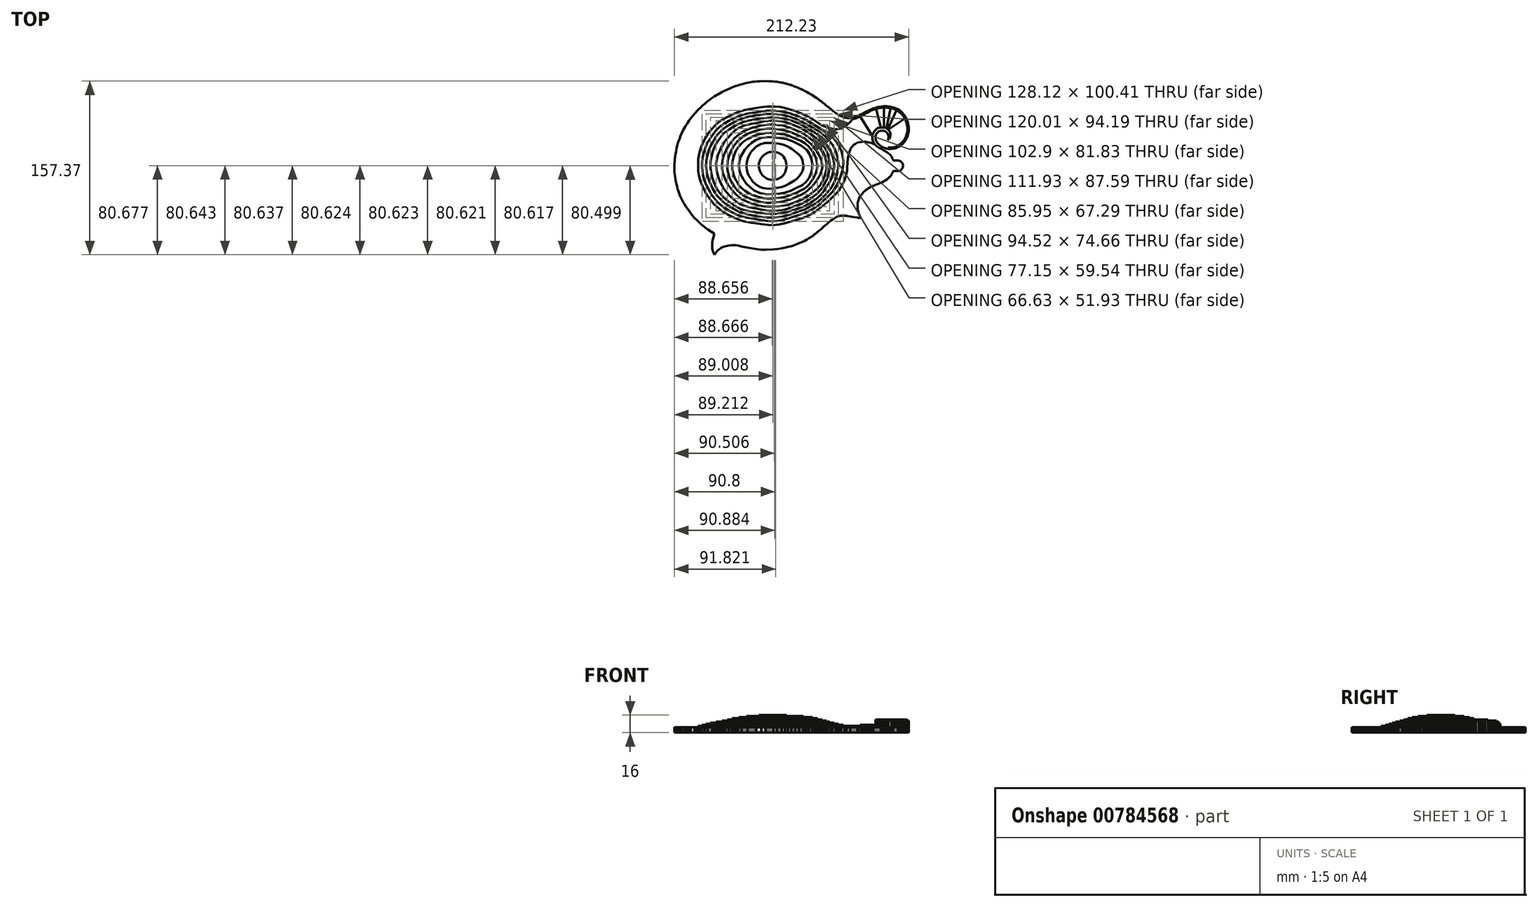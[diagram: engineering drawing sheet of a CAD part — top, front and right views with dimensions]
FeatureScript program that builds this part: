
annotation { "Feature Type Name" : "Feature", "Feature Type Description" : "" }
export const myFeature = defineFeature(function(context is Context, id is Id, definition is map)
    precondition{}
    {
        {
            var Q0;
            Q0=qCreatedBy(makeId("Top.planeOp"),FACE);
            var sketch = newSketch(context, id + "F0", { "sketchPlane" : qUnion([Q0])});
            skLineSegment(sketch, "E0", {"start": v(-90.73, -17.49) * mm, "end": v(-90.49, -12.16) * mm});
            skLineSegment(sketch, "E1", {"start": v(-90.49, -12.16) * mm, "end": v(-89.94, -7.25) * mm});
            skLineSegment(sketch, "E2", {"start": v(-89.94, -7.25) * mm, "end": v(-89.42, -4.36) * mm});
            skLineSegment(sketch, "E3", {"start": v(-89.42, -4.36) * mm, "end": v(-88.87, -1.75) * mm});
            skLineSegment(sketch, "E4", {"start": v(-88.87, -1.75) * mm, "end": v(-88.18, 1.03) * mm});
            skLineSegment(sketch, "E5", {"start": v(-88.18, 1.03) * mm, "end": v(-87.3, 4.01) * mm});
            skLineSegment(sketch, "E6", {"start": v(-87.3, 4.01) * mm, "end": v(-86.2, 7.14) * mm});
            skLineSegment(sketch, "E7", {"start": v(-86.2, 7.14) * mm, "end": v(-85.47, 9.1) * mm});
            skLineSegment(sketch, "E8", {"start": v(-85.47, 9.1) * mm, "end": v(-84.14, 12.2) * mm});
            skLineSegment(sketch, "E9", {"start": v(-84.14, 12.2) * mm, "end": v(-82.84, 14.94) * mm});
            skLineSegment(sketch, "E10", {"start": v(-82.84, 14.94) * mm, "end": v(-81, 18.16) * mm});
            skLineSegment(sketch, "E11", {"start": v(-81, 18.16) * mm, "end": v(-79.18, 21.04) * mm});
            skLineSegment(sketch, "E12", {"start": v(-79.18, 21.04) * mm, "end": v(-77.53, 23.47) * mm});
            skLineSegment(sketch, "E13", {"start": v(-77.53, 23.47) * mm, "end": v(-75.8, 25.8) * mm});
            skLineSegment(sketch, "E14", {"start": v(-75.8, 25.8) * mm, "end": v(-73.69, 28.43) * mm});
            skLineSegment(sketch, "E15", {"start": v(-73.69, 28.43) * mm, "end": v(-71.8, 30.51) * mm});
            skLineSegment(sketch, "E16", {"start": v(-71.8, 30.51) * mm, "end": v(-69.81, 32.66) * mm});
            skLineSegment(sketch, "E17", {"start": v(-69.81, 32.66) * mm, "end": v(-68.56, 33.97) * mm});
            skLineSegment(sketch, "E18", {"start": v(-68.56, 33.97) * mm, "end": v(-67.12, 35.38) * mm});
            skLineSegment(sketch, "E19", {"start": v(-67.12, 35.38) * mm, "end": v(-65.66, 36.77) * mm});
            skLineSegment(sketch, "E20", {"start": v(-65.66, 36.77) * mm, "end": v(-64.6, 37.7) * mm});
            skLineSegment(sketch, "E21", {"start": v(-64.6, 37.7) * mm, "end": v(-63.32, 38.85) * mm});
            skLineSegment(sketch, "E22", {"start": v(-63.32, 38.85) * mm, "end": v(-62.02, 39.95) * mm});
            skLineSegment(sketch, "E23", {"start": v(-62.02, 39.95) * mm, "end": v(-60.78, 40.93) * mm});
            skLineSegment(sketch, "E24", {"start": v(-60.78, 40.93) * mm, "end": v(-59.39, 42.03) * mm});
            skLineSegment(sketch, "E25", {"start": v(-59.39, 42.03) * mm, "end": v(-57.92, 43.11) * mm});
            skLineSegment(sketch, "E26", {"start": v(-57.92, 43.11) * mm, "end": v(-56.5, 44.12) * mm});
            skLineSegment(sketch, "E27", {"start": v(-56.5, 44.12) * mm, "end": v(-54.67, 45.42) * mm});
            skLineSegment(sketch, "E28", {"start": v(-54.67, 45.42) * mm, "end": v(-53.1, 46.38) * mm});
            skLineSegment(sketch, "E29", {"start": v(-53.1, 46.38) * mm, "end": v(-51.26, 47.42) * mm});
            skLineSegment(sketch, "E30", {"start": v(-51.26, 47.42) * mm, "end": v(-49.56, 48.36) * mm});
            skLineSegment(sketch, "E31", {"start": v(-49.56, 48.36) * mm, "end": v(-48.14, 49.14) * mm});
            skLineSegment(sketch, "E32", {"start": v(-48.14, 49.14) * mm, "end": v(-46.76, 49.84) * mm});
            skLineSegment(sketch, "E33", {"start": v(-46.76, 49.84) * mm, "end": v(-44.75, 50.78) * mm});
            skLineSegment(sketch, "E34", {"start": v(-44.75, 50.78) * mm, "end": v(-43.21, 51.49) * mm});
            skLineSegment(sketch, "E35", {"start": v(-43.21, 51.49) * mm, "end": v(-41.06, 52.46) * mm});
            skLineSegment(sketch, "E36", {"start": v(-41.06, 52.46) * mm, "end": v(-38.4, 53.58) * mm});
            skLineSegment(sketch, "E37", {"start": v(-38.4, 53.58) * mm, "end": v(-35.78, 54.58) * mm});
            skLineSegment(sketch, "E38", {"start": v(-35.78, 54.58) * mm, "end": v(-32.7, 55.68) * mm});
            skLineSegment(sketch, "E39", {"start": v(-32.7, 55.68) * mm, "end": v(-30.45, 56.33) * mm});
            skLineSegment(sketch, "E40", {"start": v(-30.45, 56.33) * mm, "end": v(-28.26, 56.95) * mm});
            skLineSegment(sketch, "E41", {"start": v(-28.26, 56.95) * mm, "end": v(-26.02, 57.5) * mm});
            skLineSegment(sketch, "E42", {"start": v(-26.02, 57.5) * mm, "end": v(-24.36, 57.85) * mm});
            skLineSegment(sketch, "E43", {"start": v(-24.36, 57.85) * mm, "end": v(-22.48, 58.22) * mm});
            skLineSegment(sketch, "E44", {"start": v(-22.48, 58.22) * mm, "end": v(-19.89, 58.62) * mm});
            skLineSegment(sketch, "E45", {"start": v(-19.89, 58.62) * mm, "end": v(-18.13, 58.79) * mm});
            skLineSegment(sketch, "E46", {"start": v(-18.13, 58.79) * mm, "end": v(-16.04, 58.97) * mm});
            skLineSegment(sketch, "E47", {"start": v(-16.04, 58.97) * mm, "end": v(-12.98, 59.17) * mm});
            skLineSegment(sketch, "E48", {"start": v(-12.98, 59.17) * mm, "end": v(-8.75, 59.27) * mm});
            skLineSegment(sketch, "E49", {"start": v(-8.75, 59.27) * mm, "end": v(-4.84, 59.18) * mm});
            skLineSegment(sketch, "E50", {"start": v(-4.84, 59.18) * mm, "end": v(-1.74, 58.96) * mm});
            skLineSegment(sketch, "E51", {"start": v(-1.74, 58.96) * mm, "end": v(0.31, 58.77) * mm});
            skLineSegment(sketch, "E52", {"start": v(0.31, 58.77) * mm, "end": v(1.94, 58.6) * mm});
            skLineSegment(sketch, "E53", {"start": v(1.94, 58.6) * mm, "end": v(3.32, 58.44) * mm});
            skLineSegment(sketch, "E54", {"start": v(3.32, 58.44) * mm, "end": v(4.55, 58.23) * mm});
            skLineSegment(sketch, "E55", {"start": v(4.55, 58.23) * mm, "end": v(5.65, 58.04) * mm});
            skLineSegment(sketch, "E56", {"start": v(5.65, 58.04) * mm, "end": v(6.75, 57.86) * mm});
            skLineSegment(sketch, "E57", {"start": v(6.75, 57.86) * mm, "end": v(7.65, 57.69) * mm});
            skLineSegment(sketch, "E58", {"start": v(7.65, 57.69) * mm, "end": v(8.56, 57.48) * mm});
            skLineSegment(sketch, "E59", {"start": v(8.56, 57.48) * mm, "end": v(9.35, 57.3) * mm});
            skLineSegment(sketch, "E60", {"start": v(9.35, 57.3) * mm, "end": v(10.09, 57.12) * mm});
            skLineSegment(sketch, "E61", {"start": v(10.09, 57.12) * mm, "end": v(10.82, 56.94) * mm});
            skLineSegment(sketch, "E62", {"start": v(10.82, 56.94) * mm, "end": v(11.57, 56.75) * mm});
            skLineSegment(sketch, "E63", {"start": v(11.57, 56.75) * mm, "end": v(12.15, 56.58) * mm});
            skLineSegment(sketch, "E64", {"start": v(12.15, 56.58) * mm, "end": v(12.86, 56.36) * mm});
            skLineSegment(sketch, "E65", {"start": v(12.86, 56.36) * mm, "end": v(13.4, 56.2) * mm});
            skLineSegment(sketch, "E66", {"start": v(13.4, 56.2) * mm, "end": v(13.97, 56.03) * mm});
            skLineSegment(sketch, "E67", {"start": v(13.97, 56.03) * mm, "end": v(14.53, 55.82) * mm});
            skLineSegment(sketch, "E68", {"start": v(14.53, 55.82) * mm, "end": v(15.06, 55.62) * mm});
            skLineSegment(sketch, "E69", {"start": v(15.06, 55.62) * mm, "end": v(15.62, 55.43) * mm});
            skLineSegment(sketch, "E70", {"start": v(15.62, 55.43) * mm, "end": v(16.05, 55.25) * mm});
            skLineSegment(sketch, "E71", {"start": v(16.05, 55.25) * mm, "end": v(16.59, 55.06) * mm});
            skLineSegment(sketch, "E72", {"start": v(16.59, 55.06) * mm, "end": v(17.1, 54.87) * mm});
            skLineSegment(sketch, "E73", {"start": v(17.1, 54.87) * mm, "end": v(17.51, 54.71) * mm});
            skLineSegment(sketch, "E74", {"start": v(17.51, 54.71) * mm, "end": v(18.44, 54.34) * mm});
            skLineSegment(sketch, "E75", {"start": v(18.44, 54.34) * mm, "end": v(19.47, 53.94) * mm});
            skLineSegment(sketch, "E76", {"start": v(19.47, 53.94) * mm, "end": v(20.27, 53.6) * mm});
            skLineSegment(sketch, "E77", {"start": v(20.27, 53.6) * mm, "end": v(21.17, 53.24) * mm});
            skLineSegment(sketch, "E78", {"start": v(21.17, 53.24) * mm, "end": v(22.1, 52.88) * mm});
            skLineSegment(sketch, "E79", {"start": v(22.1, 52.88) * mm, "end": v(22.85, 52.5) * mm});
            skLineSegment(sketch, "E80", {"start": v(22.85, 52.5) * mm, "end": v(23.77, 52.09) * mm});
            skLineSegment(sketch, "E81", {"start": v(23.77, 52.09) * mm, "end": v(24.55, 51.75) * mm});
            skLineSegment(sketch, "E82", {"start": v(24.55, 51.75) * mm, "end": v(25.29, 51.38) * mm});
            skLineSegment(sketch, "E83", {"start": v(25.29, 51.38) * mm, "end": v(26.02, 51) * mm});
            skLineSegment(sketch, "E84", {"start": v(26.02, 51) * mm, "end": v(26.39, 50.8) * mm});
            skLineSegment(sketch, "E85", {"start": v(26.39, 50.8) * mm, "end": v(26.77, 50.62) * mm});
            skLineSegment(sketch, "E86", {"start": v(26.77, 50.62) * mm, "end": v(27.14, 50.4) * mm});
            skLineSegment(sketch, "E87", {"start": v(27.14, 50.4) * mm, "end": v(27.45, 50.25) * mm});
            skLineSegment(sketch, "E88", {"start": v(27.45, 50.25) * mm, "end": v(29.55, 49.13) * mm});
            skLineSegment(sketch, "E89", {"start": v(29.55, 49.13) * mm, "end": v(31.21, 48.2) * mm});
            skLineSegment(sketch, "E90", {"start": v(31.21, 48.2) * mm, "end": v(32.16, 47.66) * mm});
            skLineSegment(sketch, "E91", {"start": v(32.16, 47.66) * mm, "end": v(33.95, 46.56) * mm});
            skLineSegment(sketch, "E92", {"start": v(33.95, 46.56) * mm, "end": v(35.48, 45.63) * mm});
            skLineSegment(sketch, "E93", {"start": v(35.48, 45.63) * mm, "end": v(36.04, 45.25) * mm});
            skLineSegment(sketch, "E94", {"start": v(36.04, 45.25) * mm, "end": v(37.69, 44.17) * mm});
            skLineSegment(sketch, "E95", {"start": v(37.69, 44.17) * mm, "end": v(38.24, 43.77) * mm});
            skLineSegment(sketch, "E96", {"start": v(38.24, 43.77) * mm, "end": v(38.98, 43.23) * mm});
            skLineSegment(sketch, "E97", {"start": v(38.98, 43.23) * mm, "end": v(39.53, 42.83) * mm});
            skLineSegment(sketch, "E98", {"start": v(39.53, 42.83) * mm, "end": v(40.29, 42.3) * mm});
            skLineSegment(sketch, "E99", {"start": v(40.29, 42.3) * mm, "end": v(41.03, 41.73) * mm});
            skLineSegment(sketch, "E100", {"start": v(41.03, 41.73) * mm, "end": v(41.75, 41.18) * mm});
            skLineSegment(sketch, "E101", {"start": v(41.75, 41.18) * mm, "end": v(42.49, 40.62) * mm});
            skLineSegment(sketch, "E102", {"start": v(42.49, 40.62) * mm, "end": v(43.24, 40.06) * mm});
            skLineSegment(sketch, "E103", {"start": v(43.24, 40.06) * mm, "end": v(43.98, 39.52) * mm});
            skLineSegment(sketch, "E104", {"start": v(43.98, 39.52) * mm, "end": v(44.9, 38.79) * mm});
            skLineSegment(sketch, "E105", {"start": v(44.9, 38.79) * mm, "end": v(45.64, 38.22) * mm});
            skLineSegment(sketch, "E106", {"start": v(45.64, 38.22) * mm, "end": v(46.77, 37.27) * mm});
            skLineSegment(sketch, "E107", {"start": v(46.77, 37.27) * mm, "end": v(47.87, 36.36) * mm});
            skLineSegment(sketch, "E108", {"start": v(47.87, 36.36) * mm, "end": v(48.43, 35.82) * mm});
            skLineSegment(sketch, "E109", {"start": v(48.43, 35.82) * mm, "end": v(49.16, 35.25) * mm});
            skLineSegment(sketch, "E110", {"start": v(49.16, 35.25) * mm, "end": v(50.1, 34.5) * mm});
            skLineSegment(sketch, "E111", {"start": v(50.1, 34.5) * mm, "end": v(51.21, 33.58) * mm});
            skLineSegment(sketch, "E112", {"start": v(51.21, 33.58) * mm, "end": v(52.32, 32.66) * mm});
            skLineSegment(sketch, "E113", {"start": v(52.32, 32.66) * mm, "end": v(53.25, 31.92) * mm});
            skLineSegment(sketch, "E114", {"start": v(53.25, 31.92) * mm, "end": v(54.18, 31.2) * mm});
            skLineSegment(sketch, "E115", {"start": v(54.18, 31.2) * mm, "end": v(55.48, 30.26) * mm});
            skLineSegment(sketch, "E116", {"start": v(55.48, 30.26) * mm, "end": v(56.04, 29.9) * mm});
            skLineSegment(sketch, "E117", {"start": v(56.04, 29.9) * mm, "end": v(57, 29.3) * mm});
            skLineSegment(sketch, "E118", {"start": v(57, 29.3) * mm, "end": v(58.07, 28.6) * mm});
            skLineSegment(sketch, "E119", {"start": v(58.07, 28.6) * mm, "end": v(58.82, 28.22) * mm});
            skLineSegment(sketch, "E120", {"start": v(58.82, 28.22) * mm, "end": v(59.92, 27.67) * mm});
            skLineSegment(sketch, "E121", {"start": v(59.92, 27.67) * mm, "end": v(61.58, 26.92) * mm});
            skLineSegment(sketch, "E122", {"start": v(61.58, 26.92) * mm, "end": v(62.69, 26.55) * mm});
            skLineSegment(sketch, "E123", {"start": v(62.69, 26.55) * mm, "end": v(63.27, 26.37) * mm});
            skLineSegment(sketch, "E124", {"start": v(63.27, 26.37) * mm, "end": v(63.92, 26.2) * mm});
            skLineSegment(sketch, "E125", {"start": v(63.92, 26.2) * mm, "end": v(64.73, 26) * mm});
            skLineSegment(sketch, "E126", {"start": v(64.73, 26) * mm, "end": v(66.12, 25.82) * mm});
            skLineSegment(sketch, "E127", {"start": v(66.12, 25.82) * mm, "end": v(69.04, 25.82) * mm});
            skLineSegment(sketch, "E128", {"start": v(69.04, 25.82) * mm, "end": v(70.29, 26) * mm});
            skLineSegment(sketch, "E129", {"start": v(70.29, 26) * mm, "end": v(71.13, 26.2) * mm});
            skLineSegment(sketch, "E130", {"start": v(71.13, 26.2) * mm, "end": v(71.78, 26.36) * mm});
            skLineSegment(sketch, "E131", {"start": v(71.78, 26.36) * mm, "end": v(72.36, 26.58) * mm});
            skLineSegment(sketch, "E132", {"start": v(72.36, 26.58) * mm, "end": v(72.89, 26.77) * mm});
            skLineSegment(sketch, "E133", {"start": v(72.89, 26.77) * mm, "end": v(73.43, 26.98) * mm});
            skLineSegment(sketch, "E134", {"start": v(73.43, 26.98) * mm, "end": v(74.74, 27.48) * mm});
            skLineSegment(sketch, "E135", {"start": v(74.74, 27.48) * mm, "end": v(76.05, 28.07) * mm});
            skLineSegment(sketch, "E136", {"start": v(76.05, 28.07) * mm, "end": v(77.54, 28.8) * mm});
            skLineSegment(sketch, "E137", {"start": v(77.54, 28.8) * mm, "end": v(78.66, 29.34) * mm});
            skLineSegment(sketch, "E138", {"start": v(78.66, 29.34) * mm, "end": v(79.76, 29.9) * mm});
            skLineSegment(sketch, "E139", {"start": v(79.76, 29.9) * mm, "end": v(80.87, 30.46) * mm});
            skLineSegment(sketch, "E140", {"start": v(80.87, 30.46) * mm, "end": v(81.92, 31.03) * mm});
            skLineSegment(sketch, "E141", {"start": v(81.92, 31.03) * mm, "end": v(82.63, 31.4) * mm});
            skLineSegment(sketch, "E142", {"start": v(82.63, 31.4) * mm, "end": v(83.3, 31.75) * mm});
            skLineSegment(sketch, "E143", {"start": v(83.3, 31.75) * mm, "end": v(84.02, 32.1) * mm});
            skLineSegment(sketch, "E144", {"start": v(84.02, 32.1) * mm, "end": v(84.74, 32.48) * mm});
            skLineSegment(sketch, "E145", {"start": v(84.74, 32.48) * mm, "end": v(85.48, 32.86) * mm});
            skLineSegment(sketch, "E146", {"start": v(85.48, 32.86) * mm, "end": v(86.76, 33.42) * mm});
            skLineSegment(sketch, "E147", {"start": v(86.76, 33.42) * mm, "end": v(87.63, 33.8) * mm});
            skLineSegment(sketch, "E148", {"start": v(87.63, 33.8) * mm, "end": v(88.56, 34.16) * mm});
            skLineSegment(sketch, "E149", {"start": v(88.56, 34.16) * mm, "end": v(89.57, 34.54) * mm});
            skLineSegment(sketch, "E150", {"start": v(89.57, 34.54) * mm, "end": v(91.24, 35.07) * mm});
            skLineSegment(sketch, "E151", {"start": v(91.24, 35.07) * mm, "end": v(91.98, 35.27) * mm});
            skLineSegment(sketch, "E152", {"start": v(91.98, 35.27) * mm, "end": v(92.56, 35.43) * mm});
            skLineSegment(sketch, "E153", {"start": v(92.56, 35.43) * mm, "end": v(93.45, 35.62) * mm});
            skLineSegment(sketch, "E154", {"start": v(93.45, 35.62) * mm, "end": v(94.31, 35.8) * mm});
            skLineSegment(sketch, "E155", {"start": v(94.31, 35.8) * mm, "end": v(95.34, 35.99) * mm});
            skLineSegment(sketch, "E156", {"start": v(95.34, 35.99) * mm, "end": v(96.73, 36.18) * mm});
            skLineSegment(sketch, "E157", {"start": v(96.73, 36.18) * mm, "end": v(98.6, 36.4) * mm});
            skLineSegment(sketch, "E158", {"start": v(98.6, 36.4) * mm, "end": v(99.66, 36.4) * mm});
            skLineSegment(sketch, "E159", {"start": v(99.66, 36.4) * mm, "end": v(101.85, 36.4) * mm});
            skLineSegment(sketch, "E160", {"start": v(101.85, 36.4) * mm, "end": v(103.93, 36.19) * mm});
            skLineSegment(sketch, "E161", {"start": v(103.93, 36.19) * mm, "end": v(105.16, 36) * mm});
            skLineSegment(sketch, "E162", {"start": v(105.16, 36) * mm, "end": v(106.06, 35.78) * mm});
            skLineSegment(sketch, "E163", {"start": v(106.06, 35.78) * mm, "end": v(106.82, 35.6) * mm});
            skLineSegment(sketch, "E164", {"start": v(106.82, 35.6) * mm, "end": v(107.52, 35.43) * mm});
            skLineSegment(sketch, "E165", {"start": v(107.52, 35.43) * mm, "end": v(108.13, 35.28) * mm});
            skLineSegment(sketch, "E166", {"start": v(108.13, 35.28) * mm, "end": v(108.67, 35.07) * mm});
            skLineSegment(sketch, "E167", {"start": v(108.67, 35.07) * mm, "end": v(109.2, 34.9) * mm});
            skLineSegment(sketch, "E168", {"start": v(109.2, 34.9) * mm, "end": v(109.64, 34.71) * mm});
            skLineSegment(sketch, "E169", {"start": v(109.64, 34.71) * mm, "end": v(110.14, 34.52) * mm});
            skLineSegment(sketch, "E170", {"start": v(110.14, 34.52) * mm, "end": v(110.47, 34.3) * mm});
            skLineSegment(sketch, "E171", {"start": v(110.47, 34.3) * mm, "end": v(111.22, 33.97) * mm});
            skLineSegment(sketch, "E172", {"start": v(111.22, 33.97) * mm, "end": v(111.6, 33.79) * mm});
            skLineSegment(sketch, "E173", {"start": v(111.6, 33.79) * mm, "end": v(111.88, 33.6) * mm});
            skLineSegment(sketch, "E174", {"start": v(111.88, 33.6) * mm, "end": v(112.16, 33.42) * mm});
            skLineSegment(sketch, "E175", {"start": v(112.16, 33.42) * mm, "end": v(112.5, 33.2) * mm});
            skLineSegment(sketch, "E176", {"start": v(112.5, 33.2) * mm, "end": v(112.73, 33.05) * mm});
            skLineSegment(sketch, "E177", {"start": v(112.73, 33.05) * mm, "end": v(113.05, 32.84) * mm});
            skLineSegment(sketch, "E178", {"start": v(113.05, 32.84) * mm, "end": v(113.3, 32.67) * mm});
            skLineSegment(sketch, "E179", {"start": v(113.3, 32.67) * mm, "end": v(113.82, 32.29) * mm});
            skLineSegment(sketch, "E180", {"start": v(113.82, 32.29) * mm, "end": v(114.35, 31.85) * mm});
            skLineSegment(sketch, "E181", {"start": v(114.35, 31.85) * mm, "end": v(114.74, 31.53) * mm});
            skLineSegment(sketch, "E182", {"start": v(114.74, 31.53) * mm, "end": v(115.12, 31.17) * mm});
            skLineSegment(sketch, "E183", {"start": v(115.12, 31.17) * mm, "end": v(115.5, 30.8) * mm});
            skLineSegment(sketch, "E184", {"start": v(115.5, 30.8) * mm, "end": v(115.87, 30.44) * mm});
            skLineSegment(sketch, "E185", {"start": v(115.87, 30.44) * mm, "end": v(116.26, 30.04) * mm});
            skLineSegment(sketch, "E186", {"start": v(116.26, 30.04) * mm, "end": v(116.58, 29.7) * mm});
            skLineSegment(sketch, "E187", {"start": v(116.58, 29.7) * mm, "end": v(116.83, 29.32) * mm});
            skLineSegment(sketch, "E188", {"start": v(116.83, 29.32) * mm, "end": v(117.01, 29.1) * mm});
            skLineSegment(sketch, "E189", {"start": v(117.01, 29.1) * mm, "end": v(117.34, 28.67) * mm});
            skLineSegment(sketch, "E190", {"start": v(117.34, 28.67) * mm, "end": v(117.56, 28.34) * mm});
            skLineSegment(sketch, "E191", {"start": v(117.56, 28.34) * mm, "end": v(117.76, 28.03) * mm});
            skLineSegment(sketch, "E192", {"start": v(117.76, 28.03) * mm, "end": v(118.08, 27.6) * mm});
            skLineSegment(sketch, "E193", {"start": v(118.08, 27.6) * mm, "end": v(118.38, 27.15) * mm});
            skLineSegment(sketch, "E194", {"start": v(118.38, 27.15) * mm, "end": v(118.65, 26.63) * mm});
            skLineSegment(sketch, "E195", {"start": v(118.65, 26.63) * mm, "end": v(118.85, 26.23) * mm});
            skLineSegment(sketch, "E196", {"start": v(118.85, 26.23) * mm, "end": v(119.19, 25.6) * mm});
            skLineSegment(sketch, "E197", {"start": v(119.19, 25.6) * mm, "end": v(119.4, 25.26) * mm});
            skLineSegment(sketch, "E198", {"start": v(119.4, 25.26) * mm, "end": v(119.56, 24.85) * mm});
            skLineSegment(sketch, "E199", {"start": v(119.56, 24.85) * mm, "end": v(119.77, 24.3) * mm});
            skLineSegment(sketch, "E200", {"start": v(119.77, 24.3) * mm, "end": v(120.1, 23.42) * mm});
            skLineSegment(sketch, "E201", {"start": v(120.1, 23.42) * mm, "end": v(120.32, 22.86) * mm});
            skLineSegment(sketch, "E202", {"start": v(120.32, 22.86) * mm, "end": v(120.48, 22.29) * mm});
            skLineSegment(sketch, "E203", {"start": v(120.48, 22.29) * mm, "end": v(120.66, 21.55) * mm});
            skLineSegment(sketch, "E204", {"start": v(120.66, 21.55) * mm, "end": v(120.87, 20.8) * mm});
            skLineSegment(sketch, "E205", {"start": v(120.87, 20.8) * mm, "end": v(121.05, 20.04) * mm});
            skLineSegment(sketch, "E206", {"start": v(121.05, 20.04) * mm, "end": v(121.23, 18.95) * mm});
            skLineSegment(sketch, "E207", {"start": v(121.23, 18.95) * mm, "end": v(121.43, 17.25) * mm});
            skLineSegment(sketch, "E208", {"start": v(121.43, 17.25) * mm, "end": v(121.43, 14.3) * mm});
            skLineSegment(sketch, "E209", {"start": v(121.43, 14.3) * mm, "end": v(121.23, 12.65) * mm});
            skLineSegment(sketch, "E210", {"start": v(121.23, 12.65) * mm, "end": v(121.05, 11.66) * mm});
            skLineSegment(sketch, "E211", {"start": v(121.05, 11.66) * mm, "end": v(120.84, 10.8) * mm});
            skLineSegment(sketch, "E212", {"start": v(120.84, 10.8) * mm, "end": v(120.69, 10.2) * mm});
            skLineSegment(sketch, "E213", {"start": v(120.69, 10.2) * mm, "end": v(120.5, 9.59) * mm});
            skLineSegment(sketch, "E214", {"start": v(120.5, 9.59) * mm, "end": v(120.3, 8.99) * mm});
            skLineSegment(sketch, "E215", {"start": v(120.3, 8.99) * mm, "end": v(120.11, 8.56) * mm});
            skLineSegment(sketch, "E216", {"start": v(120.11, 8.56) * mm, "end": v(119.9, 8.04) * mm});
            skLineSegment(sketch, "E217", {"start": v(119.9, 8.04) * mm, "end": v(119.74, 7.67) * mm});
            skLineSegment(sketch, "E218", {"start": v(119.74, 7.67) * mm, "end": v(119.56, 7.26) * mm});
            skLineSegment(sketch, "E219", {"start": v(119.56, 7.26) * mm, "end": v(119.37, 6.88) * mm});
            skLineSegment(sketch, "E220", {"start": v(119.37, 6.88) * mm, "end": v(119.17, 6.57) * mm});
            skLineSegment(sketch, "E221", {"start": v(119.17, 6.57) * mm, "end": v(118.8, 5.82) * mm});
            skLineSegment(sketch, "E222", {"start": v(118.8, 5.82) * mm, "end": v(118.46, 5.3) * mm});
            skLineSegment(sketch, "E223", {"start": v(118.46, 5.3) * mm, "end": v(118.07, 4.7) * mm});
            skLineSegment(sketch, "E224", {"start": v(118.07, 4.7) * mm, "end": v(117.89, 4.51) * mm});
            skLineSegment(sketch, "E225", {"start": v(117.89, 4.51) * mm, "end": v(117.54, 3.98) * mm});
            skLineSegment(sketch, "E226", {"start": v(117.54, 3.98) * mm, "end": v(117.16, 3.57) * mm});
            skLineSegment(sketch, "E227", {"start": v(117.16, 3.57) * mm, "end": v(116.39, 2.73) * mm});
            skLineSegment(sketch, "E228", {"start": v(116.39, 2.73) * mm, "end": v(116, 2.33) * mm});
            skLineSegment(sketch, "E229", {"start": v(116, 2.33) * mm, "end": v(115.12, 1.54) * mm});
            skLineSegment(sketch, "E230", {"start": v(115.12, 1.54) * mm, "end": v(114.2, 0.83) * mm});
            skLineSegment(sketch, "E231", {"start": v(114.2, 0.83) * mm, "end": v(113.63, 0.4) * mm});
            skLineSegment(sketch, "E232", {"start": v(113.63, 0.4) * mm, "end": v(113.07, 0.08) * mm});
            skLineSegment(sketch, "E233", {"start": v(113.07, 0.08) * mm, "end": v(112.35, -0.31) * mm});
            skLineSegment(sketch, "E234", {"start": v(112.35, -0.31) * mm, "end": v(111.6, -0.67) * mm});
            skLineSegment(sketch, "E235", {"start": v(111.6, -0.67) * mm, "end": v(110.85, -1.04) * mm});
            skLineSegment(sketch, "E236", {"start": v(110.85, -1.04) * mm, "end": v(110.32, -1.24) * mm});
            skLineSegment(sketch, "E237", {"start": v(110.32, -1.24) * mm, "end": v(109.74, -1.44) * mm});
            skLineSegment(sketch, "E238", {"start": v(109.74, -1.44) * mm, "end": v(109.2, -1.59) * mm});
            skLineSegment(sketch, "E239", {"start": v(109.2, -1.59) * mm, "end": v(108.46, -1.78) * mm});
            skLineSegment(sketch, "E240", {"start": v(108.46, -1.78) * mm, "end": v(107.52, -1.94) * mm});
            skLineSegment(sketch, "E241", {"start": v(107.52, -1.94) * mm, "end": v(106.03, -2.15) * mm});
            skLineSegment(sketch, "E242", {"start": v(106.03, -2.15) * mm, "end": v(102.9, -2.15) * mm});
            skLineSegment(sketch, "E243", {"start": v(102.9, -2.15) * mm, "end": v(101.96, -1.98) * mm});
            skLineSegment(sketch, "E244", {"start": v(101.96, -1.98) * mm, "end": v(101.06, -1.8) * mm});
            skLineSegment(sketch, "E245", {"start": v(101.06, -1.8) * mm, "end": v(100.3, -1.61) * mm});
            skLineSegment(sketch, "E246", {"start": v(100.3, -1.61) * mm, "end": v(99.71, -1.42) * mm});
            skLineSegment(sketch, "E247", {"start": v(99.71, -1.42) * mm, "end": v(99.18, -1.2) * mm});
            skLineSegment(sketch, "E248", {"start": v(99.18, -1.2) * mm, "end": v(98.81, -1.04) * mm});
            skLineSegment(sketch, "E249", {"start": v(98.81, -1.04) * mm, "end": v(97.53, -0.47) * mm});
            skLineSegment(sketch, "E250", {"start": v(97.53, -0.47) * mm, "end": v(96.93, -0.07) * mm});
            skLineSegment(sketch, "E251", {"start": v(96.93, -0.07) * mm, "end": v(96.32, 0.33) * mm});
            skLineSegment(sketch, "E252", {"start": v(96.32, 0.33) * mm, "end": v(95.57, 0.88) * mm});
            skLineSegment(sketch, "E253", {"start": v(95.57, 0.88) * mm, "end": v(94.7, 1.6) * mm});
            skLineSegment(sketch, "E254", {"start": v(94.7, 1.6) * mm, "end": v(94.13, 2.2) * mm});
            skLineSegment(sketch, "E255", {"start": v(94.13, 2.2) * mm, "end": v(93.29, 3.02) * mm});
            skLineSegment(sketch, "E256", {"start": v(93.29, 3.02) * mm, "end": v(92.71, 3.8) * mm});
            skLineSegment(sketch, "E257", {"start": v(92.71, 3.8) * mm, "end": v(92.15, 4.84) * mm});
            skLineSegment(sketch, "E258", {"start": v(92.15, 4.84) * mm, "end": v(91.8, 5.77) * mm});
            skLineSegment(sketch, "E259", {"start": v(91.8, 5.77) * mm, "end": v(91.58, 6.37) * mm});
            skLineSegment(sketch, "E260", {"start": v(91.58, 6.37) * mm, "end": v(91.4, 7.13) * mm});
            skLineSegment(sketch, "E261", {"start": v(91.4, 7.13) * mm, "end": v(91.4, 9.3) * mm});
            skLineSegment(sketch, "E262", {"start": v(91.4, 9.3) * mm, "end": v(91.6, 10.27) * mm});
            skLineSegment(sketch, "E263", {"start": v(91.6, 10.27) * mm, "end": v(91.77, 10.77) * mm});
            skLineSegment(sketch, "E264", {"start": v(91.77, 10.77) * mm, "end": v(92.15, 11.53) * mm});
            skLineSegment(sketch, "E265", {"start": v(92.15, 11.53) * mm, "end": v(92.52, 12.1) * mm});
            skLineSegment(sketch, "E266", {"start": v(92.52, 12.1) * mm, "end": v(93.26, 12.85) * mm});
            skLineSegment(sketch, "E267", {"start": v(93.26, 12.85) * mm, "end": v(93.66, 13.23) * mm});
            skLineSegment(sketch, "E268", {"start": v(93.66, 13.23) * mm, "end": v(94.2, 13.6) * mm});
            skLineSegment(sketch, "E269", {"start": v(94.2, 13.6) * mm, "end": v(94.93, 13.94) * mm});
            skLineSegment(sketch, "E270", {"start": v(94.93, 13.94) * mm, "end": v(95.33, 14.13) * mm});
            skLineSegment(sketch, "E271", {"start": v(95.33, 14.13) * mm, "end": v(96.21, 14.33) * mm});
            skLineSegment(sketch, "E272", {"start": v(96.21, 14.33) * mm, "end": v(98.26, 14.33) * mm});
            skLineSegment(sketch, "E273", {"start": v(98.26, 14.33) * mm, "end": v(99.19, 14.14) * mm});
            skLineSegment(sketch, "E274", {"start": v(99.19, 14.14) * mm, "end": v(99.75, 13.95) * mm});
            skLineSegment(sketch, "E275", {"start": v(99.75, 13.95) * mm, "end": v(100.13, 13.78) * mm});
            skLineSegment(sketch, "E276", {"start": v(100.13, 13.78) * mm, "end": v(100.69, 13.41) * mm});
            skLineSegment(sketch, "E277", {"start": v(100.69, 13.41) * mm, "end": v(101.57, 12.61) * mm});
            skLineSegment(sketch, "E278", {"start": v(101.57, 12.61) * mm, "end": v(102.15, 11.9) * mm});
            skLineSegment(sketch, "E279", {"start": v(102.15, 11.9) * mm, "end": v(102.51, 11.34) * mm});
            skLineSegment(sketch, "E280", {"start": v(102.51, 11.34) * mm, "end": v(102.9, 10.4) * mm});
            skLineSegment(sketch, "E281", {"start": v(102.9, 10.4) * mm, "end": v(103.1, 9.63) * mm});
            skLineSegment(sketch, "E282", {"start": v(103.1, 9.63) * mm, "end": v(103.27, 8.4) * mm});
            skLineSegment(sketch, "E283", {"start": v(103.27, 8.4) * mm, "end": v(103.08, 7.1) * mm});
            skLineSegment(sketch, "E284", {"start": v(103.08, 7.1) * mm, "end": v(102.9, 6.57) * mm});
            skLineSegment(sketch, "E285", {"start": v(102.9, 6.57) * mm, "end": v(102.54, 5.8) * mm});
            skLineSegment(sketch, "E286", {"start": v(102.54, 5.8) * mm, "end": v(103.1, 6.22) * mm});
            skLineSegment(sketch, "E287", {"start": v(103.1, 6.22) * mm, "end": v(103.45, 6.55) * mm});
            skLineSegment(sketch, "E288", {"start": v(103.45, 6.55) * mm, "end": v(103.67, 6.8) * mm});
            skLineSegment(sketch, "E289", {"start": v(103.67, 6.8) * mm, "end": v(104, 7.31) * mm});
            skLineSegment(sketch, "E290", {"start": v(104, 7.31) * mm, "end": v(104.5, 8.3) * mm});
            skLineSegment(sketch, "E291", {"start": v(104.5, 8.3) * mm, "end": v(104.78, 9.18) * mm});
            skLineSegment(sketch, "E292", {"start": v(104.78, 9.18) * mm, "end": v(104.91, 10.66) * mm});
            skLineSegment(sketch, "E293", {"start": v(104.91, 10.66) * mm, "end": v(104.59, 12.3) * mm});
            skLineSegment(sketch, "E294", {"start": v(104.59, 12.3) * mm, "end": v(104.08, 13.62) * mm});
            skLineSegment(sketch, "E295", {"start": v(104.08, 13.62) * mm, "end": v(103.48, 14.54) * mm});
            skLineSegment(sketch, "E296", {"start": v(103.48, 14.54) * mm, "end": v(102.84, 15.36) * mm});
            skLineSegment(sketch, "E297", {"start": v(102.84, 15.36) * mm, "end": v(102.18, 15.93) * mm});
            skLineSegment(sketch, "E298", {"start": v(102.18, 15.93) * mm, "end": v(101.57, 16.33) * mm});
            skLineSegment(sketch, "E299", {"start": v(101.57, 16.33) * mm, "end": v(100.85, 16.71) * mm});
            skLineSegment(sketch, "E300", {"start": v(100.85, 16.71) * mm, "end": v(99.75, 17.12) * mm});
            skLineSegment(sketch, "E301", {"start": v(99.75, 17.12) * mm, "end": v(99.01, 17.3) * mm});
            skLineSegment(sketch, "E302", {"start": v(99.01, 17.3) * mm, "end": v(95.88, 17.27) * mm});
            skLineSegment(sketch, "E303", {"start": v(95.88, 17.27) * mm, "end": v(94.92, 17.08) * mm});
            skLineSegment(sketch, "E304", {"start": v(94.92, 17.08) * mm, "end": v(94.36, 16.88) * mm});
            skLineSegment(sketch, "E305", {"start": v(94.36, 16.88) * mm, "end": v(93.79, 16.72) * mm});
            skLineSegment(sketch, "E306", {"start": v(93.79, 16.72) * mm, "end": v(93.06, 16.37) * mm});
            skLineSegment(sketch, "E307", {"start": v(93.06, 16.37) * mm, "end": v(92.56, 16) * mm});
            skLineSegment(sketch, "E308", {"start": v(92.56, 16) * mm, "end": v(92.03, 15.61) * mm});
            skLineSegment(sketch, "E309", {"start": v(92.03, 15.61) * mm, "end": v(91.62, 15.23) * mm});
            skLineSegment(sketch, "E310", {"start": v(91.62, 15.23) * mm, "end": v(90.67, 14.34) * mm});
            skLineSegment(sketch, "E311", {"start": v(90.67, 14.34) * mm, "end": v(90.24, 13.75) * mm});
            skLineSegment(sketch, "E312", {"start": v(90.24, 13.75) * mm, "end": v(89.65, 12.85) * mm});
            skLineSegment(sketch, "E313", {"start": v(89.65, 12.85) * mm, "end": v(89.2, 11.99) * mm});
            skLineSegment(sketch, "E314", {"start": v(89.2, 11.99) * mm, "end": v(89.02, 11.53) * mm});
            skLineSegment(sketch, "E315", {"start": v(89.02, 11.53) * mm, "end": v(88.8, 10.8) * mm});
            skLineSegment(sketch, "E316", {"start": v(88.8, 10.8) * mm, "end": v(88.64, 10.07) * mm});
            skLineSegment(sketch, "E317", {"start": v(88.64, 10.07) * mm, "end": v(88.64, 9.4) * mm});
            skLineSegment(sketch, "E318", {"start": v(88.64, 9.4) * mm, "end": v(88.64, 6.74) * mm});
            skLineSegment(sketch, "E319", {"start": v(88.64, 6.74) * mm, "end": v(88.82, 5.64) * mm});
            skLineSegment(sketch, "E320", {"start": v(88.82, 5.64) * mm, "end": v(89, 4.97) * mm});
            skLineSegment(sketch, "E321", {"start": v(89, 4.97) * mm, "end": v(89.19, 4.47) * mm});
            skLineSegment(sketch, "E322", {"start": v(89.19, 4.47) * mm, "end": v(89.4, 3.95) * mm});
            skLineSegment(sketch, "E323", {"start": v(89.4, 3.95) * mm, "end": v(89.56, 3.56) * mm});
            skLineSegment(sketch, "E324", {"start": v(89.56, 3.56) * mm, "end": v(89.78, 3.17) * mm});
            skLineSegment(sketch, "E325", {"start": v(89.78, 3.17) * mm, "end": v(90.66, 1.92) * mm});
            skLineSegment(sketch, "E326", {"start": v(90.66, 1.92) * mm, "end": v(91.6, 0.97) * mm});
            skLineSegment(sketch, "E327", {"start": v(91.6, 0.97) * mm, "end": v(92.34, 0.28) * mm});
            skLineSegment(sketch, "E328", {"start": v(92.34, 0.28) * mm, "end": v(94.2, -1.04) * mm});
            skLineSegment(sketch, "E329", {"start": v(94.2, -1.04) * mm, "end": v(95.31, -1.6) * mm});
            skLineSegment(sketch, "E330", {"start": v(95.31, -1.6) * mm, "end": v(96.8, -2.35) * mm});
            skLineSegment(sketch, "E331", {"start": v(96.8, -2.35) * mm, "end": v(98.82, -3.45) * mm});
            skLineSegment(sketch, "E332", {"start": v(98.82, -3.45) * mm, "end": v(101.4, -4.92) * mm});
            skLineSegment(sketch, "E333", {"start": v(101.4, -4.92) * mm, "end": v(102.52, -5.68) * mm});
            skLineSegment(sketch, "E334", {"start": v(102.52, -5.68) * mm, "end": v(103.26, -6.23) * mm});
            skLineSegment(sketch, "E335", {"start": v(103.26, -6.23) * mm, "end": v(104.05, -6.92) * mm});
            skLineSegment(sketch, "E336", {"start": v(104.05, -6.92) * mm, "end": v(104.93, -7.9) * mm});
            skLineSegment(sketch, "E337", {"start": v(104.93, -7.9) * mm, "end": v(105.5, -8.68) * mm});
            skLineSegment(sketch, "E338", {"start": v(105.5, -8.68) * mm, "end": v(105.88, -9.2) * mm});
            skLineSegment(sketch, "E339", {"start": v(105.88, -9.2) * mm, "end": v(106.24, -9.95) * mm});
            skLineSegment(sketch, "E340", {"start": v(106.24, -9.95) * mm, "end": v(106.79, -11.05) * mm});
            skLineSegment(sketch, "E341", {"start": v(106.79, -11.05) * mm, "end": v(107.14, -11.98) * mm});
            skLineSegment(sketch, "E342", {"start": v(107.14, -11.98) * mm, "end": v(107.52, -13.12) * mm});
            skLineSegment(sketch, "E343", {"start": v(107.52, -13.12) * mm, "end": v(107.93, -14.6) * mm});
            skLineSegment(sketch, "E344", {"start": v(107.93, -14.6) * mm, "end": v(108.1, -15.7) * mm});
            skLineSegment(sketch, "E345", {"start": v(108.1, -15.7) * mm, "end": v(108.27, -17.34) * mm});
            skLineSegment(sketch, "E346", {"start": v(108.27, -17.34) * mm, "end": v(108.08, -19.14) * mm});
            skLineSegment(sketch, "E347", {"start": v(108.08, -19.14) * mm, "end": v(107.74, -21.08) * mm});
            skLineSegment(sketch, "E348", {"start": v(107.74, -21.08) * mm, "end": v(107.18, -22.98) * mm});
            skLineSegment(sketch, "E349", {"start": v(107.18, -22.98) * mm, "end": v(106.4, -24.69) * mm});
            skLineSegment(sketch, "E350", {"start": v(106.4, -24.69) * mm, "end": v(105.77, -25.8) * mm});
            skLineSegment(sketch, "E351", {"start": v(105.77, -25.8) * mm, "end": v(105.2, -26.55) * mm});
            skLineSegment(sketch, "E352", {"start": v(105.2, -26.55) * mm, "end": v(104.35, -27.6) * mm});
            skLineSegment(sketch, "E353", {"start": v(104.35, -27.6) * mm, "end": v(103.92, -28) * mm});
            skLineSegment(sketch, "E354", {"start": v(103.92, -28) * mm, "end": v(103.27, -28.66) * mm});
            skLineSegment(sketch, "E355", {"start": v(103.27, -28.66) * mm, "end": v(102.52, -29.27) * mm});
            skLineSegment(sketch, "E356", {"start": v(102.52, -29.27) * mm, "end": v(101.73, -29.84) * mm});
            skLineSegment(sketch, "E357", {"start": v(101.73, -29.84) * mm, "end": v(100.4, -30.72) * mm});
            skLineSegment(sketch, "E358", {"start": v(100.4, -30.72) * mm, "end": v(99.6, -31.14) * mm});
            skLineSegment(sketch, "E359", {"start": v(99.6, -31.14) * mm, "end": v(98.66, -31.68) * mm});
            skLineSegment(sketch, "E360", {"start": v(98.66, -31.68) * mm, "end": v(96.98, -32.54) * mm});
            skLineSegment(sketch, "E361", {"start": v(96.98, -32.54) * mm, "end": v(96.18, -32.92) * mm});
            skLineSegment(sketch, "E362", {"start": v(96.18, -32.92) * mm, "end": v(94.88, -33.46) * mm});
            skLineSegment(sketch, "E363", {"start": v(94.88, -33.46) * mm, "end": v(93.07, -34.2) * mm});
            skLineSegment(sketch, "E364", {"start": v(93.07, -34.2) * mm, "end": v(91.77, -34.75) * mm});
            skLineSegment(sketch, "E365", {"start": v(91.77, -34.75) * mm, "end": v(89.56, -35.67) * mm});
            skLineSegment(sketch, "E366", {"start": v(89.56, -35.67) * mm, "end": v(88.26, -36.25) * mm});
            skLineSegment(sketch, "E367", {"start": v(88.26, -36.25) * mm, "end": v(87.5, -36.6) * mm});
            skLineSegment(sketch, "E368", {"start": v(87.5, -36.6) * mm, "end": v(86.76, -36.96) * mm});
            skLineSegment(sketch, "E369", {"start": v(86.76, -36.96) * mm, "end": v(86.02, -37.36) * mm});
            skLineSegment(sketch, "E370", {"start": v(86.02, -37.36) * mm, "end": v(85.1, -37.9) * mm});
            skLineSegment(sketch, "E371", {"start": v(85.1, -37.9) * mm, "end": v(84.52, -38.27) * mm});
            skLineSegment(sketch, "E372", {"start": v(84.52, -38.27) * mm, "end": v(83.96, -38.64) * mm});
            skLineSegment(sketch, "E373", {"start": v(83.96, -38.64) * mm, "end": v(83.26, -39.15) * mm});
            skLineSegment(sketch, "E374", {"start": v(83.26, -39.15) * mm, "end": v(82.5, -39.8) * mm});
            skLineSegment(sketch, "E375", {"start": v(82.5, -39.8) * mm, "end": v(81.78, -40.32) * mm});
            skLineSegment(sketch, "E376", {"start": v(81.78, -40.32) * mm, "end": v(81.37, -40.7) * mm});
            skLineSegment(sketch, "E377", {"start": v(81.37, -40.7) * mm, "end": v(80.63, -41.4) * mm});
            skLineSegment(sketch, "E378", {"start": v(80.63, -41.4) * mm, "end": v(79.54, -42.5) * mm});
            skLineSegment(sketch, "E379", {"start": v(79.54, -42.5) * mm, "end": v(78.26, -44.01) * mm});
            skLineSegment(sketch, "E380", {"start": v(78.26, -44.01) * mm, "end": v(77.32, -45.53) * mm});
            skLineSegment(sketch, "E381", {"start": v(77.32, -45.53) * mm, "end": v(76.6, -47.05) * mm});
            skLineSegment(sketch, "E382", {"start": v(76.6, -47.05) * mm, "end": v(76.04, -48.48) * mm});
            skLineSegment(sketch, "E383", {"start": v(76.04, -48.48) * mm, "end": v(75.63, -49.78) * mm});
            skLineSegment(sketch, "E384", {"start": v(75.63, -49.78) * mm, "end": v(75.3, -51.1) * mm});
            skLineSegment(sketch, "E385", {"start": v(75.3, -51.1) * mm, "end": v(75.13, -52.29) * mm});
            skLineSegment(sketch, "E386", {"start": v(75.13, -52.29) * mm, "end": v(75.13, -56.04) * mm});
            skLineSegment(sketch, "E387", {"start": v(75.13, -56.04) * mm, "end": v(75.31, -57.34) * mm});
            skLineSegment(sketch, "E388", {"start": v(75.31, -57.34) * mm, "end": v(75.5, -58.25) * mm});
            skLineSegment(sketch, "E389", {"start": v(75.5, -58.25) * mm, "end": v(75.68, -59.2) * mm});
            skLineSegment(sketch, "E390", {"start": v(75.68, -59.2) * mm, "end": v(76.03, -60.54) * mm});
            skLineSegment(sketch, "E391", {"start": v(76.03, -60.54) * mm, "end": v(76.41, -61.62) * mm});
            skLineSegment(sketch, "E392", {"start": v(76.41, -61.62) * mm, "end": v(76.82, -62.46) * mm});
            skLineSegment(sketch, "E393", {"start": v(76.82, -62.46) * mm, "end": v(77.31, -63.5) * mm});
            skLineSegment(sketch, "E394", {"start": v(77.31, -63.5) * mm, "end": v(77.72, -64.24) * mm});
            skLineSegment(sketch, "E395", {"start": v(77.72, -64.24) * mm, "end": v(78.4, -65.16) * mm});
            skLineSegment(sketch, "E396", {"start": v(78.4, -65.16) * mm, "end": v(75.91, -64.77) * mm});
            skLineSegment(sketch, "E397", {"start": v(75.91, -64.77) * mm, "end": v(74.93, -64.58) * mm});
            skLineSegment(sketch, "E398", {"start": v(74.93, -64.58) * mm, "end": v(73.84, -64.38) * mm});
            skLineSegment(sketch, "E399", {"start": v(73.84, -64.38) * mm, "end": v(71.8, -64.02) * mm});
            skLineSegment(sketch, "E400", {"start": v(71.8, -64.02) * mm, "end": v(69.76, -63.66) * mm});
            skLineSegment(sketch, "E401", {"start": v(69.76, -63.66) * mm, "end": v(68.65, -63.46) * mm});
            skLineSegment(sketch, "E402", {"start": v(68.65, -63.46) * mm, "end": v(66.46, -63.13) * mm});
            skLineSegment(sketch, "E403", {"start": v(66.46, -63.13) * mm, "end": v(65.09, -62.93) * mm});
            skLineSegment(sketch, "E404", {"start": v(65.09, -62.93) * mm, "end": v(63.48, -62.76) * mm});
            skLineSegment(sketch, "E405", {"start": v(63.48, -62.76) * mm, "end": v(60.3, -62.76) * mm});
            skLineSegment(sketch, "E406", {"start": v(60.3, -62.76) * mm, "end": v(59.18, -62.88) * mm});
            skLineSegment(sketch, "E407", {"start": v(59.18, -62.88) * mm, "end": v(58.23, -63.12) * mm});
            skLineSegment(sketch, "E408", {"start": v(58.23, -63.12) * mm, "end": v(57.12, -63.46) * mm});
            skLineSegment(sketch, "E409", {"start": v(57.12, -63.46) * mm, "end": v(56.12, -63.88) * mm});
            skLineSegment(sketch, "E410", {"start": v(56.12, -63.88) * mm, "end": v(55.05, -64.4) * mm});
            skLineSegment(sketch, "E411", {"start": v(55.05, -64.4) * mm, "end": v(54.23, -64.93) * mm});
            skLineSegment(sketch, "E412", {"start": v(54.23, -64.93) * mm, "end": v(52.2, -66.25) * mm});
            skLineSegment(sketch, "E413", {"start": v(52.2, -66.25) * mm, "end": v(51.48, -66.78) * mm});
            skLineSegment(sketch, "E414", {"start": v(51.48, -66.78) * mm, "end": v(50.65, -67.4) * mm});
            skLineSegment(sketch, "E415", {"start": v(50.65, -67.4) * mm, "end": v(49.1, -68.69) * mm});
            skLineSegment(sketch, "E416", {"start": v(49.1, -68.69) * mm, "end": v(48.23, -69.41) * mm});
            skLineSegment(sketch, "E417", {"start": v(48.23, -69.41) * mm, "end": v(47.46, -70.14) * mm});
            skLineSegment(sketch, "E418", {"start": v(47.46, -70.14) * mm, "end": v(46.14, -71.31) * mm});
            skLineSegment(sketch, "E419", {"start": v(46.14, -71.31) * mm, "end": v(45.11, -72.15) * mm});
            skLineSegment(sketch, "E420", {"start": v(45.11, -72.15) * mm, "end": v(44.23, -72.99) * mm});
            skLineSegment(sketch, "E421", {"start": v(44.23, -72.99) * mm, "end": v(43.04, -74.1) * mm});
            skLineSegment(sketch, "E422", {"start": v(43.04, -74.1) * mm, "end": v(41.73, -75.19) * mm});
            skLineSegment(sketch, "E423", {"start": v(41.73, -75.19) * mm, "end": v(40.9, -75.8) * mm});
            skLineSegment(sketch, "E424", {"start": v(40.9, -75.8) * mm, "end": v(39.78, -76.86) * mm});
            skLineSegment(sketch, "E425", {"start": v(39.78, -76.86) * mm, "end": v(38.73, -77.7) * mm});
            skLineSegment(sketch, "E426", {"start": v(38.73, -77.7) * mm, "end": v(38.06, -78.2) * mm});
            skLineSegment(sketch, "E427", {"start": v(38.06, -78.2) * mm, "end": v(36.72, -79.25) * mm});
            skLineSegment(sketch, "E428", {"start": v(36.72, -79.25) * mm, "end": v(35.96, -79.8) * mm});
            skLineSegment(sketch, "E429", {"start": v(35.96, -79.8) * mm, "end": v(35.06, -80.53) * mm});
            skLineSegment(sketch, "E430", {"start": v(35.06, -80.53) * mm, "end": v(33.79, -81.46) * mm});
            skLineSegment(sketch, "E431", {"start": v(33.79, -81.46) * mm, "end": v(32.7, -82.18) * mm});
            skLineSegment(sketch, "E432", {"start": v(32.7, -82.18) * mm, "end": v(30.99, -83.3) * mm});
            skLineSegment(sketch, "E433", {"start": v(30.99, -83.3) * mm, "end": v(29.19, -84.4) * mm});
            skLineSegment(sketch, "E434", {"start": v(29.19, -84.4) * mm, "end": v(27.46, -85.34) * mm});
            skLineSegment(sketch, "E435", {"start": v(27.46, -85.34) * mm, "end": v(25.65, -86.26) * mm});
            skLineSegment(sketch, "E436", {"start": v(25.65, -86.26) * mm, "end": v(22.31, -87.77) * mm});
            skLineSegment(sketch, "E437", {"start": v(22.31, -87.77) * mm, "end": v(18.6, -89.24) * mm});
            skLineSegment(sketch, "E438", {"start": v(18.6, -89.24) * mm, "end": v(15.16, -90.39) * mm});
            skLineSegment(sketch, "E439", {"start": v(15.16, -90.39) * mm, "end": v(11.89, -91.25) * mm});
            skLineSegment(sketch, "E440", {"start": v(11.89, -91.25) * mm, "end": v(9.39, -91.83) * mm});
            skLineSegment(sketch, "E441", {"start": v(9.39, -91.83) * mm, "end": v(6.4, -92.38) * mm});
            skLineSegment(sketch, "E442", {"start": v(6.4, -92.38) * mm, "end": v(2.3, -92.95) * mm});
            skLineSegment(sketch, "E443", {"start": v(2.3, -92.95) * mm, "end": v(-1.27, -93.3) * mm});
            skLineSegment(sketch, "E444", {"start": v(-1.27, -93.3) * mm, "end": v(-8.12, -93.64) * mm});
            skLineSegment(sketch, "E445", {"start": v(-8.12, -93.64) * mm, "end": v(-12.1, -93.64) * mm});
            skLineSegment(sketch, "E446", {"start": v(-12.1, -93.64) * mm, "end": v(-13.46, -93.5) * mm});
            skLineSegment(sketch, "E447", {"start": v(-13.46, -93.5) * mm, "end": v(-16.98, -93.14) * mm});
            skLineSegment(sketch, "E448", {"start": v(-16.98, -93.14) * mm, "end": v(-19.54, -92.68) * mm});
            skLineSegment(sketch, "E449", {"start": v(-19.54, -92.68) * mm, "end": v(-24.57, -91.8) * mm});
            skLineSegment(sketch, "E450", {"start": v(-24.57, -91.8) * mm, "end": v(-29.92, -90.72) * mm});
            skLineSegment(sketch, "E451", {"start": v(-29.92, -90.72) * mm, "end": v(-33.17, -89.92) * mm});
            skLineSegment(sketch, "E452", {"start": v(-33.17, -89.92) * mm, "end": v(-35.1, -89.58) * mm});
            skLineSegment(sketch, "E453", {"start": v(-35.1, -89.58) * mm, "end": v(-36.84, -89.4) * mm});
            skLineSegment(sketch, "E454", {"start": v(-36.84, -89.4) * mm, "end": v(-38.95, -89.4) * mm});
            skLineSegment(sketch, "E455", {"start": v(-38.95, -89.4) * mm, "end": v(-41.72, -89.79) * mm});
            skLineSegment(sketch, "E456", {"start": v(-41.72, -89.79) * mm, "end": v(-44.52, -90.34) * mm});
            skLineSegment(sketch, "E457", {"start": v(-44.52, -90.34) * mm, "end": v(-45.7, -90.66) * mm});
            skLineSegment(sketch, "E458", {"start": v(-45.7, -90.66) * mm, "end": v(-46.7, -91.08) * mm});
            skLineSegment(sketch, "E459", {"start": v(-46.7, -91.08) * mm, "end": v(-47.5, -91.46) * mm});
            skLineSegment(sketch, "E460", {"start": v(-47.5, -91.46) * mm, "end": v(-48.25, -91.87) * mm});
            skLineSegment(sketch, "E461", {"start": v(-48.25, -91.87) * mm, "end": v(-48.84, -92.3) * mm});
            skLineSegment(sketch, "E462", {"start": v(-48.84, -92.3) * mm, "end": v(-49.92, -93) * mm});
            skLineSegment(sketch, "E463", {"start": v(-49.92, -93) * mm, "end": v(-50.76, -93.7) * mm});
            skLineSegment(sketch, "E464", {"start": v(-50.76, -93.7) * mm, "end": v(-51.74, -94.56) * mm});
            skLineSegment(sketch, "E465", {"start": v(-51.74, -94.56) * mm, "end": v(-52.49, -95.39) * mm});
            skLineSegment(sketch, "E466", {"start": v(-52.49, -95.39) * mm, "end": v(-53.3, -96.38) * mm});
            skLineSegment(sketch, "E467", {"start": v(-53.3, -96.38) * mm, "end": v(-53.8, -97.15) * mm});
            skLineSegment(sketch, "E468", {"start": v(-53.8, -97.15) * mm, "end": v(-54.16, -97.77) * mm});
            skLineSegment(sketch, "E469", {"start": v(-54.16, -97.77) * mm, "end": v(-54.34, -98.1) * mm});
            skLineSegment(sketch, "E470", {"start": v(-54.34, -98.1) * mm, "end": v(-54.86, -97.32) * mm});
            skLineSegment(sketch, "E471", {"start": v(-54.86, -97.32) * mm, "end": v(-55.36, -96.54) * mm});
            skLineSegment(sketch, "E472", {"start": v(-55.36, -96.54) * mm, "end": v(-55.86, -95.34) * mm});
            skLineSegment(sketch, "E473", {"start": v(-55.86, -95.34) * mm, "end": v(-56.26, -93.96) * mm});
            skLineSegment(sketch, "E474", {"start": v(-56.26, -93.96) * mm, "end": v(-56.45, -92.97) * mm});
            skLineSegment(sketch, "E475", {"start": v(-56.45, -92.97) * mm, "end": v(-56.56, -92.28) * mm});
            skLineSegment(sketch, "E476", {"start": v(-56.56, -92.28) * mm, "end": v(-56.63, -90.89) * mm});
            skLineSegment(sketch, "E477", {"start": v(-56.63, -90.89) * mm, "end": v(-56.56, -88.65) * mm});
            skLineSegment(sketch, "E478", {"start": v(-56.56, -88.65) * mm, "end": v(-56.43, -87.14) * mm});
            skLineSegment(sketch, "E479", {"start": v(-56.43, -87.14) * mm, "end": v(-56.02, -84.8) * mm});
            skLineSegment(sketch, "E480", {"start": v(-56.02, -84.8) * mm, "end": v(-55.85, -83.85) * mm});
            skLineSegment(sketch, "E481", {"start": v(-55.85, -83.85) * mm, "end": v(-55.43, -81.89) * mm});
            skLineSegment(sketch, "E482", {"start": v(-55.43, -81.89) * mm, "end": v(-55.11, -80.6) * mm});
            skLineSegment(sketch, "E483", {"start": v(-55.11, -80.6) * mm, "end": v(-54.77, -79.18) * mm});
            skLineSegment(sketch, "E484", {"start": v(-54.77, -79.18) * mm, "end": v(-55.79, -78.5) * mm});
            skLineSegment(sketch, "E485", {"start": v(-55.79, -78.5) * mm, "end": v(-56.68, -77.93) * mm});
            skLineSegment(sketch, "E486", {"start": v(-56.68, -77.93) * mm, "end": v(-58.97, -76.42) * mm});
            skLineSegment(sketch, "E487", {"start": v(-58.97, -76.42) * mm, "end": v(-60.79, -75.22) * mm});
            skLineSegment(sketch, "E488", {"start": v(-60.79, -75.22) * mm, "end": v(-63.09, -73.49) * mm});
            skLineSegment(sketch, "E489", {"start": v(-63.09, -73.49) * mm, "end": v(-64.02, -72.71) * mm});
            skLineSegment(sketch, "E490", {"start": v(-64.02, -72.71) * mm, "end": v(-66.28, -70.8) * mm});
            skLineSegment(sketch, "E491", {"start": v(-66.28, -70.8) * mm, "end": v(-67.08, -70.08) * mm});
            skLineSegment(sketch, "E492", {"start": v(-67.08, -70.08) * mm, "end": v(-69.36, -67.93) * mm});
            skLineSegment(sketch, "E493", {"start": v(-69.36, -67.93) * mm, "end": v(-70.65, -66.66) * mm});
            skLineSegment(sketch, "E494", {"start": v(-70.65, -66.66) * mm, "end": v(-72.34, -64.96) * mm});
            skLineSegment(sketch, "E495", {"start": v(-72.34, -64.96) * mm, "end": v(-74.2, -62.74) * mm});
            skLineSegment(sketch, "E496", {"start": v(-74.2, -62.74) * mm, "end": v(-76.06, -60.49) * mm});
            skLineSegment(sketch, "E497", {"start": v(-76.06, -60.49) * mm, "end": v(-76.8, -59.48) * mm});
            skLineSegment(sketch, "E498", {"start": v(-76.8, -59.48) * mm, "end": v(-78.3, -57.53) * mm});
            skLineSegment(sketch, "E499", {"start": v(-78.3, -57.53) * mm, "end": v(-80.34, -54.5) * mm});
            skLineSegment(sketch, "E500", {"start": v(-80.34, -54.5) * mm, "end": v(-81.62, -52.53) * mm});
            skLineSegment(sketch, "E501", {"start": v(-81.62, -52.53) * mm, "end": v(-82.85, -50.32) * mm});
            skLineSegment(sketch, "E502", {"start": v(-82.85, -50.32) * mm, "end": v(-84.19, -47.87) * mm});
            skLineSegment(sketch, "E503", {"start": v(-84.19, -47.87) * mm, "end": v(-85.66, -44.8) * mm});
            skLineSegment(sketch, "E504", {"start": v(-85.66, -44.8) * mm, "end": v(-86.44, -42.93) * mm});
            skLineSegment(sketch, "E505", {"start": v(-86.44, -42.93) * mm, "end": v(-87.15, -40.92) * mm});
            skLineSegment(sketch, "E506", {"start": v(-87.15, -40.92) * mm, "end": v(-87.92, -38.53) * mm});
            skLineSegment(sketch, "E507", {"start": v(-87.92, -38.53) * mm, "end": v(-88.46, -36.55) * mm});
            skLineSegment(sketch, "E508", {"start": v(-88.46, -36.55) * mm, "end": v(-89.03, -34.25) * mm});
            skLineSegment(sketch, "E509", {"start": v(-89.03, -34.25) * mm, "end": v(-89.6, -31.6) * mm});
            skLineSegment(sketch, "E510", {"start": v(-89.6, -31.6) * mm, "end": v(-89.93, -29.62) * mm});
            skLineSegment(sketch, "E511", {"start": v(-89.93, -29.62) * mm, "end": v(-90.31, -27.06) * mm});
            skLineSegment(sketch, "E512", {"start": v(-90.31, -27.06) * mm, "end": v(-90.71, -23.04) * mm});
            skLineSegment(sketch, "E513", {"start": v(-90.71, -23.04) * mm, "end": v(-90.8, -19.14) * mm});
            skLineSegment(sketch, "E514", {"start": v(-90.8, -19.14) * mm, "end": v(-90.73, -17.49) * mm});
            skLineSegment(sketch, "E515", {"start": v(102.84, 15.36) * mm, "end": v(118.98, 25.98) * mm});
            skLineSegment(sketch, "E516", {"start": v(102.6, 15.56) * mm, "end": v(110.47, 33.05) * mm});
            skPoint(sketch, "E517.endSnap0", {"position": v(110.85, 34.13) * mm});
            skLineSegment(sketch, "E518", {"start": v(110.47, 33.05) * mm, "end": v(110.85, 34.13) * mm});
            skLineSegment(sketch, "E519", {"start": v(101.21, 16.52) * mm, "end": v(105.43, 35.94) * mm});
            skLineSegment(sketch, "E520", {"start": v(99.13, 36.4) * mm, "end": v(99.01, 17.3) * mm});
            skLineSegment(sketch, "E521", {"start": v(96.14, 17.27) * mm, "end": v(92.09, 34.1) * mm});
            skLineSegment(sketch, "E522", {"start": v(92.09, 34.1) * mm, "end": v(89.5, 33.27) * mm});
            skLineSegment(sketch, "E523", {"start": v(89.5, 33.27) * mm, "end": v(87.74, 32.56) * mm});
            skLineSegment(sketch, "E524", {"start": v(87.74, 32.56) * mm, "end": v(85.7, 31.61) * mm});
            skLineSegment(sketch, "E525", {"start": v(85.7, 31.61) * mm, "end": v(84.09, 30.78) * mm});
            skLineSegment(sketch, "E526", {"start": v(84.09, 30.78) * mm, "end": v(81.55, 29.45) * mm});
            skLineSegment(sketch, "E527", {"start": v(81.55, 29.45) * mm, "end": v(79.97, 28.64) * mm});
            skLineSegment(sketch, "E528", {"start": v(79.97, 28.64) * mm, "end": v(78.04, 27.65) * mm});
            skLineSegment(sketch, "E529", {"start": v(78.04, 27.65) * mm, "end": v(77.47, 27.37) * mm});
            skLineSegment(sketch, "E530", {"start": v(77.47, 27.37) * mm, "end": v(76.8, 28.43) * mm});
            skLineSegment(sketch, "E531", {"start": v(76.8, 28.43) * mm, "end": v(77.47, 27.37) * mm});
            skLineSegment(sketch, "E532", {"start": v(77.47, 27.37) * mm, "end": v(88.64, 9.4) * mm});
            skLineSegment(sketch, "E533", {"start": v(92.09, 34.1) * mm, "end": v(94.04, 34.57) * mm});
            skLineSegment(sketch, "E534", {"start": v(94.04, 34.57) * mm, "end": v(96.16, 34.89) * mm});
            skLineSegment(sketch, "E535", {"start": v(96.16, 34.89) * mm, "end": v(97.8, 35.1) * mm});
            skLineSegment(sketch, "E536", {"start": v(97.8, 35.1) * mm, "end": v(99.12, 35.17) * mm});
            skLineSegment(sketch, "E537", {"start": v(99.12, 35.17) * mm, "end": v(101.33, 35.16) * mm});
            skLineSegment(sketch, "E538", {"start": v(101.33, 35.16) * mm, "end": v(103.08, 35.08) * mm});
            skLineSegment(sketch, "E539", {"start": v(103.08, 35.08) * mm, "end": v(104.42, 34.92) * mm});
            skLineSegment(sketch, "E540", {"start": v(104.42, 34.92) * mm, "end": v(105.17, 34.75) * mm});
            skLineSegment(sketch, "E541", {"start": v(105.17, 34.75) * mm, "end": v(106.44, 34.48) * mm});
            skLineSegment(sketch, "E542", {"start": v(106.44, 34.48) * mm, "end": v(108.02, 34.04) * mm});
            skLineSegment(sketch, "E543", {"start": v(108.02, 34.04) * mm, "end": v(109.67, 33.36) * mm});
            skLineSegment(sketch, "E544", {"start": v(109.67, 33.36) * mm, "end": v(110.47, 33.05) * mm});
            skLineSegment(sketch, "E545", {"start": v(110.47, 33.05) * mm, "end": v(111.97, 32.15) * mm});
            skLineSegment(sketch, "E546", {"start": v(111.97, 32.15) * mm, "end": v(112.76, 31.6) * mm});
            skLineSegment(sketch, "E547", {"start": v(112.76, 31.6) * mm, "end": v(114.15, 30.5) * mm});
            skLineSegment(sketch, "E548", {"start": v(114.15, 30.5) * mm, "end": v(114.91, 29.7) * mm});
            skLineSegment(sketch, "E549", {"start": v(114.91, 29.7) * mm, "end": v(115.88, 28.6) * mm});
            skLineSegment(sketch, "E550", {"start": v(115.88, 28.6) * mm, "end": v(116.69, 27.56) * mm});
            skLineSegment(sketch, "E551", {"start": v(116.69, 27.56) * mm, "end": v(117.67, 25.92) * mm});
            skLineSegment(sketch, "E552", {"start": v(117.67, 25.92) * mm, "end": v(118.04, 25.35) * mm});
            skLineSegment(sketch, "E553", {"start": v(118.04, 25.35) * mm, "end": v(118.7, 23.75) * mm});
            skLineSegment(sketch, "E554", {"start": v(118.7, 23.75) * mm, "end": v(119.4, 21.7) * mm});
            skLineSegment(sketch, "E555", {"start": v(119.4, 21.7) * mm, "end": v(119.94, 19.27) * mm});
            skLineSegment(sketch, "E556", {"start": v(119.94, 19.27) * mm, "end": v(120.32, 16.55) * mm});
            skLineSegment(sketch, "E557", {"start": v(120.32, 16.55) * mm, "end": v(120.13, 13.48) * mm});
            skLineSegment(sketch, "E558", {"start": v(120.13, 13.48) * mm, "end": v(119.74, 11.42) * mm});
            skLineSegment(sketch, "E559", {"start": v(119.74, 11.42) * mm, "end": v(119.35, 10.02) * mm});
            skLineSegment(sketch, "E560", {"start": v(119.35, 10.02) * mm, "end": v(118.68, 8.06) * mm});
            skLineSegment(sketch, "E561", {"start": v(118.68, 8.06) * mm, "end": v(117.8, 6.5) * mm});
            skLineSegment(sketch, "E562", {"start": v(117.8, 6.5) * mm, "end": v(116.5, 4.65) * mm});
            skLineSegment(sketch, "E563", {"start": v(116.5, 4.65) * mm, "end": v(115.34, 3.37) * mm});
            skLineSegment(sketch, "E564", {"start": v(115.34, 3.37) * mm, "end": v(113.7, 1.9) * mm});
            skLineSegment(sketch, "E565", {"start": v(113.7, 1.9) * mm, "end": v(112.06, 0.92) * mm});
            skLineSegment(sketch, "E566", {"start": v(112.06, 0.92) * mm, "end": v(110.34, 0) * mm});
            skLineSegment(sketch, "E567", {"start": v(110.34, 0) * mm, "end": v(108.45, -0.55) * mm});
            skLineSegment(sketch, "E568", {"start": v(108.45, -0.55) * mm, "end": v(106.77, -0.87) * mm});
            skLineSegment(sketch, "E569", {"start": v(106.77, -0.87) * mm, "end": v(105.87, -0.97) * mm});
            skLineSegment(sketch, "E570", {"start": v(105.87, -0.97) * mm, "end": v(104.24, -1.03) * mm});
            skLineSegment(sketch, "E571", {"start": v(104.24, -1.03) * mm, "end": v(102.9, -0.95) * mm});
            skLineSegment(sketch, "E572", {"start": v(102.9, -0.95) * mm, "end": v(102.9, -2.15) * mm});
            skLineSegment(sketch, "E573", {"start": v(94.2, -1.04) * mm, "end": v(93.59, -2.04) * mm});
            skPoint(sketch, "E573.endSnap0", {"position": v(106.78, -2.04) * mm});
            skLineSegment(sketch, "E574", {"start": v(93.59, -2.04) * mm, "end": v(94.57, -2.55) * mm});
            skLineSegment(sketch, "E575", {"start": v(94.57, -2.55) * mm, "end": v(96.93, -3.77) * mm});
            skLineSegment(sketch, "E576", {"start": v(96.93, -3.77) * mm, "end": v(99.69, -5.2) * mm});
            skLineSegment(sketch, "E577", {"start": v(99.69, -5.2) * mm, "end": v(102.2, -6.95) * mm});
            skLineSegment(sketch, "E578", {"start": v(102.2, -6.95) * mm, "end": v(103.75, -8.32) * mm});
            skLineSegment(sketch, "E579", {"start": v(103.75, -8.32) * mm, "end": v(105.05, -10.3) * mm});
            skLineSegment(sketch, "E580", {"start": v(105.05, -10.3) * mm, "end": v(106.1, -12.36) * mm});
            skLineSegment(sketch, "E581", {"start": v(106.1, -12.36) * mm, "end": v(106.68, -14.63) * mm});
            skLineSegment(sketch, "E582", {"start": v(106.68, -14.63) * mm, "end": v(107, -16.09) * mm});
            skLineSegment(sketch, "E583", {"start": v(107, -16.09) * mm, "end": v(107.08, -18.4) * mm});
            skLineSegment(sketch, "E584", {"start": v(107.08, -18.4) * mm, "end": v(106.6, -20.4) * mm});
            skLineSegment(sketch, "E585", {"start": v(106.6, -20.4) * mm, "end": v(106.1, -22.2) * mm});
            skLineSegment(sketch, "E586", {"start": v(106.1, -22.2) * mm, "end": v(105.26, -24.27) * mm});
            skLineSegment(sketch, "E587", {"start": v(105.26, -24.27) * mm, "end": v(104.15, -26) * mm});
            skLineSegment(sketch, "E588", {"start": v(104.15, -26) * mm, "end": v(102.28, -27.95) * mm});
            skLineSegment(sketch, "E589", {"start": v(102.28, -27.95) * mm, "end": v(100.21, -29.48) * mm});
            skLineSegment(sketch, "E590", {"start": v(100.21, -29.48) * mm, "end": v(96.06, -31.63) * mm});
            skLineSegment(sketch, "E591", {"start": v(96.06, -31.63) * mm, "end": v(88.18, -34.96) * mm});
            skLineSegment(sketch, "E592", {"start": v(88.18, -34.96) * mm, "end": v(85.96, -35.98) * mm});
            skLineSegment(sketch, "E593", {"start": v(85.96, -35.98) * mm, "end": v(83.64, -37.27) * mm});
            skLineSegment(sketch, "E594", {"start": v(83.64, -37.27) * mm, "end": v(81, -39.4) * mm});
            skLineSegment(sketch, "E595", {"start": v(81, -39.4) * mm, "end": v(79.38, -40.85) * mm});
            skLineSegment(sketch, "E596", {"start": v(79.38, -40.85) * mm, "end": v(78.48, -41.81) * mm});
            skLineSegment(sketch, "E597", {"start": v(78.48, -41.81) * mm, "end": v(77.4, -43.17) * mm});
            skLineSegment(sketch, "E598", {"start": v(77.4, -43.17) * mm, "end": v(76.28, -45) * mm});
            skLineSegment(sketch, "E599", {"start": v(76.28, -45) * mm, "end": v(75.64, -46.24) * mm});
            skLineSegment(sketch, "E600", {"start": v(75.64, -46.24) * mm, "end": v(75.11, -47.77) * mm});
            skLineSegment(sketch, "E601", {"start": v(75.11, -47.77) * mm, "end": v(74.33, -50.04) * mm});
            skLineSegment(sketch, "E602", {"start": v(74.33, -50.04) * mm, "end": v(73.94, -52.04) * mm});
            skLineSegment(sketch, "E603", {"start": v(73.94, -52.04) * mm, "end": v(73.83, -53.68) * mm});
            skLineSegment(sketch, "E604", {"start": v(73.83, -53.68) * mm, "end": v(73.91, -55.83) * mm});
            skLineSegment(sketch, "E605", {"start": v(73.91, -55.83) * mm, "end": v(74.16, -58.41) * mm});
            skLineSegment(sketch, "E606", {"start": v(74.16, -58.41) * mm, "end": v(74.58, -60.18) * mm});
            skLineSegment(sketch, "E607", {"start": v(74.58, -60.18) * mm, "end": v(75.14, -61.63) * mm});
            skLineSegment(sketch, "E608", {"start": v(75.14, -61.63) * mm, "end": v(76, -63.5) * mm});
            skLineSegment(sketch, "E609", {"start": v(76, -63.5) * mm, "end": v(73.91, -63.2) * mm});
            skLineSegment(sketch, "E610", {"start": v(73.91, -63.2) * mm, "end": v(71.03, -62.68) * mm});
            skLineSegment(sketch, "E611", {"start": v(71.03, -62.68) * mm, "end": v(68.73, -62.27) * mm});
            skLineSegment(sketch, "E612", {"start": v(68.73, -62.27) * mm, "end": v(65.93, -61.8) * mm});
            skLineSegment(sketch, "E613", {"start": v(65.93, -61.8) * mm, "end": v(64.4, -61.58) * mm});
            skLineSegment(sketch, "E614", {"start": v(64.4, -61.58) * mm, "end": v(63.03, -61.43) * mm});
            skLineSegment(sketch, "E615", {"start": v(63.03, -61.43) * mm, "end": v(60.42, -61.53) * mm});
            skLineSegment(sketch, "E616", {"start": v(60.42, -61.53) * mm, "end": v(57.47, -62.06) * mm});
            skLineSegment(sketch, "E617", {"start": v(57.47, -62.06) * mm, "end": v(55.25, -62.9) * mm});
            skLineSegment(sketch, "E618", {"start": v(55.25, -62.9) * mm, "end": v(53.19, -64.1) * mm});
            skLineSegment(sketch, "E619", {"start": v(53.19, -64.1) * mm, "end": v(51.17, -65.42) * mm});
            skLineSegment(sketch, "E620", {"start": v(51.17, -65.42) * mm, "end": v(48.51, -67.54) * mm});
            skLineSegment(sketch, "E621", {"start": v(48.51, -67.54) * mm, "end": v(41.83, -73.52) * mm});
            skLineSegment(sketch, "E622", {"start": v(41.83, -73.52) * mm, "end": v(39.43, -75.67) * mm});
            skLineSegment(sketch, "E623", {"start": v(39.43, -75.67) * mm, "end": v(35.87, -78.43) * mm});
            skLineSegment(sketch, "E624", {"start": v(35.87, -78.43) * mm, "end": v(32.77, -80.6) * mm});
            skLineSegment(sketch, "E625", {"start": v(32.77, -80.6) * mm, "end": v(29.69, -82.62) * mm});
            skLineSegment(sketch, "E626", {"start": v(29.69, -82.62) * mm, "end": v(26.05, -84.64) * mm});
            skLineSegment(sketch, "E627", {"start": v(26.05, -84.64) * mm, "end": v(20.93, -86.96) * mm});
            skLineSegment(sketch, "E628", {"start": v(20.93, -86.96) * mm, "end": v(14.73, -89.18) * mm});
            skLineSegment(sketch, "E629", {"start": v(14.73, -89.18) * mm, "end": v(11.96, -89.99) * mm});
            skLineSegment(sketch, "E630", {"start": v(11.96, -89.99) * mm, "end": v(8.81, -90.67) * mm});
            skLineSegment(sketch, "E631", {"start": v(8.81, -90.67) * mm, "end": v(5.18, -91.34) * mm});
            skLineSegment(sketch, "E632", {"start": v(5.18, -91.34) * mm, "end": v(0.46, -92.01) * mm});
            skLineSegment(sketch, "E633", {"start": v(0.46, -92.01) * mm, "end": v(-3.08, -92.14) * mm});
            skLineSegment(sketch, "E634", {"start": v(-3.08, -92.14) * mm, "end": v(-6.33, -92.4) * mm});
            skLineSegment(sketch, "E635", {"start": v(-6.33, -92.4) * mm, "end": v(-12.18, -92.4) * mm});
            skLineSegment(sketch, "E636", {"start": v(-12.18, -92.4) * mm, "end": v(-15.54, -92.13) * mm});
            skLineSegment(sketch, "E637", {"start": v(-15.54, -92.13) * mm, "end": v(-19.15, -91.56) * mm});
            skLineSegment(sketch, "E638", {"start": v(-19.15, -91.56) * mm, "end": v(-24.55, -90.6) * mm});
            skLineSegment(sketch, "E639", {"start": v(-24.55, -90.6) * mm, "end": v(-32.08, -87.98) * mm});
            skLineSegment(sketch, "E640", {"start": v(-32.08, -87.98) * mm, "end": v(-36.83, -86.21) * mm});
            skLineSegment(sketch, "E641", {"start": v(-36.83, -86.21) * mm, "end": v(-40.07, -84.9) * mm});
            skLineSegment(sketch, "E642", {"start": v(-40.07, -84.9) * mm, "end": v(-50.92, -79.88) * mm});
            skLineSegment(sketch, "E643", {"start": v(-50.92, -79.88) * mm, "end": v(-56.52, -76.38) * mm});
            skLineSegment(sketch, "E644", {"start": v(-56.52, -76.38) * mm, "end": v(-62.15, -72.72) * mm});
            skLineSegment(sketch, "E645", {"start": v(-62.15, -72.72) * mm, "end": v(-67.41, -67.93) * mm});
            skLineSegment(sketch, "E646", {"start": v(-67.41, -67.93) * mm, "end": v(-68.95, -66.72) * mm});
            skLineSegment(sketch, "E647", {"start": v(-68.95, -66.72) * mm, "end": v(-71.92, -63.59) * mm});
            skLineSegment(sketch, "E648", {"start": v(-71.92, -63.59) * mm, "end": v(-74.92, -60) * mm});
            skLineSegment(sketch, "E649", {"start": v(-74.92, -60) * mm, "end": v(-77.59, -56.08) * mm});
            skLineSegment(sketch, "E650", {"start": v(-77.59, -56.08) * mm, "end": v(-80.76, -51.44) * mm});
            skLineSegment(sketch, "E651", {"start": v(-80.76, -51.44) * mm, "end": v(-82.41, -48.41) * mm});
            skLineSegment(sketch, "E652", {"start": v(-82.41, -48.41) * mm, "end": v(-84.23, -44.92) * mm});
            skLineSegment(sketch, "E653", {"start": v(-84.23, -44.92) * mm, "end": v(-85.52, -41.88) * mm});
            skLineSegment(sketch, "E654", {"start": v(-85.52, -41.88) * mm, "end": v(-86.53, -38.99) * mm});
            skLineSegment(sketch, "E655", {"start": v(-86.53, -38.99) * mm, "end": v(-87.32, -35.83) * mm});
            skLineSegment(sketch, "E656", {"start": v(-87.32, -35.83) * mm, "end": v(-88.27, -31.9) * mm});
            skLineSegment(sketch, "E657", {"start": v(-88.27, -31.9) * mm, "end": v(-88.92, -28.22) * mm});
            skLineSegment(sketch, "E658", {"start": v(-88.92, -28.22) * mm, "end": v(-89.39, -24.2) * mm});
            skLineSegment(sketch, "E659", {"start": v(-89.39, -24.2) * mm, "end": v(-89.57, -21.38) * mm});
            skLineSegment(sketch, "E660", {"start": v(-89.57, -21.38) * mm, "end": v(-89.57, -16.04) * mm});
            skLineSegment(sketch, "E661", {"start": v(-89.57, -16.04) * mm, "end": v(-89.21, -11.66) * mm});
            skLineSegment(sketch, "E662", {"start": v(-89.21, -11.66) * mm, "end": v(-88.64, -6.68) * mm});
            skLineSegment(sketch, "E663", {"start": v(-88.64, -6.68) * mm, "end": v(-87.84, -2.68) * mm});
            skLineSegment(sketch, "E664", {"start": v(-87.84, -2.68) * mm, "end": v(-86.86, 1.26) * mm});
            skLineSegment(sketch, "E665", {"start": v(-86.86, 1.26) * mm, "end": v(-85.72, 4.9) * mm});
            skLineSegment(sketch, "E666", {"start": v(-85.72, 4.9) * mm, "end": v(-84.55, 8.05) * mm});
            skLineSegment(sketch, "E667", {"start": v(-84.55, 8.05) * mm, "end": v(-83, 11.74) * mm});
            skLineSegment(sketch, "E668", {"start": v(-83, 11.74) * mm, "end": v(-81.4, 15.06) * mm});
            skLineSegment(sketch, "E669", {"start": v(-81.4, 15.06) * mm, "end": v(-79.51, 18.33) * mm});
            skLineSegment(sketch, "E670", {"start": v(-79.51, 18.33) * mm, "end": v(-77.36, 21.6) * mm});
            skLineSegment(sketch, "E671", {"start": v(-77.36, 21.6) * mm, "end": v(-75.1, 24.7) * mm});
            skLineSegment(sketch, "E672", {"start": v(-75.1, 24.7) * mm, "end": v(-72.9, 27.5) * mm});
            skLineSegment(sketch, "E673", {"start": v(-72.9, 27.5) * mm, "end": v(-70.33, 30.35) * mm});
            skLineSegment(sketch, "E674", {"start": v(-70.33, 30.35) * mm, "end": v(-67.26, 33.56) * mm});
            skLineSegment(sketch, "E675", {"start": v(-67.26, 33.56) * mm, "end": v(-64.8, 35.96) * mm});
            skLineSegment(sketch, "E676", {"start": v(-64.8, 35.96) * mm, "end": v(-62.72, 37.88) * mm});
            skLineSegment(sketch, "E677", {"start": v(-62.72, 37.88) * mm, "end": v(-59.55, 40.43) * mm});
            skLineSegment(sketch, "E678", {"start": v(-59.55, 40.43) * mm, "end": v(-55, 43.72) * mm});
            skLineSegment(sketch, "E679", {"start": v(-55, 43.72) * mm, "end": v(-51.63, 45.88) * mm});
            skLineSegment(sketch, "E680", {"start": v(-51.63, 45.88) * mm, "end": v(-48.03, 47.83) * mm});
            skLineSegment(sketch, "E681", {"start": v(-48.03, 47.83) * mm, "end": v(-44.72, 49.48) * mm});
            skLineSegment(sketch, "E682", {"start": v(-44.72, 49.48) * mm, "end": v(-38.56, 52.26) * mm});
            skLineSegment(sketch, "E683", {"start": v(-38.56, 52.26) * mm, "end": v(-34.29, 53.82) * mm});
            skLineSegment(sketch, "E684", {"start": v(-34.29, 53.82) * mm, "end": v(-30.24, 55.19) * mm});
            skLineSegment(sketch, "E685", {"start": v(-30.24, 55.19) * mm, "end": v(-26.3, 56.3) * mm});
            skLineSegment(sketch, "E686", {"start": v(-26.3, 56.3) * mm, "end": v(-21.53, 57.2) * mm});
            skLineSegment(sketch, "E687", {"start": v(-21.53, 57.2) * mm, "end": v(-17.22, 57.7) * mm});
            skLineSegment(sketch, "E688", {"start": v(-17.22, 57.7) * mm, "end": v(-12.73, 58) * mm});
            skLineSegment(sketch, "E689", {"start": v(-12.73, 58) * mm, "end": v(-9.04, 58.1) * mm});
            skLineSegment(sketch, "E690", {"start": v(-9.04, 58.1) * mm, "end": v(-4.9, 57.94) * mm});
            skLineSegment(sketch, "E691", {"start": v(-4.9, 57.94) * mm, "end": v(-0.67, 57.69) * mm});
            skLineSegment(sketch, "E692", {"start": v(-0.67, 57.69) * mm, "end": v(4.03, 57.13) * mm});
            skLineSegment(sketch, "E693", {"start": v(4.03, 57.13) * mm, "end": v(9.44, 56.04) * mm});
            skLineSegment(sketch, "E694", {"start": v(9.44, 56.04) * mm, "end": v(14.54, 54.54) * mm});
            skLineSegment(sketch, "E695", {"start": v(14.54, 54.54) * mm, "end": v(19.58, 52.66) * mm});
            skLineSegment(sketch, "E696", {"start": v(19.58, 52.66) * mm, "end": v(23.68, 50.8) * mm});
            skLineSegment(sketch, "E697", {"start": v(23.68, 50.8) * mm, "end": v(27.9, 48.7) * mm});
            skLineSegment(sketch, "E698", {"start": v(27.9, 48.7) * mm, "end": v(32.25, 46.15) * mm});
            skLineSegment(sketch, "E699", {"start": v(32.25, 46.15) * mm, "end": v(36.81, 43.25) * mm});
            skLineSegment(sketch, "E700", {"start": v(36.81, 43.25) * mm, "end": v(43.46, 38.5) * mm});
            skLineSegment(sketch, "E701", {"start": v(43.46, 38.5) * mm, "end": v(48.03, 34.72) * mm});
            skLineSegment(sketch, "E702", {"start": v(48.03, 34.72) * mm, "end": v(51.6, 31.67) * mm});
            skLineSegment(sketch, "E703", {"start": v(51.6, 31.67) * mm, "end": v(55.8, 28.52) * mm});
            skLineSegment(sketch, "E704", {"start": v(55.8, 28.52) * mm, "end": v(58.5, 27.05) * mm});
            skLineSegment(sketch, "E705", {"start": v(58.5, 27.05) * mm, "end": v(59.71, 26.43) * mm});
            skLineSegment(sketch, "E706", {"start": v(59.71, 26.43) * mm, "end": v(61.34, 25.82) * mm});
            skLineSegment(sketch, "E707", {"start": v(61.34, 25.82) * mm, "end": v(63.28, 25.1) * mm});
            skLineSegment(sketch, "E708", {"start": v(63.28, 25.1) * mm, "end": v(65.16, 24.72) * mm});
            skLineSegment(sketch, "E709", {"start": v(65.16, 24.72) * mm, "end": v(67.64, 24.5) * mm});
            skLineSegment(sketch, "E710", {"start": v(67.64, 24.5) * mm, "end": v(70.8, 24.86) * mm});
            skLineSegment(sketch, "E711", {"start": v(70.8, 24.86) * mm, "end": v(73.65, 25.55) * mm});
            skLineSegment(sketch, "E712", {"start": v(73.65, 25.55) * mm, "end": v(76, 26.7) * mm});
            skLineSegment(sketch, "E713", {"start": v(76, 26.7) * mm, "end": v(77.47, 27.37) * mm});
            skLineSegment(sketch, "E714", {"start": v(91.6, 0.97) * mm, "end": v(89.8, 2.17) * mm});
            skLineSegment(sketch, "E715", {"start": v(89.8, 2.17) * mm, "end": v(88.04, 3.06) * mm});
            skLineSegment(sketch, "E716", {"start": v(88.04, 3.06) * mm, "end": v(85.97, 3.64) * mm});
            skLineSegment(sketch, "E717", {"start": v(85.97, 3.64) * mm, "end": v(81.59, 4.35) * mm});
            skLineSegment(sketch, "E718", {"start": v(81.59, 4.35) * mm, "end": v(78.96, 4.15) * mm});
            skLineSegment(sketch, "E719", {"start": v(78.96, 4.15) * mm, "end": v(76.64, 3.8) * mm});
            skLineSegment(sketch, "E720", {"start": v(76.64, 3.8) * mm, "end": v(74.74, 3.35) * mm});
            skLineSegment(sketch, "E721", {"start": v(74.74, 3.35) * mm, "end": v(72.86, 2.34) * mm});
            skLineSegment(sketch, "E722", {"start": v(72.86, 2.34) * mm, "end": v(71.78, 1.5) * mm});
            skLineSegment(sketch, "E723", {"start": v(71.78, 1.5) * mm, "end": v(70.65, 0.4) * mm});
            skLineSegment(sketch, "E724", {"start": v(70.65, 0.4) * mm, "end": v(69.84, -0.5) * mm});
            skLineSegment(sketch, "E725", {"start": v(69.84, -0.5) * mm, "end": v(68.88, -1.92) * mm});
            skLineSegment(sketch, "E726", {"start": v(68.88, -1.92) * mm, "end": v(68.09, -4.05) * mm});
            skLineSegment(sketch, "E727", {"start": v(68.09, -4.05) * mm, "end": v(67.2, -6.4) * mm});
            skLineSegment(sketch, "E728", {"start": v(67.2, -6.4) * mm, "end": v(66.35, -10.69) * mm});
            skLineSegment(sketch, "E729", {"start": v(66.35, -10.69) * mm, "end": v(65.98, -14.8) * mm});
            skLineSegment(sketch, "E730", {"start": v(65.98, -14.8) * mm, "end": v(65.82, -19.13) * mm});
            skLineSegment(sketch, "E731", {"start": v(65.82, -19.13) * mm, "end": v(65.54, -22.14) * mm});
            skLineSegment(sketch, "E732", {"start": v(65.54, -22.14) * mm, "end": v(64.36, -27.1) * mm});
            skLineSegment(sketch, "E733", {"start": v(64.36, -27.1) * mm, "end": v(63.13, -30.97) * mm});
            skLineSegment(sketch, "E734", {"start": v(63.13, -30.97) * mm, "end": v(61.58, -34.15) * mm});
            skLineSegment(sketch, "E735", {"start": v(61.58, -34.15) * mm, "end": v(60.38, -36.4) * mm});
            skLineSegment(sketch, "E736", {"start": v(60.38, -36.4) * mm, "end": v(59.02, -38.46) * mm});
            skLineSegment(sketch, "E737", {"start": v(59.02, -38.46) * mm, "end": v(58.02, -39.9) * mm});
            skLineSegment(sketch, "E738", {"start": v(58.02, -39.9) * mm, "end": v(56.57, -41.74) * mm});
            skLineSegment(sketch, "E739", {"start": v(56.57, -41.74) * mm, "end": v(48.73, -49.36) * mm});
            skLineSegment(sketch, "E740", {"start": v(48.73, -49.36) * mm, "end": v(41.83, -55.16) * mm});
            skLineSegment(sketch, "E741", {"start": v(41.83, -55.16) * mm, "end": v(35.56, -60.1) * mm});
            skLineSegment(sketch, "E742", {"start": v(35.56, -60.1) * mm, "end": v(29.09, -63.63) * mm});
            skLineSegment(sketch, "E743", {"start": v(29.09, -63.63) * mm, "end": v(22.93, -65.86) * mm});
            skLineSegment(sketch, "E744", {"start": v(22.93, -65.86) * mm, "end": v(8.6, -69.97) * mm});
            skLineSegment(sketch, "E745", {"start": v(8.6, -69.97) * mm, "end": v(3.8, -70.83) * mm});
            skLineSegment(sketch, "E746", {"start": v(3.8, -70.83) * mm, "end": v(-1.55, -71.34) * mm});
            skLineSegment(sketch, "E747", {"start": v(-1.55, -71.34) * mm, "end": v(-6.18, -71.14) * mm});
            skLineSegment(sketch, "E748", {"start": v(-6.18, -71.14) * mm, "end": v(-11.35, -70.56) * mm});
            skLineSegment(sketch, "E749", {"start": v(-11.35, -70.56) * mm, "end": v(-20.86, -69.22) * mm});
            skLineSegment(sketch, "E750", {"start": v(-20.86, -69.22) * mm, "end": v(-27.8, -67.83) * mm});
            skLineSegment(sketch, "E751", {"start": v(-27.8, -67.83) * mm, "end": v(-30.73, -66.92) * mm});
            skLineSegment(sketch, "E752", {"start": v(-30.73, -66.92) * mm, "end": v(-35.71, -65.06) * mm});
            skLineSegment(sketch, "E753", {"start": v(-35.71, -65.06) * mm, "end": v(-39.87, -63.1) * mm});
            skLineSegment(sketch, "E754", {"start": v(-39.87, -63.1) * mm, "end": v(-46.33, -59.67) * mm});
            skLineSegment(sketch, "E755", {"start": v(-46.33, -59.67) * mm, "end": v(-50.37, -56.6) * mm});
            skLineSegment(sketch, "E756", {"start": v(-50.37, -56.6) * mm, "end": v(-54.95, -52.43) * mm});
            skLineSegment(sketch, "E757", {"start": v(-54.95, -52.43) * mm, "end": v(-57.27, -49.5) * mm});
            skLineSegment(sketch, "E758", {"start": v(-57.27, -49.5) * mm, "end": v(-61.18, -44.22) * mm});
            skLineSegment(sketch, "E759", {"start": v(-61.18, -44.22) * mm, "end": v(-64.28, -38.87) * mm});
            skLineSegment(sketch, "E760", {"start": v(-64.28, -38.87) * mm, "end": v(-67.37, -31.1) * mm});
            skLineSegment(sketch, "E761", {"start": v(-67.37, -31.1) * mm, "end": v(-68.5, -26.46) * mm});
            skLineSegment(sketch, "E762", {"start": v(-68.5, -26.46) * mm, "end": v(-69.21, -22.44) * mm});
            skLineSegment(sketch, "E763", {"start": v(-69.21, -22.44) * mm, "end": v(-69.38, -19.3) * mm});
            skLineSegment(sketch, "E764", {"start": v(-69.38, -19.3) * mm, "end": v(-69.38, -15.38) * mm});
            skLineSegment(sketch, "E765", {"start": v(-69.38, -15.38) * mm, "end": v(-69.2, -11.4) * mm});
            skLineSegment(sketch, "E766", {"start": v(-69.2, -11.4) * mm, "end": v(-69.06, -9.84) * mm});
            skLineSegment(sketch, "E767", {"start": v(-69.06, -9.84) * mm, "end": v(-68.34, -6.27) * mm});
            skLineSegment(sketch, "E768", {"start": v(-68.34, -6.27) * mm, "end": v(-67.32, -2.56) * mm});
            skLineSegment(sketch, "E769", {"start": v(-67.32, -2.56) * mm, "end": v(-65.48, 2.32) * mm});
            skLineSegment(sketch, "E770", {"start": v(-65.48, 2.32) * mm, "end": v(-62.97, 7.5) * mm});
            skLineSegment(sketch, "E771", {"start": v(-62.97, 7.5) * mm, "end": v(-60.23, 11.73) * mm});
            skLineSegment(sketch, "E772", {"start": v(-60.23, 11.73) * mm, "end": v(-56.96, 15.87) * mm});
            skLineSegment(sketch, "E773", {"start": v(-56.96, 15.87) * mm, "end": v(-53.42, 19.57) * mm});
            skLineSegment(sketch, "E774", {"start": v(-53.42, 19.57) * mm, "end": v(-49.16, 23.13) * mm});
            skLineSegment(sketch, "E775", {"start": v(-49.16, 23.13) * mm, "end": v(-44.82, 25.8) * mm});
            skLineSegment(sketch, "E776", {"start": v(-44.82, 25.8) * mm, "end": v(-39.67, 28.41) * mm});
            skLineSegment(sketch, "E777", {"start": v(-39.67, 28.41) * mm, "end": v(-34.2, 30.76) * mm});
            skLineSegment(sketch, "E778", {"start": v(-34.2, 30.76) * mm, "end": v(-27.36, 33.02) * mm});
            skLineSegment(sketch, "E779", {"start": v(-27.36, 33.02) * mm, "end": v(-20.5, 34.39) * mm});
            skLineSegment(sketch, "E780", {"start": v(-20.5, 34.39) * mm, "end": v(-12.77, 35.48) * mm});
            skLineSegment(sketch, "E781", {"start": v(-12.77, 35.48) * mm, "end": v(-6.95, 36.21) * mm});
            skLineSegment(sketch, "E782", {"start": v(-6.95, 36.21) * mm, "end": v(-3.73, 36.27) * mm});
            skLineSegment(sketch, "E783", {"start": v(-3.73, 36.27) * mm, "end": v(0.6, 36.18) * mm});
            skLineSegment(sketch, "E784", {"start": v(0.6, 36.18) * mm, "end": v(5.13, 35.83) * mm});
            skLineSegment(sketch, "E785", {"start": v(5.13, 35.83) * mm, "end": v(9.29, 34.9) * mm});
            skLineSegment(sketch, "E786", {"start": v(9.29, 34.9) * mm, "end": v(13.44, 33.78) * mm});
            skLineSegment(sketch, "E787", {"start": v(13.44, 33.78) * mm, "end": v(18.99, 32) * mm});
            skLineSegment(sketch, "E788", {"start": v(18.99, 32) * mm, "end": v(24.93, 29.63) * mm});
            skLineSegment(sketch, "E789", {"start": v(24.93, 29.63) * mm, "end": v(30.3, 26.94) * mm});
            skLineSegment(sketch, "E790", {"start": v(30.3, 26.94) * mm, "end": v(33.96, 25.06) * mm});
            skLineSegment(sketch, "E791", {"start": v(33.96, 25.06) * mm, "end": v(37.76, 22.41) * mm});
            skLineSegment(sketch, "E792", {"start": v(37.76, 22.41) * mm, "end": v(40.93, 20.22) * mm});
            skLineSegment(sketch, "E793", {"start": v(40.93, 20.22) * mm, "end": v(42.99, 19.1) * mm});
            skLineSegment(sketch, "E794", {"start": v(42.99, 19.1) * mm, "end": v(44.87, 18.38) * mm});
            skLineSegment(sketch, "E795", {"start": v(44.87, 18.38) * mm, "end": v(47.2, 17.49) * mm});
            skLineSegment(sketch, "E796", {"start": v(47.2, 17.49) * mm, "end": v(50.41, 16.37) * mm});
            skLineSegment(sketch, "E797", {"start": v(50.41, 16.37) * mm, "end": v(52.83, 15.83) * mm});
            skLineSegment(sketch, "E798", {"start": v(52.83, 15.83) * mm, "end": v(54.52, 15.69) * mm});
            skLineSegment(sketch, "E799", {"start": v(54.52, 15.69) * mm, "end": v(56.38, 15.73) * mm});
            skLineSegment(sketch, "E800", {"start": v(56.38, 15.73) * mm, "end": v(59.33, 16.23) * mm});
            skLineSegment(sketch, "E801", {"start": v(59.33, 16.23) * mm, "end": v(61.4, 16.97) * mm});
            skLineSegment(sketch, "E802", {"start": v(61.4, 16.97) * mm, "end": v(63.34, 18.03) * mm});
            skLineSegment(sketch, "E803", {"start": v(63.34, 18.03) * mm, "end": v(64.85, 19.1) * mm});
            skLineSegment(sketch, "E804", {"start": v(64.85, 19.1) * mm, "end": v(66.77, 20.7) * mm});
            skLineSegment(sketch, "E805", {"start": v(66.77, 20.7) * mm, "end": v(68.4, 22.39) * mm});
            skLineSegment(sketch, "E806", {"start": v(68.4, 22.39) * mm, "end": v(70.32, 24.8) * mm});
            skLineSegment(sketch, "E807", {"start": v(62.01, -10.5) * mm, "end": v(62.27, -12.92) * mm});
            skLineSegment(sketch, "E808", {"start": v(62.27, -12.92) * mm, "end": v(62.26, -15.84) * mm});
            skLineSegment(sketch, "E809", {"start": v(62.26, -15.84) * mm, "end": v(62, -18.39) * mm});
            skLineSegment(sketch, "E810", {"start": v(62, -18.39) * mm, "end": v(61.52, -21.19) * mm});
            skLineSegment(sketch, "E811", {"start": v(61.52, -21.19) * mm, "end": v(60.38, -25.45) * mm});
            skLineSegment(sketch, "E812", {"start": v(60.38, -25.45) * mm, "end": v(58.79, -30.06) * mm});
            skLineSegment(sketch, "E813", {"start": v(58.79, -30.06) * mm, "end": v(56.5, -34.84) * mm});
            skLineSegment(sketch, "E814", {"start": v(56.5, -34.84) * mm, "end": v(52.95, -40.54) * mm});
            skLineSegment(sketch, "E815", {"start": v(52.95, -40.54) * mm, "end": v(49.34, -44.58) * mm});
            skLineSegment(sketch, "E816", {"start": v(49.34, -44.58) * mm, "end": v(43.57, -49.97) * mm});
            skLineSegment(sketch, "E817", {"start": v(43.57, -49.97) * mm, "end": v(40.9, -52.26) * mm});
            skLineSegment(sketch, "E818", {"start": v(40.9, -52.26) * mm, "end": v(36.95, -55.2) * mm});
            skLineSegment(sketch, "E819", {"start": v(36.95, -55.2) * mm, "end": v(32.96, -57.6) * mm});
            skLineSegment(sketch, "E820", {"start": v(32.96, -57.6) * mm, "end": v(27.2, -60.43) * mm});
            skLineSegment(sketch, "E821", {"start": v(27.2, -60.43) * mm, "end": v(15.8, -64.2) * mm});
            skLineSegment(sketch, "E822", {"start": v(15.8, -64.2) * mm, "end": v(8.49, -66.42) * mm});
            skLineSegment(sketch, "E823", {"start": v(8.49, -66.42) * mm, "end": v(6.24, -66.96) * mm});
            skLineSegment(sketch, "E824", {"start": v(6.24, -66.96) * mm, "end": v(2.16, -67.51) * mm});
            skLineSegment(sketch, "E825", {"start": v(2.16, -67.51) * mm, "end": v(-1.92, -67.8) * mm});
            skLineSegment(sketch, "E826", {"start": v(-1.92, -67.8) * mm, "end": v(-6.47, -67.72) * mm});
            skLineSegment(sketch, "E827", {"start": v(-6.47, -67.72) * mm, "end": v(-12.33, -66.78) * mm});
            skLineSegment(sketch, "E828", {"start": v(-12.33, -66.78) * mm, "end": v(-25.9, -64.58) * mm});
            skLineSegment(sketch, "E829", {"start": v(-25.9, -64.58) * mm, "end": v(-28.61, -63.8) * mm});
            skLineSegment(sketch, "E830", {"start": v(-28.61, -63.8) * mm, "end": v(-31.84, -62.75) * mm});
            skLineSegment(sketch, "E831", {"start": v(-31.84, -62.75) * mm, "end": v(-36.32, -60.82) * mm});
            skLineSegment(sketch, "E832", {"start": v(-36.32, -60.82) * mm, "end": v(-41.13, -58.29) * mm});
            skLineSegment(sketch, "E833", {"start": v(-41.13, -58.29) * mm, "end": v(-45.71, -55.62) * mm});
            skLineSegment(sketch, "E834", {"start": v(-45.71, -55.62) * mm, "end": v(-51.33, -50.92) * mm});
            skLineSegment(sketch, "E835", {"start": v(-51.33, -50.92) * mm, "end": v(-54.57, -47.07) * mm});
            skLineSegment(sketch, "E836", {"start": v(-54.57, -47.07) * mm, "end": v(-57.09, -43.76) * mm});
            skLineSegment(sketch, "E837", {"start": v(-57.09, -43.76) * mm, "end": v(-59.87, -39.2) * mm});
            skLineSegment(sketch, "E838", {"start": v(-59.87, -39.2) * mm, "end": v(-62.26, -34.23) * mm});
            skLineSegment(sketch, "E839", {"start": v(-62.26, -34.23) * mm, "end": v(-64.06, -29.29) * mm});
            skLineSegment(sketch, "E840", {"start": v(-64.06, -29.29) * mm, "end": v(-65.12, -24.98) * mm});
            skLineSegment(sketch, "E841", {"start": v(-65.12, -24.98) * mm, "end": v(-65.59, -21.86) * mm});
            skLineSegment(sketch, "E842", {"start": v(-65.59, -21.86) * mm, "end": v(-65.85, -18.94) * mm});
            skLineSegment(sketch, "E843", {"start": v(-65.85, -18.94) * mm, "end": v(-65.85, -14.45) * mm});
            skLineSegment(sketch, "E844", {"start": v(-65.85, -14.45) * mm, "end": v(-65.41, -10.84) * mm});
            skLineSegment(sketch, "E845", {"start": v(-65.41, -10.84) * mm, "end": v(-64.66, -6.64) * mm});
            skLineSegment(sketch, "E846", {"start": v(-64.66, -6.64) * mm, "end": v(-63.38, -2.69) * mm});
            skLineSegment(sketch, "E847", {"start": v(-63.38, -2.69) * mm, "end": v(-61.18, 2.8) * mm});
            skLineSegment(sketch, "E848", {"start": v(-61.18, 2.8) * mm, "end": v(-58.94, 6.6) * mm});
            skLineSegment(sketch, "E849", {"start": v(-58.94, 6.6) * mm, "end": v(-55.4, 11.85) * mm});
            skLineSegment(sketch, "E850", {"start": v(-55.4, 11.85) * mm, "end": v(-53.08, 14.61) * mm});
            skLineSegment(sketch, "E851", {"start": v(-53.08, 14.61) * mm, "end": v(-50.01, 17.72) * mm});
            skLineSegment(sketch, "E852", {"start": v(-50.01, 17.72) * mm, "end": v(-46.47, 20.27) * mm});
            skLineSegment(sketch, "E853", {"start": v(-46.47, 20.27) * mm, "end": v(-41.49, 23.3) * mm});
            skLineSegment(sketch, "E854", {"start": v(-41.49, 23.3) * mm, "end": v(-37.92, 25.2) * mm});
            skLineSegment(sketch, "E855", {"start": v(-37.92, 25.2) * mm, "end": v(-33.16, 27.33) * mm});
            skLineSegment(sketch, "E856", {"start": v(-33.16, 27.33) * mm, "end": v(-28.37, 29) * mm});
            skLineSegment(sketch, "E857", {"start": v(-28.37, 29) * mm, "end": v(-24.4, 29.97) * mm});
            skLineSegment(sketch, "E858", {"start": v(-24.4, 29.97) * mm, "end": v(-18.52, 30.91) * mm});
            skLineSegment(sketch, "E859", {"start": v(-18.52, 30.91) * mm, "end": v(-7.56, 32.4) * mm});
            skLineSegment(sketch, "E860", {"start": v(-7.56, 32.4) * mm, "end": v(-4.4, 32.6) * mm});
            skLineSegment(sketch, "E861", {"start": v(-4.4, 32.6) * mm, "end": v(1.3, 32.4) * mm});
            skLineSegment(sketch, "E862", {"start": v(1.3, 32.4) * mm, "end": v(3.95, 32.13) * mm});
            skLineSegment(sketch, "E863", {"start": v(3.95, 32.13) * mm, "end": v(7.73, 31.58) * mm});
            skLineSegment(sketch, "E864", {"start": v(7.73, 31.58) * mm, "end": v(10.7, 30.86) * mm});
            skLineSegment(sketch, "E865", {"start": v(10.7, 30.86) * mm, "end": v(14.6, 29.7) * mm});
            skLineSegment(sketch, "E866", {"start": v(14.6, 29.7) * mm, "end": v(16.76, 29) * mm});
            skLineSegment(sketch, "E867", {"start": v(16.76, 29) * mm, "end": v(20.52, 27.6) * mm});
            skLineSegment(sketch, "E868", {"start": v(20.52, 27.6) * mm, "end": v(25.7, 25.28) * mm});
            skLineSegment(sketch, "E869", {"start": v(25.7, 25.28) * mm, "end": v(28.72, 23.69) * mm});
            skLineSegment(sketch, "E870", {"start": v(28.72, 23.69) * mm, "end": v(33.12, 21.3) * mm});
            skLineSegment(sketch, "E871", {"start": v(33.12, 21.3) * mm, "end": v(37.78, 18.47) * mm});
            skLineSegment(sketch, "E872", {"start": v(37.78, 18.47) * mm, "end": v(42.79, 15.24) * mm});
            skLineSegment(sketch, "E873", {"start": v(42.79, 15.24) * mm, "end": v(47.29, 12.23) * mm});
            skLineSegment(sketch, "E874", {"start": v(47.29, 12.23) * mm, "end": v(50.12, 10.15) * mm});
            skLineSegment(sketch, "E875", {"start": v(50.12, 10.15) * mm, "end": v(51.52, 9.01) * mm});
            skLineSegment(sketch, "E876", {"start": v(51.52, 9.01) * mm, "end": v(53.04, 7.55) * mm});
            skLineSegment(sketch, "E877", {"start": v(53.04, 7.55) * mm, "end": v(55.12, 5.23) * mm});
            skLineSegment(sketch, "E878", {"start": v(55.12, 5.23) * mm, "end": v(56.7, 3.03) * mm});
            skLineSegment(sketch, "E879", {"start": v(56.7, 3.03) * mm, "end": v(58.8, -0.5) * mm});
            skLineSegment(sketch, "E880", {"start": v(58.8, -0.5) * mm, "end": v(60.44, -4.2) * mm});
            skLineSegment(sketch, "E881", {"start": v(60.44, -4.2) * mm, "end": v(61.38, -7.36) * mm});
            skLineSegment(sketch, "E882", {"start": v(61.38, -7.36) * mm, "end": v(62.01, -10.5) * mm});
            skLineSegment(sketch, "E883", {"start": v(57.26, -11.1) * mm, "end": v(57.7, -14.9) * mm});
            skLineSegment(sketch, "E884", {"start": v(57.7, -14.9) * mm, "end": v(57.87, -17.57) * mm});
            skLineSegment(sketch, "E885", {"start": v(57.87, -17.57) * mm, "end": v(57.24, -21.8) * mm});
            skLineSegment(sketch, "E886", {"start": v(57.24, -21.8) * mm, "end": v(56.49, -24.83) * mm});
            skLineSegment(sketch, "E887", {"start": v(56.49, -24.83) * mm, "end": v(55.47, -28.78) * mm});
            skLineSegment(sketch, "E888", {"start": v(55.47, -28.78) * mm, "end": v(54.05, -32.48) * mm});
            skLineSegment(sketch, "E889", {"start": v(54.05, -32.48) * mm, "end": v(52.34, -35.72) * mm});
            skLineSegment(sketch, "E890", {"start": v(52.34, -35.72) * mm, "end": v(50.13, -38.9) * mm});
            skLineSegment(sketch, "E891", {"start": v(50.13, -38.9) * mm, "end": v(45.87, -43.91) * mm});
            skLineSegment(sketch, "E892", {"start": v(45.87, -43.91) * mm, "end": v(42.78, -47) * mm});
            skLineSegment(sketch, "E893", {"start": v(42.78, -47) * mm, "end": v(39.52, -49.75) * mm});
            skLineSegment(sketch, "E894", {"start": v(39.52, -49.75) * mm, "end": v(36.52, -51.9) * mm});
            skLineSegment(sketch, "E895", {"start": v(36.52, -51.9) * mm, "end": v(33.24, -53.78) * mm});
            skLineSegment(sketch, "E896", {"start": v(33.24, -53.78) * mm, "end": v(29.46, -55.76) * mm});
            skLineSegment(sketch, "E897", {"start": v(29.46, -55.76) * mm, "end": v(27.12, -57.03) * mm});
            skLineSegment(sketch, "E898", {"start": v(27.12, -57.03) * mm, "end": v(23.26, -58.53) * mm});
            skLineSegment(sketch, "E899", {"start": v(23.26, -58.53) * mm, "end": v(18.1, -60.23) * mm});
            skLineSegment(sketch, "E900", {"start": v(18.1, -60.23) * mm, "end": v(14.63, -61.49) * mm});
            skLineSegment(sketch, "E901", {"start": v(14.63, -61.49) * mm, "end": v(9.9, -62.94) * mm});
            skLineSegment(sketch, "E902", {"start": v(9.9, -62.94) * mm, "end": v(5.85, -63.75) * mm});
            skLineSegment(sketch, "E903", {"start": v(5.85, -63.75) * mm, "end": v(0.69, -64.43) * mm});
            skLineSegment(sketch, "E904", {"start": v(0.69, -64.43) * mm, "end": v(-1.63, -64.58) * mm});
            skLineSegment(sketch, "E905", {"start": v(-1.63, -64.58) * mm, "end": v(-5.35, -64.55) * mm});
            skLineSegment(sketch, "E906", {"start": v(-5.35, -64.55) * mm, "end": v(-7.37, -64.48) * mm});
            skLineSegment(sketch, "E907", {"start": v(-7.37, -64.48) * mm, "end": v(-10.84, -63.98) * mm});
            skLineSegment(sketch, "E908", {"start": v(-10.84, -63.98) * mm, "end": v(-16.56, -63.17) * mm});
            skLineSegment(sketch, "E909", {"start": v(-16.56, -63.17) * mm, "end": v(-21.5, -62.29) * mm});
            skLineSegment(sketch, "E910", {"start": v(-21.5, -62.29) * mm, "end": v(-25.7, -61.39) * mm});
            skLineSegment(sketch, "E911", {"start": v(-25.7, -61.39) * mm, "end": v(-29.04, -60.4) * mm});
            skLineSegment(sketch, "E912", {"start": v(-29.04, -60.4) * mm, "end": v(-31.69, -59.33) * mm});
            skLineSegment(sketch, "E913", {"start": v(-31.69, -59.33) * mm, "end": v(-35.05, -57.8) * mm});
            skLineSegment(sketch, "E914", {"start": v(-35.05, -57.8) * mm, "end": v(-37.9, -56.16) * mm});
            skLineSegment(sketch, "E915", {"start": v(-37.9, -56.16) * mm, "end": v(-40.12, -54.9) * mm});
            skLineSegment(sketch, "E916", {"start": v(-40.12, -54.9) * mm, "end": v(-42.6, -53.3) * mm});
            skLineSegment(sketch, "E917", {"start": v(-42.6, -53.3) * mm, "end": v(-46.33, -50.59) * mm});
            skLineSegment(sketch, "E918", {"start": v(-46.33, -50.59) * mm, "end": v(-49.71, -47.45) * mm});
            skLineSegment(sketch, "E919", {"start": v(-49.71, -47.45) * mm, "end": v(-52.04, -44.62) * mm});
            skLineSegment(sketch, "E920", {"start": v(-52.04, -44.62) * mm, "end": v(-54, -41.94) * mm});
            skLineSegment(sketch, "E921", {"start": v(-54, -41.94) * mm, "end": v(-56.21, -38.2) * mm});
            skLineSegment(sketch, "E922", {"start": v(-56.21, -38.2) * mm, "end": v(-57.88, -34.73) * mm});
            skLineSegment(sketch, "E923", {"start": v(-57.88, -34.73) * mm, "end": v(-59.15, -31.71) * mm});
            skLineSegment(sketch, "E924", {"start": v(-59.15, -31.71) * mm, "end": v(-60.66, -27.28) * mm});
            skLineSegment(sketch, "E925", {"start": v(-60.66, -27.28) * mm, "end": v(-61.65, -23.07) * mm});
            skLineSegment(sketch, "E926", {"start": v(-61.65, -23.07) * mm, "end": v(-61.97, -20.16) * mm});
            skLineSegment(sketch, "E927", {"start": v(-61.97, -20.16) * mm, "end": v(-62.14, -17.56) * mm});
            skLineSegment(sketch, "E928", {"start": v(-62.14, -17.56) * mm, "end": v(-61.96, -13.92) * mm});
            skLineSegment(sketch, "E929", {"start": v(-61.96, -13.92) * mm, "end": v(-61.64, -10.82) * mm});
            skLineSegment(sketch, "E930", {"start": v(-61.64, -10.82) * mm, "end": v(-60.5, -6.06) * mm});
            skLineSegment(sketch, "E931", {"start": v(-60.5, -6.06) * mm, "end": v(-59.69, -3.57) * mm});
            skLineSegment(sketch, "E932", {"start": v(-59.69, -3.57) * mm, "end": v(-57.76, 0.96) * mm});
            skLineSegment(sketch, "E933", {"start": v(-57.76, 0.96) * mm, "end": v(-56.35, 3.62) * mm});
            skLineSegment(sketch, "E934", {"start": v(-56.35, 3.62) * mm, "end": v(-54.4, 7.04) * mm});
            skLineSegment(sketch, "E935", {"start": v(-54.4, 7.04) * mm, "end": v(-52.94, 9.14) * mm});
            skLineSegment(sketch, "E936", {"start": v(-52.94, 9.14) * mm, "end": v(-50.97, 11.6) * mm});
            skLineSegment(sketch, "E937", {"start": v(-50.97, 11.6) * mm, "end": v(-49.04, 13.61) * mm});
            skLineSegment(sketch, "E938", {"start": v(-49.04, 13.61) * mm, "end": v(-47.96, 14.62) * mm});
            skLineSegment(sketch, "E939", {"start": v(-47.96, 14.62) * mm, "end": v(-45.71, 16.45) * mm});
            skLineSegment(sketch, "E940", {"start": v(-45.71, 16.45) * mm, "end": v(-43.41, 18.1) * mm});
            skLineSegment(sketch, "E941", {"start": v(-43.41, 18.1) * mm, "end": v(-41.32, 19.45) * mm});
            skLineSegment(sketch, "E942", {"start": v(-41.32, 19.45) * mm, "end": v(-37.4, 21.73) * mm});
            skLineSegment(sketch, "E943", {"start": v(-37.4, 21.73) * mm, "end": v(-34.09, 23.47) * mm});
            skLineSegment(sketch, "E944", {"start": v(-34.09, 23.47) * mm, "end": v(-30.96, 24.83) * mm});
            skLineSegment(sketch, "E945", {"start": v(-30.96, 24.83) * mm, "end": v(-28.25, 25.76) * mm});
            skLineSegment(sketch, "E946", {"start": v(-28.25, 25.76) * mm, "end": v(-25.18, 26.62) * mm});
            skLineSegment(sketch, "E947", {"start": v(-25.18, 26.62) * mm, "end": v(-22.45, 27.17) * mm});
            skLineSegment(sketch, "E948", {"start": v(-22.45, 27.17) * mm, "end": v(-19.67, 27.7) * mm});
            skLineSegment(sketch, "E949", {"start": v(-19.67, 27.7) * mm, "end": v(-17.28, 28.18) * mm});
            skLineSegment(sketch, "E950", {"start": v(-17.28, 28.18) * mm, "end": v(-13.65, 28.7) * mm});
            skLineSegment(sketch, "E951", {"start": v(-13.65, 28.7) * mm, "end": v(-8.65, 29.4) * mm});
            skLineSegment(sketch, "E952", {"start": v(-8.65, 29.4) * mm, "end": v(-5.37, 29.61) * mm});
            skLineSegment(sketch, "E953", {"start": v(-5.37, 29.61) * mm, "end": v(-0.94, 29.61) * mm});
            skLineSegment(sketch, "E954", {"start": v(-0.94, 29.61) * mm, "end": v(2.46, 29.37) * mm});
            skLineSegment(sketch, "E955", {"start": v(2.46, 29.37) * mm, "end": v(6.33, 28.82) * mm});
            skLineSegment(sketch, "E956", {"start": v(6.33, 28.82) * mm, "end": v(9.94, 27.98) * mm});
            skLineSegment(sketch, "E957", {"start": v(9.94, 27.98) * mm, "end": v(13.6, 26.96) * mm});
            skLineSegment(sketch, "E958", {"start": v(13.6, 26.96) * mm, "end": v(16.94, 25.76) * mm});
            skLineSegment(sketch, "E959", {"start": v(16.94, 25.76) * mm, "end": v(20.27, 24.43) * mm});
            skLineSegment(sketch, "E960", {"start": v(20.27, 24.43) * mm, "end": v(22.91, 23.27) * mm});
            skLineSegment(sketch, "E961", {"start": v(22.91, 23.27) * mm, "end": v(26.53, 21.4) * mm});
            skLineSegment(sketch, "E962", {"start": v(26.53, 21.4) * mm, "end": v(30.32, 19.27) * mm});
            skLineSegment(sketch, "E963", {"start": v(30.32, 19.27) * mm, "end": v(35.8, 16.26) * mm});
            skLineSegment(sketch, "E964", {"start": v(35.8, 16.26) * mm, "end": v(39.46, 14.2) * mm});
            skLineSegment(sketch, "E965", {"start": v(39.46, 14.2) * mm, "end": v(41.27, 12.94) * mm});
            skLineSegment(sketch, "E966", {"start": v(41.27, 12.94) * mm, "end": v(43.45, 11.28) * mm});
            skLineSegment(sketch, "E967", {"start": v(43.45, 11.28) * mm, "end": v(45.85, 9.03) * mm});
            skLineSegment(sketch, "E968", {"start": v(45.85, 9.03) * mm, "end": v(48.82, 6.04) * mm});
            skLineSegment(sketch, "E969", {"start": v(48.82, 6.04) * mm, "end": v(50.57, 4.08) * mm});
            skLineSegment(sketch, "E970", {"start": v(50.57, 4.08) * mm, "end": v(51.46, 2.92) * mm});
            skLineSegment(sketch, "E971", {"start": v(51.46, 2.92) * mm, "end": v(53.02, 0.55) * mm});
            skLineSegment(sketch, "E972", {"start": v(53.02, 0.55) * mm, "end": v(53.86, -1.11) * mm});
            skLineSegment(sketch, "E973", {"start": v(53.86, -1.11) * mm, "end": v(55.21, -4.12) * mm});
            skLineSegment(sketch, "E974", {"start": v(55.21, -4.12) * mm, "end": v(56.1, -6.75) * mm});
            skLineSegment(sketch, "E975", {"start": v(56.1, -6.75) * mm, "end": v(56.78, -9.14) * mm});
            skLineSegment(sketch, "E976", {"start": v(56.78, -9.14) * mm, "end": v(57.26, -11.1) * mm});
            skLineSegment(sketch, "E977", {"start": v(53.82, -17.48) * mm, "end": v(53.5, -20.82) * mm});
            skLineSegment(sketch, "E978", {"start": v(53.5, -20.82) * mm, "end": v(52.72, -24.22) * mm});
            skLineSegment(sketch, "E979", {"start": v(52.72, -24.22) * mm, "end": v(51.6, -28.57) * mm});
            skLineSegment(sketch, "E980", {"start": v(51.6, -28.57) * mm, "end": v(49.2, -33.19) * mm});
            skLineSegment(sketch, "E981", {"start": v(49.2, -33.19) * mm, "end": v(46.93, -36.64) * mm});
            skLineSegment(sketch, "E982", {"start": v(46.93, -36.64) * mm, "end": v(44.66, -40.36) * mm});
            skLineSegment(sketch, "E983", {"start": v(44.66, -40.36) * mm, "end": v(41.46, -44.06) * mm});
            skLineSegment(sketch, "E984", {"start": v(41.46, -44.06) * mm, "end": v(38, -47.27) * mm});
            skLineSegment(sketch, "E985", {"start": v(38, -47.27) * mm, "end": v(34.85, -49.47) * mm});
            skLineSegment(sketch, "E986", {"start": v(34.85, -49.47) * mm, "end": v(31.42, -51.7) * mm});
            skLineSegment(sketch, "E987", {"start": v(31.42, -51.7) * mm, "end": v(25.9, -54.5) * mm});
            skLineSegment(sketch, "E988", {"start": v(25.9, -54.5) * mm, "end": v(18.77, -57.07) * mm});
            skLineSegment(sketch, "E989", {"start": v(18.77, -57.07) * mm, "end": v(11.48, -59.36) * mm});
            skLineSegment(sketch, "E990", {"start": v(11.48, -59.36) * mm, "end": v(6.23, -60.42) * mm});
            skLineSegment(sketch, "E991", {"start": v(6.23, -60.42) * mm, "end": v(0.6, -61.25) * mm});
            skLineSegment(sketch, "E992", {"start": v(0.6, -61.25) * mm, "end": v(-4.4, -61.25) * mm});
            skLineSegment(sketch, "E993", {"start": v(-4.4, -61.25) * mm, "end": v(-8.84, -61.09) * mm});
            skLineSegment(sketch, "E994", {"start": v(-8.84, -61.09) * mm, "end": v(-14.38, -60.1) * mm});
            skLineSegment(sketch, "E995", {"start": v(-14.38, -60.1) * mm, "end": v(-20.73, -58.97) * mm});
            skLineSegment(sketch, "E996", {"start": v(-20.73, -58.97) * mm, "end": v(-25.65, -58) * mm});
            skLineSegment(sketch, "E997", {"start": v(-25.65, -58) * mm, "end": v(-30.46, -56.76) * mm});
            skLineSegment(sketch, "E998", {"start": v(-30.46, -56.76) * mm, "end": v(-36.02, -53.82) * mm});
            skLineSegment(sketch, "E999", {"start": v(-36.02, -53.82) * mm, "end": v(-39.45, -51.58) * mm});
            skLineSegment(sketch, "E1000", {"start": v(-39.45, -51.58) * mm, "end": v(-42.31, -49.58) * mm});
            skLineSegment(sketch, "E1001", {"start": v(-42.31, -49.58) * mm, "end": v(-46.27, -46.17) * mm});
            skLineSegment(sketch, "E1002", {"start": v(-46.27, -46.17) * mm, "end": v(-50.23, -41.52) * mm});
            skLineSegment(sketch, "E1003", {"start": v(-50.23, -41.52) * mm, "end": v(-52.88, -37.7) * mm});
            skLineSegment(sketch, "E1004", {"start": v(-52.88, -37.7) * mm, "end": v(-55, -32.66) * mm});
            skLineSegment(sketch, "E1005", {"start": v(-55, -32.66) * mm, "end": v(-56.48, -28.33) * mm});
            skLineSegment(sketch, "E1006", {"start": v(-56.48, -28.33) * mm, "end": v(-57.45, -23.53) * mm});
            skLineSegment(sketch, "E1007", {"start": v(-57.45, -23.53) * mm, "end": v(-58.04, -19.5) * mm});
            skLineSegment(sketch, "E1008", {"start": v(-58.04, -19.5) * mm, "end": v(-58.11, -16.73) * mm});
            skLineSegment(sketch, "E1009", {"start": v(-58.11, -16.73) * mm, "end": v(-58.11, -14.05) * mm});
            skLineSegment(sketch, "E1010", {"start": v(-58.11, -14.05) * mm, "end": v(-57.57, -10.87) * mm});
            skLineSegment(sketch, "E1011", {"start": v(-57.57, -10.87) * mm, "end": v(-55.87, -4.25) * mm});
            skLineSegment(sketch, "E1012", {"start": v(-55.87, -4.25) * mm, "end": v(-54.5, 0) * mm});
            skLineSegment(sketch, "E1013", {"start": v(-54.5, 0) * mm, "end": v(-52.57, 3.4) * mm});
            skLineSegment(sketch, "E1014", {"start": v(-52.57, 3.4) * mm, "end": v(-49.96, 7.15) * mm});
            skLineSegment(sketch, "E1015", {"start": v(-49.96, 7.15) * mm, "end": v(-46.27, 11.7) * mm});
            skLineSegment(sketch, "E1016", {"start": v(-46.27, 11.7) * mm, "end": v(-41.16, 15.57) * mm});
            skLineSegment(sketch, "E1017", {"start": v(-41.16, 15.57) * mm, "end": v(-35.07, 19.41) * mm});
            skLineSegment(sketch, "E1018", {"start": v(-35.07, 19.41) * mm, "end": v(-29.12, 22.08) * mm});
            skLineSegment(sketch, "E1019", {"start": v(-29.12, 22.08) * mm, "end": v(-25.22, 23.08) * mm});
            skLineSegment(sketch, "E1020", {"start": v(-25.22, 23.08) * mm, "end": v(-19.21, 24.3) * mm});
            skLineSegment(sketch, "E1021", {"start": v(-19.21, 24.3) * mm, "end": v(-13.16, 25.52) * mm});
            skLineSegment(sketch, "E1022", {"start": v(-13.16, 25.52) * mm, "end": v(-7.17, 26.13) * mm});
            skLineSegment(sketch, "E1023", {"start": v(-7.17, 26.13) * mm, "end": v(-3.78, 26.34) * mm});
            skLineSegment(sketch, "E1024", {"start": v(-3.78, 26.34) * mm, "end": v(-0.52, 26.33) * mm});
            skLineSegment(sketch, "E1025", {"start": v(-0.52, 26.33) * mm, "end": v(4.2, 25.92) * mm});
            skLineSegment(sketch, "E1026", {"start": v(4.2, 25.92) * mm, "end": v(7.86, 25.42) * mm});
            skLineSegment(sketch, "E1027", {"start": v(7.86, 25.42) * mm, "end": v(11.17, 24.57) * mm});
            skLineSegment(sketch, "E1028", {"start": v(11.17, 24.57) * mm, "end": v(15.13, 23.55) * mm});
            skLineSegment(sketch, "E1029", {"start": v(15.13, 23.55) * mm, "end": v(19.2, 21.85) * mm});
            skLineSegment(sketch, "E1030", {"start": v(19.2, 21.85) * mm, "end": v(22.78, 20.37) * mm});
            skLineSegment(sketch, "E1031", {"start": v(22.78, 20.37) * mm, "end": v(26.35, 18.53) * mm});
            skLineSegment(sketch, "E1032", {"start": v(26.35, 18.53) * mm, "end": v(30.59, 15.96) * mm});
            skLineSegment(sketch, "E1033", {"start": v(30.59, 15.96) * mm, "end": v(36.56, 12.25) * mm});
            skLineSegment(sketch, "E1034", {"start": v(36.56, 12.25) * mm, "end": v(38.42, 10.99) * mm});
            skLineSegment(sketch, "E1035", {"start": v(38.42, 10.99) * mm, "end": v(40.32, 9.66) * mm});
            skLineSegment(sketch, "E1036", {"start": v(40.32, 9.66) * mm, "end": v(42.4, 7.78) * mm});
            skLineSegment(sketch, "E1037", {"start": v(42.4, 7.78) * mm, "end": v(44.64, 5.3) * mm});
            skLineSegment(sketch, "E1038", {"start": v(44.64, 5.3) * mm, "end": v(46.35, 3.02) * mm});
            skLineSegment(sketch, "E1039", {"start": v(46.35, 3.02) * mm, "end": v(48.97, -0.91) * mm});
            skLineSegment(sketch, "E1040", {"start": v(48.97, -0.91) * mm, "end": v(50.67, -4.06) * mm});
            skLineSegment(sketch, "E1041", {"start": v(50.67, -4.06) * mm, "end": v(52.06, -7.49) * mm});
            skLineSegment(sketch, "E1042", {"start": v(52.06, -7.49) * mm, "end": v(52.97, -10.5) * mm});
            skLineSegment(sketch, "E1043", {"start": v(52.97, -10.5) * mm, "end": v(53.6, -13.37) * mm});
            skLineSegment(sketch, "E1044", {"start": v(53.6, -13.37) * mm, "end": v(53.77, -16.1) * mm});
            skLineSegment(sketch, "E1045", {"start": v(53.77, -16.1) * mm, "end": v(53.82, -17.48) * mm});
            skLineSegment(sketch, "E1046", {"start": v(45.7, -32.68) * mm, "end": v(44.59, -34.91) * mm});
            skLineSegment(sketch, "E1047", {"start": v(44.59, -34.91) * mm, "end": v(42.05, -38.83) * mm});
            skLineSegment(sketch, "E1048", {"start": v(42.05, -38.83) * mm, "end": v(38.44, -42.93) * mm});
            skLineSegment(sketch, "E1049", {"start": v(38.44, -42.93) * mm, "end": v(33.43, -46.67) * mm});
            skLineSegment(sketch, "E1050", {"start": v(33.43, -46.67) * mm, "end": v(27.92, -50.24) * mm});
            skLineSegment(sketch, "E1051", {"start": v(27.92, -50.24) * mm, "end": v(23.5, -52.25) * mm});
            skLineSegment(sketch, "E1052", {"start": v(23.5, -52.25) * mm, "end": v(18.23, -54.06) * mm});
            skLineSegment(sketch, "E1053", {"start": v(18.23, -54.06) * mm, "end": v(11.76, -56.36) * mm});
            skLineSegment(sketch, "E1054", {"start": v(11.76, -56.36) * mm, "end": v(6.86, -57.63) * mm});
            skLineSegment(sketch, "E1055", {"start": v(6.86, -57.63) * mm, "end": v(3.34, -57.95) * mm});
            skLineSegment(sketch, "E1056", {"start": v(3.34, -57.95) * mm, "end": v(-0.82, -58.4) * mm});
            skLineSegment(sketch, "E1057", {"start": v(-0.82, -58.4) * mm, "end": v(-5.11, -58.4) * mm});
            skLineSegment(sketch, "E1058", {"start": v(-5.11, -58.4) * mm, "end": v(-8.8, -57.82) * mm});
            skLineSegment(sketch, "E1059", {"start": v(-8.8, -57.82) * mm, "end": v(-12.4, -57.2) * mm});
            skLineSegment(sketch, "E1060", {"start": v(-12.4, -57.2) * mm, "end": v(-23.8, -54.86) * mm});
            skLineSegment(sketch, "E1061", {"start": v(-23.8, -54.86) * mm, "end": v(-26.8, -54.06) * mm});
            skLineSegment(sketch, "E1062", {"start": v(-26.8, -54.06) * mm, "end": v(-29.66, -53.1) * mm});
            skLineSegment(sketch, "E1063", {"start": v(-29.66, -53.1) * mm, "end": v(-31.8, -52.03) * mm});
            skLineSegment(sketch, "E1064", {"start": v(-31.8, -52.03) * mm, "end": v(-34.8, -50.19) * mm});
            skLineSegment(sketch, "E1065", {"start": v(-34.8, -50.19) * mm, "end": v(-40.16, -45.43) * mm});
            skLineSegment(sketch, "E1066", {"start": v(-40.16, -45.43) * mm, "end": v(-43.91, -41.15) * mm});
            skLineSegment(sketch, "E1067", {"start": v(-43.91, -41.15) * mm, "end": v(-46.26, -37.82) * mm});
            skLineSegment(sketch, "E1068", {"start": v(-46.26, -37.82) * mm, "end": v(-48.9, -32.95) * mm});
            skLineSegment(sketch, "E1069", {"start": v(-48.9, -32.95) * mm, "end": v(-50.78, -28.7) * mm});
            skLineSegment(sketch, "E1070", {"start": v(-50.78, -28.7) * mm, "end": v(-52.76, -21.45) * mm});
            skLineSegment(sketch, "E1071", {"start": v(-52.76, -21.45) * mm, "end": v(-53.04, -16) * mm});
            skLineSegment(sketch, "E1072", {"start": v(-53.04, -16) * mm, "end": v(-52.7, -12.86) * mm});
            skLineSegment(sketch, "E1073", {"start": v(-52.7, -12.86) * mm, "end": v(-51.22, -7.11) * mm});
            skLineSegment(sketch, "E1074", {"start": v(-51.22, -7.11) * mm, "end": v(-50.33, -4.98) * mm});
            skLineSegment(sketch, "E1075", {"start": v(-50.33, -4.98) * mm, "end": v(-48.75, -1.25) * mm});
            skLineSegment(sketch, "E1076", {"start": v(-48.75, -1.25) * mm, "end": v(-47.1, 1.38) * mm});
            skLineSegment(sketch, "E1077", {"start": v(-47.1, 1.38) * mm, "end": v(-45.07, 4.8) * mm});
            skLineSegment(sketch, "E1078", {"start": v(-45.07, 4.8) * mm, "end": v(-43.31, 7.08) * mm});
            skLineSegment(sketch, "E1079", {"start": v(-43.31, 7.08) * mm, "end": v(-39.5, 11.28) * mm});
            skLineSegment(sketch, "E1080", {"start": v(-39.5, 11.28) * mm, "end": v(-36.17, 14.22) * mm});
            skLineSegment(sketch, "E1081", {"start": v(-36.17, 14.22) * mm, "end": v(-33.1, 16.5) * mm});
            skLineSegment(sketch, "E1082", {"start": v(-33.1, 16.5) * mm, "end": v(-30.96, 17.63) * mm});
            skLineSegment(sketch, "E1083", {"start": v(-30.96, 17.63) * mm, "end": v(-28.32, 18.64) * mm});
            skLineSegment(sketch, "E1084", {"start": v(-28.32, 18.64) * mm, "end": v(-26.33, 19.27) * mm});
            skLineSegment(sketch, "E1085", {"start": v(-26.33, 19.27) * mm, "end": v(-23.32, 20) * mm});
            skLineSegment(sketch, "E1086", {"start": v(-23.32, 20) * mm, "end": v(-20.59, 20.57) * mm});
            skLineSegment(sketch, "E1087", {"start": v(-20.59, 20.57) * mm, "end": v(-16.2, 21.37) * mm});
            skLineSegment(sketch, "E1088", {"start": v(-16.2, 21.37) * mm, "end": v(-12.25, 22.17) * mm});
            skLineSegment(sketch, "E1089", {"start": v(-12.25, 22.17) * mm, "end": v(-9.45, 22.73) * mm});
            skLineSegment(sketch, "E1090", {"start": v(-9.45, 22.73) * mm, "end": v(-5.82, 23.24) * mm});
            skLineSegment(sketch, "E1091", {"start": v(-5.82, 23.24) * mm, "end": v(-3.58, 23.44) * mm});
            skLineSegment(sketch, "E1092", {"start": v(-3.58, 23.44) * mm, "end": v(0.05, 23.43) * mm});
            skLineSegment(sketch, "E1093", {"start": v(0.05, 23.43) * mm, "end": v(2.99, 23.19) * mm});
            skLineSegment(sketch, "E1094", {"start": v(2.99, 23.19) * mm, "end": v(5.75, 22.83) * mm});
            skLineSegment(sketch, "E1095", {"start": v(5.75, 22.83) * mm, "end": v(8.04, 22.42) * mm});
            skLineSegment(sketch, "E1096", {"start": v(8.04, 22.42) * mm, "end": v(11.19, 21.61) * mm});
            skLineSegment(sketch, "E1097", {"start": v(11.19, 21.61) * mm, "end": v(14.77, 20.43) * mm});
            skLineSegment(sketch, "E1098", {"start": v(14.77, 20.43) * mm, "end": v(18.95, 18.8) * mm});
            skLineSegment(sketch, "E1099", {"start": v(18.95, 18.8) * mm, "end": v(22.6, 17.25) * mm});
            skLineSegment(sketch, "E1100", {"start": v(22.6, 17.25) * mm, "end": v(25.68, 15.56) * mm});
            skLineSegment(sketch, "E1101", {"start": v(25.68, 15.56) * mm, "end": v(29.68, 13.05) * mm});
            skLineSegment(sketch, "E1102", {"start": v(29.68, 13.05) * mm, "end": v(32.81, 10.85) * mm});
            skLineSegment(sketch, "E1103", {"start": v(32.81, 10.85) * mm, "end": v(35.4, 9.11) * mm});
            skLineSegment(sketch, "E1104", {"start": v(35.4, 9.11) * mm, "end": v(39.05, 6.42) * mm});
            skLineSegment(sketch, "E1105", {"start": v(39.05, 6.42) * mm, "end": v(40.2, 5.42) * mm});
            skLineSegment(sketch, "E1106", {"start": v(40.2, 5.42) * mm, "end": v(41.8, 3.81) * mm});
            skLineSegment(sketch, "E1107", {"start": v(41.8, 3.81) * mm, "end": v(43.26, 1.81) * mm});
            skLineSegment(sketch, "E1108", {"start": v(43.26, 1.81) * mm, "end": v(45.56, -1.57) * mm});
            skLineSegment(sketch, "E1109", {"start": v(45.56, -1.57) * mm, "end": v(47.18, -4.72) * mm});
            skLineSegment(sketch, "E1110", {"start": v(47.18, -4.72) * mm, "end": v(48.32, -7.6) * mm});
            skLineSegment(sketch, "E1111", {"start": v(48.32, -7.6) * mm, "end": v(49.23, -10.88) * mm});
            skLineSegment(sketch, "E1112", {"start": v(49.23, -10.88) * mm, "end": v(49.8, -14.3) * mm});
            skLineSegment(sketch, "E1113", {"start": v(49.8, -14.3) * mm, "end": v(49.86, -16.55) * mm});
            skLineSegment(sketch, "E1114", {"start": v(49.86, -16.55) * mm, "end": v(49.77, -19.2) * mm});
            skLineSegment(sketch, "E1115", {"start": v(49.77, -19.2) * mm, "end": v(49.3, -22.45) * mm});
            skLineSegment(sketch, "E1116", {"start": v(49.3, -22.45) * mm, "end": v(48.57, -25.86) * mm});
            skLineSegment(sketch, "E1117", {"start": v(48.57, -25.86) * mm, "end": v(47.13, -29.87) * mm});
            skLineSegment(sketch, "E1118", {"start": v(47.13, -29.87) * mm, "end": v(45.74, -32.67) * mm});
            skLineSegment(sketch, "E1119", {"start": v(45.74, -32.67) * mm, "end": v(45.7, -32.68) * mm});
            skLineSegment(sketch, "E1120", {"start": v(10.8, -17.45) * mm, "end": v(10.51, -15.06) * mm});
            skLineSegment(sketch, "E1121", {"start": v(10.51, -15.06) * mm, "end": v(10.22, -13.74) * mm});
            skLineSegment(sketch, "E1122", {"start": v(10.22, -13.74) * mm, "end": v(9.77, -12.47) * mm});
            skLineSegment(sketch, "E1123", {"start": v(9.77, -12.47) * mm, "end": v(9.14, -11) * mm});
            skLineSegment(sketch, "E1124", {"start": v(9.14, -11) * mm, "end": v(8.27, -9.58) * mm});
            skLineSegment(sketch, "E1125", {"start": v(8.27, -9.58) * mm, "end": v(7.16, -8.3) * mm});
            skLineSegment(sketch, "E1126", {"start": v(7.16, -8.3) * mm, "end": v(5.63, -6.96) * mm});
            skLineSegment(sketch, "E1127", {"start": v(5.63, -6.96) * mm, "end": v(3.84, -5.96) * mm});
            skLineSegment(sketch, "E1128", {"start": v(3.84, -5.96) * mm, "end": v(2.13, -5.35) * mm});
            skLineSegment(sketch, "E1129", {"start": v(2.13, -5.35) * mm, "end": v(1.02, -5.06) * mm});
            skLineSegment(sketch, "E1130", {"start": v(1.02, -5.06) * mm, "end": v(-0.7, -4.79) * mm});
            skLineSegment(sketch, "E1131", {"start": v(-0.7, -4.79) * mm, "end": v(-2.5, -4.73) * mm});
            skLineSegment(sketch, "E1132", {"start": v(-2.5, -4.73) * mm, "end": v(-3.78, -4.92) * mm});
            skLineSegment(sketch, "E1133", {"start": v(-3.78, -4.92) * mm, "end": v(-4.8, -5.07) * mm});
            skLineSegment(sketch, "E1134", {"start": v(-4.8, -5.07) * mm, "end": v(-6.5, -5.66) * mm});
            skLineSegment(sketch, "E1135", {"start": v(-6.5, -5.66) * mm, "end": v(-7.72, -6.22) * mm});
            skLineSegment(sketch, "E1136", {"start": v(-7.72, -6.22) * mm, "end": v(-8.77, -6.93) * mm});
            skLineSegment(sketch, "E1137", {"start": v(-8.77, -6.93) * mm, "end": v(-9.92, -7.78) * mm});
            skLineSegment(sketch, "E1138", {"start": v(-9.92, -7.78) * mm, "end": v(-10.65, -8.5) * mm});
            skLineSegment(sketch, "E1139", {"start": v(-10.65, -8.5) * mm, "end": v(-11.62, -9.65) * mm});
            skLineSegment(sketch, "E1140", {"start": v(-11.62, -9.65) * mm, "end": v(-12.36, -10.67) * mm});
            skLineSegment(sketch, "E1141", {"start": v(-12.36, -10.67) * mm, "end": v(-13.4, -12.54) * mm});
            skLineSegment(sketch, "E1142", {"start": v(-13.4, -12.54) * mm, "end": v(-13.81, -13.81) * mm});
            skLineSegment(sketch, "E1143", {"start": v(-13.81, -13.81) * mm, "end": v(-14.18, -15.24) * mm});
            skLineSegment(sketch, "E1144", {"start": v(-14.18, -15.24) * mm, "end": v(-14.35, -16.69) * mm});
            skLineSegment(sketch, "E1145", {"start": v(-14.35, -16.69) * mm, "end": v(-14.37, -18.44) * mm});
            skLineSegment(sketch, "E1146", {"start": v(-14.37, -18.44) * mm, "end": v(-14.13, -20.04) * mm});
            skLineSegment(sketch, "E1147", {"start": v(-14.13, -20.04) * mm, "end": v(-13.83, -21.23) * mm});
            skLineSegment(sketch, "E1148", {"start": v(-13.83, -21.23) * mm, "end": v(-13.16, -22.97) * mm});
            skLineSegment(sketch, "E1149", {"start": v(-13.16, -22.97) * mm, "end": v(-12.05, -24.75) * mm});
            skLineSegment(sketch, "E1150", {"start": v(-12.05, -24.75) * mm, "end": v(-11.03, -26.01) * mm});
            skLineSegment(sketch, "E1151", {"start": v(-11.03, -26.01) * mm, "end": v(-10.26, -26.83) * mm});
            skLineSegment(sketch, "E1152", {"start": v(-10.26, -26.83) * mm, "end": v(-9.3, -27.67) * mm});
            skLineSegment(sketch, "E1153", {"start": v(-9.3, -27.67) * mm, "end": v(-8.23, -28.39) * mm});
            skLineSegment(sketch, "E1154", {"start": v(-8.23, -28.39) * mm, "end": v(-6.88, -29.13) * mm});
            skLineSegment(sketch, "E1155", {"start": v(-6.88, -29.13) * mm, "end": v(-5.16, -29.77) * mm});
            skLineSegment(sketch, "E1156", {"start": v(-5.16, -29.77) * mm, "end": v(-3.8, -30.12) * mm});
            skLineSegment(sketch, "E1157", {"start": v(-3.8, -30.12) * mm, "end": v(-2.64, -30.23) * mm});
            skLineSegment(sketch, "E1158", {"start": v(-2.64, -30.23) * mm, "end": v(-0.85, -30.28) * mm});
            skLineSegment(sketch, "E1159", {"start": v(-0.85, -30.28) * mm, "end": v(1.85, -29.84) * mm});
            skLineSegment(sketch, "E1160", {"start": v(1.85, -29.84) * mm, "end": v(4, -28.91) * mm});
            skLineSegment(sketch, "E1161", {"start": v(4, -28.91) * mm, "end": v(5.13, -28.32) * mm});
            skLineSegment(sketch, "E1162", {"start": v(5.13, -28.32) * mm, "end": v(6.15, -27.54) * mm});
            skLineSegment(sketch, "E1163", {"start": v(6.15, -27.54) * mm, "end": v(7.47, -26.24) * mm});
            skLineSegment(sketch, "E1164", {"start": v(7.47, -26.24) * mm, "end": v(8.09, -25.57) * mm});
            skLineSegment(sketch, "E1165", {"start": v(8.09, -25.57) * mm, "end": v(8.74, -24.58) * mm});
            skLineSegment(sketch, "E1166", {"start": v(8.74, -24.58) * mm, "end": v(9.33, -23.6) * mm});
            skLineSegment(sketch, "E1167", {"start": v(9.33, -23.6) * mm, "end": v(10.11, -21.4) * mm});
            skLineSegment(sketch, "E1168", {"start": v(10.11, -21.4) * mm, "end": v(10.54, -20.13) * mm});
            skLineSegment(sketch, "E1169", {"start": v(10.54, -20.13) * mm, "end": v(10.73, -18.86) * mm});
            skLineSegment(sketch, "E1170", {"start": v(10.73, -18.86) * mm, "end": v(10.8, -17.45) * mm});
            skLineSegment(sketch, "E1171", {"start": v(26, -17.45) * mm, "end": v(25.82, -15.1) * mm});
            skLineSegment(sketch, "E1172", {"start": v(25.82, -15.1) * mm, "end": v(25.44, -13.24) * mm});
            skLineSegment(sketch, "E1173", {"start": v(25.44, -13.24) * mm, "end": v(24.91, -11.72) * mm});
            skLineSegment(sketch, "E1174", {"start": v(24.91, -11.72) * mm, "end": v(23.33, -9) * mm});
            skLineSegment(sketch, "E1175", {"start": v(23.33, -9) * mm, "end": v(22.14, -7.62) * mm});
            skLineSegment(sketch, "E1176", {"start": v(22.14, -7.62) * mm, "end": v(19.78, -5.47) * mm});
            skLineSegment(sketch, "E1177", {"start": v(19.78, -5.47) * mm, "end": v(18.35, -4.36) * mm});
            skLineSegment(sketch, "E1178", {"start": v(18.35, -4.36) * mm, "end": v(15.52, -2.33) * mm});
            skLineSegment(sketch, "E1179", {"start": v(15.52, -2.33) * mm, "end": v(13.78, -1.25) * mm});
            skLineSegment(sketch, "E1180", {"start": v(13.78, -1.25) * mm, "end": v(11.58, 0.03) * mm});
            skLineSegment(sketch, "E1181", {"start": v(11.58, 0.03) * mm, "end": v(8.77, 1.14) * mm});
            skLineSegment(sketch, "E1182", {"start": v(8.77, 1.14) * mm, "end": v(6.78, 1.8) * mm});
            skLineSegment(sketch, "E1183", {"start": v(6.78, 1.8) * mm, "end": v(3.65, 2.46) * mm});
            skLineSegment(sketch, "E1184", {"start": v(3.65, 2.46) * mm, "end": v(0.95, 2.88) * mm});
            skLineSegment(sketch, "E1185", {"start": v(0.95, 2.88) * mm, "end": v(-1.19, 3.08) * mm});
            skLineSegment(sketch, "E1186", {"start": v(-1.19, 3.08) * mm, "end": v(-4, 3.3) * mm});
            skLineSegment(sketch, "E1187", {"start": v(-4, 3.3) * mm, "end": v(-6.93, 3.26) * mm});
            skLineSegment(sketch, "E1188", {"start": v(-6.93, 3.26) * mm, "end": v(-9.17, 3.05) * mm});
            skLineSegment(sketch, "E1189", {"start": v(-9.17, 3.05) * mm, "end": v(-10.73, 2.7) * mm});
            skLineSegment(sketch, "E1190", {"start": v(-10.73, 2.7) * mm, "end": v(-12.29, 2.12) * mm});
            skLineSegment(sketch, "E1191", {"start": v(-12.29, 2.12) * mm, "end": v(-14.3, 1.23) * mm});
            skLineSegment(sketch, "E1192", {"start": v(-14.3, 1.23) * mm, "end": v(-16.43, -0.07) * mm});
            skLineSegment(sketch, "E1193", {"start": v(-16.43, -0.07) * mm, "end": v(-18.4, -1.74) * mm});
            skLineSegment(sketch, "E1194", {"start": v(-18.4, -1.74) * mm, "end": v(-19.55, -2.78) * mm});
            skLineSegment(sketch, "E1195", {"start": v(-19.55, -2.78) * mm, "end": v(-20.47, -3.9) * mm});
            skLineSegment(sketch, "E1196", {"start": v(-20.47, -3.9) * mm, "end": v(-21.88, -5.7) * mm});
            skLineSegment(sketch, "E1197", {"start": v(-21.88, -5.7) * mm, "end": v(-23.23, -8.1) * mm});
            skLineSegment(sketch, "E1198", {"start": v(-23.23, -8.1) * mm, "end": v(-24.21, -10.35) * mm});
            skLineSegment(sketch, "E1199", {"start": v(-24.21, -10.35) * mm, "end": v(-25.14, -13.58) * mm});
            skLineSegment(sketch, "E1200", {"start": v(-25.14, -13.58) * mm, "end": v(-25.52, -16.4) * mm});
            skLineSegment(sketch, "E1201", {"start": v(-25.52, -16.4) * mm, "end": v(-25.46, -18.73) * mm});
            skLineSegment(sketch, "E1202", {"start": v(-25.46, -18.73) * mm, "end": v(-25.2, -21.25) * mm});
            skLineSegment(sketch, "E1203", {"start": v(-25.2, -21.25) * mm, "end": v(-24.38, -24.1) * mm});
            skLineSegment(sketch, "E1204", {"start": v(-24.38, -24.1) * mm, "end": v(-23.39, -26.49) * mm});
            skLineSegment(sketch, "E1205", {"start": v(-23.39, -26.49) * mm, "end": v(-21.75, -29.28) * mm});
            skLineSegment(sketch, "E1206", {"start": v(-21.75, -29.28) * mm, "end": v(-19.76, -31.97) * mm});
            skLineSegment(sketch, "E1207", {"start": v(-19.76, -31.97) * mm, "end": v(-17.88, -33.7) * mm});
            skLineSegment(sketch, "E1208", {"start": v(-17.88, -33.7) * mm, "end": v(-15.83, -35.26) * mm});
            skLineSegment(sketch, "E1209", {"start": v(-15.83, -35.26) * mm, "end": v(-13.08, -36.78) * mm});
            skLineSegment(sketch, "E1210", {"start": v(-13.08, -36.78) * mm, "end": v(-10.34, -37.78) * mm});
            skLineSegment(sketch, "E1211", {"start": v(-10.34, -37.78) * mm, "end": v(-7.78, -38.17) * mm});
            skLineSegment(sketch, "E1212", {"start": v(-7.78, -38.17) * mm, "end": v(-4.83, -38.3) * mm});
            skLineSegment(sketch, "E1213", {"start": v(-4.83, -38.3) * mm, "end": v(-0.63, -38.05) * mm});
            skLineSegment(sketch, "E1214", {"start": v(-0.63, -38.05) * mm, "end": v(2.82, -37.51) * mm});
            skLineSegment(sketch, "E1215", {"start": v(2.82, -37.51) * mm, "end": v(6.27, -36.66) * mm});
            skLineSegment(sketch, "E1216", {"start": v(6.27, -36.66) * mm, "end": v(9.65, -35.54) * mm});
            skLineSegment(sketch, "E1217", {"start": v(9.65, -35.54) * mm, "end": v(13.34, -33.76) * mm});
            skLineSegment(sketch, "E1218", {"start": v(13.34, -33.76) * mm, "end": v(17.96, -30.88) * mm});
            skLineSegment(sketch, "E1219", {"start": v(17.96, -30.88) * mm, "end": v(20.23, -29.13) * mm});
            skLineSegment(sketch, "E1220", {"start": v(20.23, -29.13) * mm, "end": v(22.6, -26.7) * mm});
            skLineSegment(sketch, "E1221", {"start": v(22.6, -26.7) * mm, "end": v(24.87, -22.94) * mm});
            skLineSegment(sketch, "E1222", {"start": v(24.87, -22.94) * mm, "end": v(25.92, -19.47) * mm});
            skLineSegment(sketch, "E1223", {"start": v(25.92, -19.47) * mm, "end": v(26, -17.45) * mm});
            skLineSegment(sketch, "E1224", {"start": v(10.8, 6.6) * mm, "end": v(16.16, 4.68) * mm});
            skLineSegment(sketch, "E1225", {"start": v(16.16, 4.68) * mm, "end": v(23.83, 0.95) * mm});
            skLineSegment(sketch, "E1226", {"start": v(23.83, 0.95) * mm, "end": v(29.07, -3.05) * mm});
            skLineSegment(sketch, "E1227", {"start": v(29.07, -3.05) * mm, "end": v(31.42, -6.74) * mm});
            skLineSegment(sketch, "E1228", {"start": v(31.42, -6.74) * mm, "end": v(33.21, -11.43) * mm});
            skLineSegment(sketch, "E1229", {"start": v(33.21, -11.43) * mm, "end": v(34.33, -16.42) * mm});
            skLineSegment(sketch, "E1230", {"start": v(34.33, -16.42) * mm, "end": v(33.72, -22.17) * mm});
            skLineSegment(sketch, "E1231", {"start": v(33.72, -22.17) * mm, "end": v(31.45, -28.37) * mm});
            skLineSegment(sketch, "E1232", {"start": v(31.45, -28.37) * mm, "end": v(28.59, -32) * mm});
            skLineSegment(sketch, "E1233", {"start": v(28.59, -32) * mm, "end": v(25.44, -34.89) * mm});
            skLineSegment(sketch, "E1234", {"start": v(25.44, -34.89) * mm, "end": v(19.43, -37.92) * mm});
            skLineSegment(sketch, "E1235", {"start": v(19.43, -37.92) * mm, "end": v(14.15, -40.34) * mm});
            skLineSegment(sketch, "E1236", {"start": v(14.15, -40.34) * mm, "end": v(9.2, -41.79) * mm});
            skLineSegment(sketch, "E1237", {"start": v(9.2, -41.79) * mm, "end": v(3.64, -42.72) * mm});
            skLineSegment(sketch, "E1238", {"start": v(3.64, -42.72) * mm, "end": v(-2.12, -43.2) * mm});
            skLineSegment(sketch, "E1239", {"start": v(-2.12, -43.2) * mm, "end": v(-6.96, -43.44) * mm});
            skLineSegment(sketch, "E1240", {"start": v(-6.96, -43.44) * mm, "end": v(-10.44, -42.92) * mm});
            skLineSegment(sketch, "E1241", {"start": v(-10.44, -42.92) * mm, "end": v(-13.41, -42.18) * mm});
            skLineSegment(sketch, "E1242", {"start": v(-13.41, -42.18) * mm, "end": v(-18.31, -40.03) * mm});
            skLineSegment(sketch, "E1243", {"start": v(-18.31, -40.03) * mm, "end": v(-22.07, -37.2) * mm});
            skLineSegment(sketch, "E1244", {"start": v(-22.07, -37.2) * mm, "end": v(-25.67, -33.56) * mm});
            skLineSegment(sketch, "E1245", {"start": v(-25.67, -33.56) * mm, "end": v(-28.4, -29.95) * mm});
            skLineSegment(sketch, "E1246", {"start": v(-28.4, -29.95) * mm, "end": v(-31.06, -24.75) * mm});
            skLineSegment(sketch, "E1247", {"start": v(-31.06, -24.75) * mm, "end": v(-32.14, -20.44) * mm});
            skLineSegment(sketch, "E1248", {"start": v(-32.14, -20.44) * mm, "end": v(-32.3, -17) * mm});
            skLineSegment(sketch, "E1249", {"start": v(-32.3, -17) * mm, "end": v(-32.17, -14.4) * mm});
            skLineSegment(sketch, "E1250", {"start": v(-32.17, -14.4) * mm, "end": v(-30.81, -9.12) * mm});
            skLineSegment(sketch, "E1251", {"start": v(-30.81, -9.12) * mm, "end": v(-29.3, -6.59) * mm});
            skLineSegment(sketch, "E1252", {"start": v(-29.3, -6.59) * mm, "end": v(-26.95, -2.84) * mm});
            skLineSegment(sketch, "E1253", {"start": v(-26.95, -2.84) * mm, "end": v(-24.42, 0.16) * mm});
            skLineSegment(sketch, "E1254", {"start": v(-24.42, 0.16) * mm, "end": v(-20.66, 3.4) * mm});
            skLineSegment(sketch, "E1255", {"start": v(-20.66, 3.4) * mm, "end": v(-17.33, 5.63) * mm});
            skLineSegment(sketch, "E1256", {"start": v(-17.33, 5.63) * mm, "end": v(-14.85, 6.81) * mm});
            skLineSegment(sketch, "E1257", {"start": v(-14.85, 6.81) * mm, "end": v(-11.55, 7.97) * mm});
            skLineSegment(sketch, "E1258", {"start": v(-11.55, 7.97) * mm, "end": v(-8.44, 8.35) * mm});
            skLineSegment(sketch, "E1259", {"start": v(-8.44, 8.35) * mm, "end": v(-5.75, 8.49) * mm});
            skLineSegment(sketch, "E1260", {"start": v(-5.75, 8.49) * mm, "end": v(-1.23, 8.2) * mm});
            skLineSegment(sketch, "E1261", {"start": v(-1.23, 8.2) * mm, "end": v(4.51, 7.65) * mm});
            skLineSegment(sketch, "E1262", {"start": v(4.51, 7.65) * mm, "end": v(8.4, 7) * mm});
            skLineSegment(sketch, "E1263", {"start": v(8.4, 7) * mm, "end": v(10.8, 6.6) * mm});
            skLineSegment(sketch, "E1264", {"start": v(38.56, -17.45) * mm, "end": v(38.42, -20.37) * mm});
            skLineSegment(sketch, "E1265", {"start": v(38.42, -20.37) * mm, "end": v(37.72, -22.96) * mm});
            skLineSegment(sketch, "E1266", {"start": v(37.72, -22.96) * mm, "end": v(36.9, -25.26) * mm});
            skLineSegment(sketch, "E1267", {"start": v(36.9, -25.26) * mm, "end": v(35.66, -27.83) * mm});
            skLineSegment(sketch, "E1268", {"start": v(35.66, -27.83) * mm, "end": v(34.67, -29.65) * mm});
            skLineSegment(sketch, "E1269", {"start": v(34.67, -29.65) * mm, "end": v(32.78, -32.3) * mm});
            skLineSegment(sketch, "E1270", {"start": v(32.78, -32.3) * mm, "end": v(31.4, -34.12) * mm});
            skLineSegment(sketch, "E1271", {"start": v(31.4, -34.12) * mm, "end": v(29.34, -36.32) * mm});
            skLineSegment(sketch, "E1272", {"start": v(29.34, -36.32) * mm, "end": v(27.13, -38.06) * mm});
            skLineSegment(sketch, "E1273", {"start": v(27.13, -38.06) * mm, "end": v(24.23, -39.8) * mm});
            skLineSegment(sketch, "E1274", {"start": v(24.23, -39.8) * mm, "end": v(19.17, -42.06) * mm});
            skLineSegment(sketch, "E1275", {"start": v(19.17, -42.06) * mm, "end": v(14.7, -43.94) * mm});
            skLineSegment(sketch, "E1276", {"start": v(14.7, -43.94) * mm, "end": v(10.7, -45.26) * mm});
            skLineSegment(sketch, "E1277", {"start": v(10.7, -45.26) * mm, "end": v(5.84, -46.2) * mm});
            skLineSegment(sketch, "E1278", {"start": v(5.84, -46.2) * mm, "end": v(0.73, -46.86) * mm});
            skLineSegment(sketch, "E1279", {"start": v(0.73, -46.86) * mm, "end": v(-2.73, -47.19) * mm});
            skLineSegment(sketch, "E1280", {"start": v(-2.73, -47.19) * mm, "end": v(-7.07, -47.25) * mm});
            skLineSegment(sketch, "E1281", {"start": v(-7.07, -47.25) * mm, "end": v(-10.2, -46.9) * mm});
            skLineSegment(sketch, "E1282", {"start": v(-10.2, -46.9) * mm, "end": v(-13.5, -46.14) * mm});
            skLineSegment(sketch, "E1283", {"start": v(-13.5, -46.14) * mm, "end": v(-18.1, -44.76) * mm});
            skLineSegment(sketch, "E1284", {"start": v(-18.1, -44.76) * mm, "end": v(-21.24, -43.35) * mm});
            skLineSegment(sketch, "E1285", {"start": v(-21.24, -43.35) * mm, "end": v(-24.3, -41.8) * mm});
            skLineSegment(sketch, "E1286", {"start": v(-24.3, -41.8) * mm, "end": v(-26.85, -40.23) * mm});
            skLineSegment(sketch, "E1287", {"start": v(-26.85, -40.23) * mm, "end": v(-29.57, -38.12) * mm});
            skLineSegment(sketch, "E1288", {"start": v(-29.57, -38.12) * mm, "end": v(-32.3, -35.14) * mm});
            skLineSegment(sketch, "E1289", {"start": v(-32.3, -35.14) * mm, "end": v(-33.86, -32.85) * mm});
            skLineSegment(sketch, "E1290", {"start": v(-33.86, -32.85) * mm, "end": v(-35.53, -29.9) * mm});
            skLineSegment(sketch, "E1291", {"start": v(-35.53, -29.9) * mm, "end": v(-36.82, -26.7) * mm});
            skLineSegment(sketch, "E1292", {"start": v(-36.82, -26.7) * mm, "end": v(-37.58, -24.27) * mm});
            skLineSegment(sketch, "E1293", {"start": v(-37.58, -24.27) * mm, "end": v(-38.31, -21.03) * mm});
            skLineSegment(sketch, "E1294", {"start": v(-38.31, -21.03) * mm, "end": v(-38.58, -17.45) * mm});
            skLineSegment(sketch, "E1295", {"start": v(-38.58, -17.45) * mm, "end": v(-38.43, -14.96) * mm});
            skLineSegment(sketch, "E1296", {"start": v(-38.43, -14.96) * mm, "end": v(-38.23, -13.27) * mm});
            skLineSegment(sketch, "E1297", {"start": v(-38.23, -13.27) * mm, "end": v(-37.3, -9.56) * mm});
            skLineSegment(sketch, "E1298", {"start": v(-37.3, -9.56) * mm, "end": v(-36.18, -6.55) * mm});
            skLineSegment(sketch, "E1299", {"start": v(-36.18, -6.55) * mm, "end": v(-34.88, -3.49) * mm});
            skLineSegment(sketch, "E1300", {"start": v(-34.88, -3.49) * mm, "end": v(-33.44, -1.28) * mm});
            skLineSegment(sketch, "E1301", {"start": v(-33.44, -1.28) * mm, "end": v(-30.6, 2.14) * mm});
            skLineSegment(sketch, "E1302", {"start": v(-30.6, 2.14) * mm, "end": v(-28.58, 4.01) * mm});
            skLineSegment(sketch, "E1303", {"start": v(-28.58, 4.01) * mm, "end": v(-24.75, 6.6) * mm});
            skLineSegment(sketch, "E1304", {"start": v(-24.75, 6.6) * mm, "end": v(-22.06, 8.05) * mm});
            skLineSegment(sketch, "E1305", {"start": v(-22.06, 8.05) * mm, "end": v(-19.6, 9.1) * mm});
            skLineSegment(sketch, "E1306", {"start": v(-19.6, 9.1) * mm, "end": v(-15.28, 10.7) * mm});
            skLineSegment(sketch, "E1307", {"start": v(-15.28, 10.7) * mm, "end": v(-11.95, 11.56) * mm});
            skLineSegment(sketch, "E1308", {"start": v(-11.95, 11.56) * mm, "end": v(-8.57, 12.13) * mm});
            skLineSegment(sketch, "E1309", {"start": v(-8.57, 12.13) * mm, "end": v(-4.79, 12.3) * mm});
            skLineSegment(sketch, "E1310", {"start": v(-4.79, 12.3) * mm, "end": v(-1.43, 12.07) * mm});
            skLineSegment(sketch, "E1311", {"start": v(-1.43, 12.07) * mm, "end": v(1.27, 11.88) * mm});
            skLineSegment(sketch, "E1312", {"start": v(1.27, 11.88) * mm, "end": v(6.06, 11.28) * mm});
            skLineSegment(sketch, "E1313", {"start": v(6.06, 11.28) * mm, "end": v(9.12, 10.68) * mm});
            skLineSegment(sketch, "E1314", {"start": v(9.12, 10.68) * mm, "end": v(12.52, 9.77) * mm});
            skLineSegment(sketch, "E1315", {"start": v(12.52, 9.77) * mm, "end": v(15.3, 8.58) * mm});
            skLineSegment(sketch, "E1316", {"start": v(15.3, 8.58) * mm, "end": v(19.96, 6.68) * mm});
            skLineSegment(sketch, "E1317", {"start": v(19.96, 6.68) * mm, "end": v(23.85, 5.02) * mm});
            skLineSegment(sketch, "E1318", {"start": v(23.85, 5.02) * mm, "end": v(27.47, 2.87) * mm});
            skLineSegment(sketch, "E1319", {"start": v(27.47, 2.87) * mm, "end": v(30.55, 0.2) * mm});
            skLineSegment(sketch, "E1320", {"start": v(30.55, 0.2) * mm, "end": v(32.27, -1.8) * mm});
            skLineSegment(sketch, "E1321", {"start": v(32.27, -1.8) * mm, "end": v(34.21, -4.49) * mm});
            skLineSegment(sketch, "E1322", {"start": v(34.21, -4.49) * mm, "end": v(36.13, -7.68) * mm});
            skLineSegment(sketch, "E1323", {"start": v(36.13, -7.68) * mm, "end": v(37.27, -10.53) * mm});
            skLineSegment(sketch, "E1324", {"start": v(37.27, -10.53) * mm, "end": v(38.09, -13.36) * mm});
            skLineSegment(sketch, "E1325", {"start": v(38.09, -13.36) * mm, "end": v(38.47, -15.72) * mm});
            skLineSegment(sketch, "E1326", {"start": v(38.47, -15.72) * mm, "end": v(38.58, -17.43) * mm});
            skLineSegment(sketch, "E1327", {"start": v(38.58, -17.43) * mm, "end": v(38.56, -17.45) * mm});
            skLineSegment(sketch, "E1328", {"start": v(107.38, -12.7) * mm, "end": v(112, -12.7) * mm});
            skLineSegment(sketch, "E1329", {"start": v(112, -12.7) * mm, "end": v(113.09, -13.01) * mm});
            skLineSegment(sketch, "E1330", {"start": v(113.09, -13.01) * mm, "end": v(113.98, -13.46) * mm});
            skLineSegment(sketch, "E1331", {"start": v(113.98, -13.46) * mm, "end": v(114.6, -13.82) * mm});
            skLineSegment(sketch, "E1332", {"start": v(114.6, -13.82) * mm, "end": v(115.33, -14.53) * mm});
            skLineSegment(sketch, "E1333", {"start": v(115.33, -14.53) * mm, "end": v(116.01, -15.6) * mm});
            skLineSegment(sketch, "E1334", {"start": v(116.01, -15.6) * mm, "end": v(116.26, -16.4) * mm});
            skLineSegment(sketch, "E1335", {"start": v(116.26, -16.4) * mm, "end": v(116.33, -17.47) * mm});
            skLineSegment(sketch, "E1336", {"start": v(116.33, -17.47) * mm, "end": v(116.27, -18.3) * mm});
            skLineSegment(sketch, "E1337", {"start": v(116.27, -18.3) * mm, "end": v(115.92, -19.52) * mm});
            skLineSegment(sketch, "E1338", {"start": v(115.92, -19.52) * mm, "end": v(115.34, -20.39) * mm});
            skLineSegment(sketch, "E1339", {"start": v(115.34, -20.39) * mm, "end": v(114.7, -21.12) * mm});
            skLineSegment(sketch, "E1340", {"start": v(114.7, -21.12) * mm, "end": v(113.58, -21.77) * mm});
            skLineSegment(sketch, "E1341", {"start": v(113.58, -21.77) * mm, "end": v(112.51, -22.2) * mm});
            skLineSegment(sketch, "E1342", {"start": v(112.51, -22.2) * mm, "end": v(111.64, -22.27) * mm});
            skLineSegment(sketch, "E1343", {"start": v(111.64, -22.27) * mm, "end": v(107.4, -22.23) * mm});
            skLineSegment(sketch, "E1344", {"start": v(46.96, -17.53) * mm, "end": v(46.96, -19.82) * mm});
            skLineSegment(sketch, "E1345", {"start": v(46.96, -19.82) * mm, "end": v(46.53, -21.89) * mm});
            skLineSegment(sketch, "E1346", {"start": v(46.53, -21.89) * mm, "end": v(46.18, -23.62) * mm});
            skLineSegment(sketch, "E1347", {"start": v(46.18, -23.62) * mm, "end": v(45.42, -26.3) * mm});
            skLineSegment(sketch, "E1348", {"start": v(45.42, -26.3) * mm, "end": v(44.45, -28.86) * mm});
            skLineSegment(sketch, "E1349", {"start": v(44.45, -28.86) * mm, "end": v(43.08, -31.91) * mm});
            skLineSegment(sketch, "E1350", {"start": v(43.08, -31.91) * mm, "end": v(41.84, -34.12) * mm});
            skLineSegment(sketch, "E1351", {"start": v(41.84, -34.12) * mm, "end": v(40.6, -35.72) * mm});
            skLineSegment(sketch, "E1352", {"start": v(40.6, -35.72) * mm, "end": v(38.6, -38.09) * mm});
            skLineSegment(sketch, "E1353", {"start": v(38.6, -38.09) * mm, "end": v(36.14, -40.35) * mm});
            skLineSegment(sketch, "E1354", {"start": v(36.14, -40.35) * mm, "end": v(30.86, -44.43) * mm});
            skLineSegment(sketch, "E1355", {"start": v(30.86, -44.43) * mm, "end": v(28.33, -46.12) * mm});
            skLineSegment(sketch, "E1356", {"start": v(28.33, -46.12) * mm, "end": v(25.77, -47.6) * mm});
            skLineSegment(sketch, "E1357", {"start": v(25.77, -47.6) * mm, "end": v(23.82, -48.47) * mm});
            skLineSegment(sketch, "E1358", {"start": v(23.82, -48.47) * mm, "end": v(21.9, -49.19) * mm});
            skLineSegment(sketch, "E1359", {"start": v(21.9, -49.19) * mm, "end": v(17.08, -51.1) * mm});
            skLineSegment(sketch, "E1360", {"start": v(17.08, -51.1) * mm, "end": v(11.87, -52.87) * mm});
            skLineSegment(sketch, "E1361", {"start": v(11.87, -52.87) * mm, "end": v(8.13, -53.73) * mm});
            skLineSegment(sketch, "E1362", {"start": v(8.13, -53.73) * mm, "end": v(4.37, -54.38) * mm});
            skLineSegment(sketch, "E1363", {"start": v(4.37, -54.38) * mm, "end": v(0.3, -54.75) * mm});
            skLineSegment(sketch, "E1364", {"start": v(0.3, -54.75) * mm, "end": v(-3.52, -54.75) * mm});
            skLineSegment(sketch, "E1365", {"start": v(-3.52, -54.75) * mm, "end": v(-6.74, -54.75) * mm});
            skLineSegment(sketch, "E1366", {"start": v(-6.74, -54.75) * mm, "end": v(-10.13, -54.31) * mm});
            skLineSegment(sketch, "E1367", {"start": v(-10.13, -54.31) * mm, "end": v(-14, -53.5) * mm});
            skLineSegment(sketch, "E1368", {"start": v(-14, -53.5) * mm, "end": v(-19.68, -52.03) * mm});
            skLineSegment(sketch, "E1369", {"start": v(-19.68, -52.03) * mm, "end": v(-23.08, -50.92) * mm});
            skLineSegment(sketch, "E1370", {"start": v(-23.08, -50.92) * mm, "end": v(-27.82, -48.91) * mm});
            skLineSegment(sketch, "E1371", {"start": v(-27.82, -48.91) * mm, "end": v(-30.23, -47.5) * mm});
            skLineSegment(sketch, "E1372", {"start": v(-30.23, -47.5) * mm, "end": v(-32.1, -46.1) * mm});
            skLineSegment(sketch, "E1373", {"start": v(-32.1, -46.1) * mm, "end": v(-34.43, -44.19) * mm});
            skLineSegment(sketch, "E1374", {"start": v(-34.43, -44.19) * mm, "end": v(-36.65, -41.95) * mm});
            skLineSegment(sketch, "E1375", {"start": v(-36.65, -41.95) * mm, "end": v(-39.81, -38.2) * mm});
            skLineSegment(sketch, "E1376", {"start": v(-39.81, -38.2) * mm, "end": v(-42.57, -34.14) * mm});
            skLineSegment(sketch, "E1377", {"start": v(-42.57, -34.14) * mm, "end": v(-44.92, -29.49) * mm});
            skLineSegment(sketch, "E1378", {"start": v(-44.92, -29.49) * mm, "end": v(-46.46, -25.39) * mm});
            skLineSegment(sketch, "E1379", {"start": v(-46.46, -25.39) * mm, "end": v(-46.92, -23.88) * mm});
            skLineSegment(sketch, "E1380", {"start": v(-46.92, -23.88) * mm, "end": v(-47.54, -19.83) * mm});
            skLineSegment(sketch, "E1381", {"start": v(-47.54, -19.83) * mm, "end": v(-47.55, -16.33) * mm});
            skLineSegment(sketch, "E1382", {"start": v(-47.55, -16.33) * mm, "end": v(-47.37, -13.26) * mm});
            skLineSegment(sketch, "E1383", {"start": v(-47.37, -13.26) * mm, "end": v(-46.9, -11.02) * mm});
            skLineSegment(sketch, "E1384", {"start": v(-46.9, -11.02) * mm, "end": v(-45.69, -6.95) * mm});
            skLineSegment(sketch, "E1385", {"start": v(-45.69, -6.95) * mm, "end": v(-44.62, -4.6) * mm});
            skLineSegment(sketch, "E1386", {"start": v(-44.62, -4.6) * mm, "end": v(-43.11, -1.61) * mm});
            skLineSegment(sketch, "E1387", {"start": v(-43.11, -1.61) * mm, "end": v(-41.54, 0.88) * mm});
            skLineSegment(sketch, "E1388", {"start": v(-41.54, 0.88) * mm, "end": v(-39.42, 3.83) * mm});
            skLineSegment(sketch, "E1389", {"start": v(-39.42, 3.83) * mm, "end": v(-36.63, 7.16) * mm});
            skLineSegment(sketch, "E1390", {"start": v(-36.63, 7.16) * mm, "end": v(-33.78, 9.93) * mm});
            skLineSegment(sketch, "E1391", {"start": v(-33.78, 9.93) * mm, "end": v(-31.26, 11.78) * mm});
            skLineSegment(sketch, "E1392", {"start": v(-31.26, 11.78) * mm, "end": v(-27.82, 13.98) * mm});
            skLineSegment(sketch, "E1393", {"start": v(-27.82, 13.98) * mm, "end": v(-25.5, 15.05) * mm});
            skLineSegment(sketch, "E1394", {"start": v(-25.5, 15.05) * mm, "end": v(-23.19, 15.98) * mm});
            skLineSegment(sketch, "E1395", {"start": v(-23.19, 15.98) * mm, "end": v(-19.75, 17.03) * mm});
            skLineSegment(sketch, "E1396", {"start": v(-19.75, 17.03) * mm, "end": v(-16.63, 17.95) * mm});
            skLineSegment(sketch, "E1397", {"start": v(-16.63, 17.95) * mm, "end": v(-12.38, 18.96) * mm});
            skLineSegment(sketch, "E1398", {"start": v(-12.38, 18.96) * mm, "end": v(-9.3, 19.52) * mm});
            skLineSegment(sketch, "E1399", {"start": v(-9.3, 19.52) * mm, "end": v(-7, 19.76) * mm});
            skLineSegment(sketch, "E1400", {"start": v(-7, 19.76) * mm, "end": v(-5.1, 19.89) * mm});
            skLineSegment(sketch, "E1401", {"start": v(-5.1, 19.89) * mm, "end": v(-1.84, 19.9) * mm});
            skLineSegment(sketch, "E1402", {"start": v(-1.84, 19.9) * mm, "end": v(1.08, 19.72) * mm});
            skLineSegment(sketch, "E1403", {"start": v(1.08, 19.72) * mm, "end": v(3.2, 19.49) * mm});
            skLineSegment(sketch, "E1404", {"start": v(3.2, 19.49) * mm, "end": v(5.07, 19.24) * mm});
            skLineSegment(sketch, "E1405", {"start": v(5.07, 19.24) * mm, "end": v(7.15, 18.9) * mm});
            skLineSegment(sketch, "E1406", {"start": v(7.15, 18.9) * mm, "end": v(9.57, 18.32) * mm});
            skLineSegment(sketch, "E1407", {"start": v(9.57, 18.32) * mm, "end": v(11.06, 17.87) * mm});
            skLineSegment(sketch, "E1408", {"start": v(11.06, 17.87) * mm, "end": v(13.36, 17.1) * mm});
            skLineSegment(sketch, "E1409", {"start": v(13.36, 17.1) * mm, "end": v(15.79, 16.21) * mm});
            skLineSegment(sketch, "E1410", {"start": v(15.79, 16.21) * mm, "end": v(18.73, 15.08) * mm});
            skLineSegment(sketch, "E1411", {"start": v(18.73, 15.08) * mm, "end": v(20.85, 14.14) * mm});
            skLineSegment(sketch, "E1412", {"start": v(20.85, 14.14) * mm, "end": v(23.6, 12.87) * mm});
            skLineSegment(sketch, "E1413", {"start": v(23.6, 12.87) * mm, "end": v(26.2, 11.43) * mm});
            skLineSegment(sketch, "E1414", {"start": v(26.2, 11.43) * mm, "end": v(30.49, 8.52) * mm});
            skLineSegment(sketch, "E1415", {"start": v(30.49, 8.52) * mm, "end": v(32.75, 6.76) * mm});
            skLineSegment(sketch, "E1416", {"start": v(32.75, 6.76) * mm, "end": v(35.9, 4.4) * mm});
            skLineSegment(sketch, "E1417", {"start": v(35.9, 4.4) * mm, "end": v(37.98, 2.68) * mm});
            skLineSegment(sketch, "E1418", {"start": v(37.98, 2.68) * mm, "end": v(39.96, 0.75) * mm});
            skLineSegment(sketch, "E1419", {"start": v(39.96, 0.75) * mm, "end": v(41.55, -1.11) * mm});
            skLineSegment(sketch, "E1420", {"start": v(41.55, -1.11) * mm, "end": v(43.24, -3.68) * mm});
            skLineSegment(sketch, "E1421", {"start": v(43.24, -3.68) * mm, "end": v(44.35, -5.94) * mm});
            skLineSegment(sketch, "E1422", {"start": v(44.35, -5.94) * mm, "end": v(45.3, -8.41) * mm});
            skLineSegment(sketch, "E1423", {"start": v(45.3, -8.41) * mm, "end": v(46.1, -10.9) * mm});
            skLineSegment(sketch, "E1424", {"start": v(46.1, -10.9) * mm, "end": v(46.62, -12.98) * mm});
            skLineSegment(sketch, "E1425", {"start": v(46.62, -12.98) * mm, "end": v(46.96, -16.1) * mm});
            skLineSegment(sketch, "E1426", {"start": v(46.96, -16.1) * mm, "end": v(46.96, -17.53) * mm});
            skLineSegment(sketch, "E1427", {"start": v(43.06, -17.53) * mm, "end": v(43.06, -18.43) * mm});
            skLineSegment(sketch, "E1428", {"start": v(43.06, -18.43) * mm, "end": v(42.99, -19.47) * mm});
            skLineSegment(sketch, "E1429", {"start": v(42.99, -19.47) * mm, "end": v(42.73, -20.61) * mm});
            skLineSegment(sketch, "E1430", {"start": v(42.73, -20.61) * mm, "end": v(42.51, -21.8) * mm});
            skLineSegment(sketch, "E1431", {"start": v(42.51, -21.8) * mm, "end": v(41.83, -23.95) * mm});
            skLineSegment(sketch, "E1432", {"start": v(41.83, -23.95) * mm, "end": v(40.78, -26.26) * mm});
            skLineSegment(sketch, "E1433", {"start": v(40.78, -26.26) * mm, "end": v(39.76, -28.14) * mm});
            skLineSegment(sketch, "E1434", {"start": v(39.76, -28.14) * mm, "end": v(38.23, -30.58) * mm});
            skLineSegment(sketch, "E1435", {"start": v(38.23, -30.58) * mm, "end": v(36.97, -32.3) * mm});
            skLineSegment(sketch, "E1436", {"start": v(36.97, -32.3) * mm, "end": v(35.17, -34.52) * mm});
            skLineSegment(sketch, "E1437", {"start": v(35.17, -34.52) * mm, "end": v(33.77, -36.11) * mm});
            skLineSegment(sketch, "E1438", {"start": v(33.77, -36.11) * mm, "end": v(31.74, -38.22) * mm});
            skLineSegment(sketch, "E1439", {"start": v(31.74, -38.22) * mm, "end": v(29.34, -40.42) * mm});
            skLineSegment(sketch, "E1440", {"start": v(29.34, -40.42) * mm, "end": v(26.38, -42.46) * mm});
            skLineSegment(sketch, "E1441", {"start": v(26.38, -42.46) * mm, "end": v(23.57, -44.01) * mm});
            skLineSegment(sketch, "E1442", {"start": v(23.57, -44.01) * mm, "end": v(20.4, -45.44) * mm});
            skLineSegment(sketch, "E1443", {"start": v(20.4, -45.44) * mm, "end": v(18, -46.4) * mm});
            skLineSegment(sketch, "E1444", {"start": v(18, -46.4) * mm, "end": v(13.76, -48.13) * mm});
            skLineSegment(sketch, "E1445", {"start": v(13.76, -48.13) * mm, "end": v(9.82, -49.34) * mm});
            skLineSegment(sketch, "E1446", {"start": v(9.82, -49.34) * mm, "end": v(7.56, -49.96) * mm});
            skLineSegment(sketch, "E1447", {"start": v(7.56, -49.96) * mm, "end": v(4.16, -50.52) * mm});
            skLineSegment(sketch, "E1448", {"start": v(4.16, -50.52) * mm, "end": v(1.62, -50.75) * mm});
            skLineSegment(sketch, "E1449", {"start": v(1.62, -50.75) * mm, "end": v(-0.46, -50.9) * mm});
            skLineSegment(sketch, "E1450", {"start": v(-0.46, -50.9) * mm, "end": v(-3.66, -51.1) * mm});
            skLineSegment(sketch, "E1451", {"start": v(-3.66, -51.1) * mm, "end": v(-7.52, -51.01) * mm});
            skLineSegment(sketch, "E1452", {"start": v(-7.52, -51.01) * mm, "end": v(-9.87, -50.77) * mm});
            skLineSegment(sketch, "E1453", {"start": v(-9.87, -50.77) * mm, "end": v(-12.55, -50.32) * mm});
            skLineSegment(sketch, "E1454", {"start": v(-12.55, -50.32) * mm, "end": v(-15.31, -49.63) * mm});
            skLineSegment(sketch, "E1455", {"start": v(-15.31, -49.63) * mm, "end": v(-18, -48.83) * mm});
            skLineSegment(sketch, "E1456", {"start": v(-18, -48.83) * mm, "end": v(-21.63, -47.6) * mm});
            skLineSegment(sketch, "E1457", {"start": v(-21.63, -47.6) * mm, "end": v(-24.6, -46.4) * mm});
            skLineSegment(sketch, "E1458", {"start": v(-24.6, -46.4) * mm, "end": v(-27.97, -44.6) * mm});
            skLineSegment(sketch, "E1459", {"start": v(-27.97, -44.6) * mm, "end": v(-30.33, -42.97) * mm});
            skLineSegment(sketch, "E1460", {"start": v(-30.33, -42.97) * mm, "end": v(-32.14, -41.36) * mm});
            skLineSegment(sketch, "E1461", {"start": v(-32.14, -41.36) * mm, "end": v(-33.71, -39.9) * mm});
            skLineSegment(sketch, "E1462", {"start": v(-33.71, -39.9) * mm, "end": v(-35.28, -38.1) * mm});
            skLineSegment(sketch, "E1463", {"start": v(-35.28, -38.1) * mm, "end": v(-36.82, -36) * mm});
            skLineSegment(sketch, "E1464", {"start": v(-36.82, -36) * mm, "end": v(-38.49, -33.4) * mm});
            skLineSegment(sketch, "E1465", {"start": v(-38.49, -33.4) * mm, "end": v(-39.3, -31.78) * mm});
            skLineSegment(sketch, "E1466", {"start": v(-39.3, -31.78) * mm, "end": v(-40.58, -29.17) * mm});
            skLineSegment(sketch, "E1467", {"start": v(-40.58, -29.17) * mm, "end": v(-41.38, -27.13) * mm});
            skLineSegment(sketch, "E1468", {"start": v(-41.38, -27.13) * mm, "end": v(-42.3, -23.6) * mm});
            skLineSegment(sketch, "E1469", {"start": v(-42.3, -23.6) * mm, "end": v(-42.78, -20.07) * mm});
            skLineSegment(sketch, "E1470", {"start": v(-42.78, -20.07) * mm, "end": v(-42.9, -17.63) * mm});
            skLineSegment(sketch, "E1471", {"start": v(-42.9, -17.63) * mm, "end": v(-42.67, -14.66) * mm});
            skLineSegment(sketch, "E1472", {"start": v(-42.67, -14.66) * mm, "end": v(-42.45, -12.97) * mm});
            skLineSegment(sketch, "E1473", {"start": v(-42.45, -12.97) * mm, "end": v(-41.7, -9.56) * mm});
            skLineSegment(sketch, "E1474", {"start": v(-41.7, -9.56) * mm, "end": v(-40.7, -6.53) * mm});
            skLineSegment(sketch, "E1475", {"start": v(-40.7, -6.53) * mm, "end": v(-39.08, -3.02) * mm});
            skLineSegment(sketch, "E1476", {"start": v(-39.08, -3.02) * mm, "end": v(-37.25, 0.23) * mm});
            skLineSegment(sketch, "E1477", {"start": v(-37.25, 0.23) * mm, "end": v(-35.59, 2.39) * mm});
            skLineSegment(sketch, "E1478", {"start": v(-35.59, 2.39) * mm, "end": v(-33.63, 4.72) * mm});
            skLineSegment(sketch, "E1479", {"start": v(-33.63, 4.72) * mm, "end": v(-32.56, 5.86) * mm});
            skLineSegment(sketch, "E1480", {"start": v(-32.56, 5.86) * mm, "end": v(-29.37, 8.65) * mm});
            skLineSegment(sketch, "E1481", {"start": v(-29.37, 8.65) * mm, "end": v(-25.2, 11.08) * mm});
            skLineSegment(sketch, "E1482", {"start": v(-25.2, 11.08) * mm, "end": v(-22.16, 12.43) * mm});
            skLineSegment(sketch, "E1483", {"start": v(-22.16, 12.43) * mm, "end": v(-17.88, 13.9) * mm});
            skLineSegment(sketch, "E1484", {"start": v(-17.88, 13.9) * mm, "end": v(-15.14, 14.67) * mm});
            skLineSegment(sketch, "E1485", {"start": v(-15.14, 14.67) * mm, "end": v(-11.72, 15.52) * mm});
            skLineSegment(sketch, "E1486", {"start": v(-11.72, 15.52) * mm, "end": v(-8.97, 15.97) * mm});
            skLineSegment(sketch, "E1487", {"start": v(-8.97, 15.97) * mm, "end": v(-6.7, 16.16) * mm});
            skLineSegment(sketch, "E1488", {"start": v(-6.7, 16.16) * mm, "end": v(-3.04, 16.18) * mm});
            skLineSegment(sketch, "E1489", {"start": v(-3.04, 16.18) * mm, "end": v(-0.5, 16) * mm});
            skLineSegment(sketch, "E1490", {"start": v(-0.5, 16) * mm, "end": v(3.49, 15.7) * mm});
            skLineSegment(sketch, "E1491", {"start": v(3.49, 15.7) * mm, "end": v(7.07, 15.08) * mm});
            skLineSegment(sketch, "E1492", {"start": v(7.07, 15.08) * mm, "end": v(9.95, 14.42) * mm});
            skLineSegment(sketch, "E1493", {"start": v(9.95, 14.42) * mm, "end": v(12.05, 13.75) * mm});
            skLineSegment(sketch, "E1494", {"start": v(12.05, 13.75) * mm, "end": v(15.17, 12.68) * mm});
            skLineSegment(sketch, "E1495", {"start": v(15.17, 12.68) * mm, "end": v(20.2, 10.63) * mm});
            skLineSegment(sketch, "E1496", {"start": v(20.2, 10.63) * mm, "end": v(23.92, 8.93) * mm});
            skLineSegment(sketch, "E1497", {"start": v(23.92, 8.93) * mm, "end": v(25.87, 7.8) * mm});
            skLineSegment(sketch, "E1498", {"start": v(25.87, 7.8) * mm, "end": v(27.83, 6.66) * mm});
            skLineSegment(sketch, "E1499", {"start": v(27.83, 6.66) * mm, "end": v(29.26, 5.5) * mm});
            skLineSegment(sketch, "E1500", {"start": v(29.26, 5.5) * mm, "end": v(31.13, 3.92) * mm});
            skLineSegment(sketch, "E1501", {"start": v(31.13, 3.92) * mm, "end": v(32.55, 2.44) * mm});
            skLineSegment(sketch, "E1502", {"start": v(32.55, 2.44) * mm, "end": v(34.34, 0.61) * mm});
            skLineSegment(sketch, "E1503", {"start": v(34.34, 0.61) * mm, "end": v(36.6, -2.1) * mm});
            skLineSegment(sketch, "E1504", {"start": v(36.6, -2.1) * mm, "end": v(38.44, -4.67) * mm});
            skLineSegment(sketch, "E1505", {"start": v(38.44, -4.67) * mm, "end": v(40.02, -7.13) * mm});
            skLineSegment(sketch, "E1506", {"start": v(40.02, -7.13) * mm, "end": v(41.58, -10.45) * mm});
            skLineSegment(sketch, "E1507", {"start": v(41.58, -10.45) * mm, "end": v(42.43, -12.65) * mm});
            skLineSegment(sketch, "E1508", {"start": v(42.43, -12.65) * mm, "end": v(42.9, -15.34) * mm});
            skLineSegment(sketch, "E1509", {"start": v(42.9, -15.34) * mm, "end": v(43.06, -17.53) * mm});
            skLineSegment(sketch, "E1510", {"start": v(92.09, 34.1) * mm, "end": v(91.82, 35.23) * mm});
            skSolve(sketch);
        }
        {
            var Q0;
            Q0=makeQuery(id+"F0.imprint","IMPRINT",FACE,{"disambiguationData":[TD([[makeQuery(id+"F0.imprint","IMPRINT",EDGE,{"derivedFrom":sQuery(id+"F0.wireOp",EDGE,"E243")}),-1.0]])]});
            var Q1;
            Q1=makeQuery(id+"F0.imprint","IMPRINT",FACE,{"disambiguationData":[TD([[makeQuery(id+"F0.imprint","IMPRINT",EDGE,{"derivedFrom":sQuery(id+"F0.wireOp",EDGE,"E1264")}),1.0]])]});
            extrude(context, id + "F1", {"entities" : qUnion([Q0, Q1]), "depth" : 12 * mm, "offsetDistance" : 25 * mm});
        }
        {
            var Q0;
            {var subQ3=sQuery(id+"F0.wireOp",EDGE,"E516");Q0=makeQuery(id+"F0.imprint","IMPRINT",FACE,{"disambiguationData":[TD([[makeQuery(id+"F0.imprint","IMPRINT",EDGE,{"derivedFrom":subQ3}),-1.0]])]});}
            var Q1;
            Q1=makeQuery(id+"F0.imprint","IMPRINT",FACE,{"disambiguationData":[TD([[makeQuery(id+"F0.imprint","IMPRINT",EDGE,{"derivedFrom":sQuery(id+"F0.wireOp",EDGE,"E1344")}),-1.0]])]});
            extrude(context, id + "F2", {"entities" : qUnion([Q0, Q1]), "depth" : 11 * mm, "offsetDistance" : 25 * mm});
        }
        {
            var Q0;
            {var subQ2=sQuery(id+"F0.wireOp",EDGE,"E298");Q0=makeQuery(id+"F0.imprint","IMPRINT",FACE,{"disambiguationData":[TD([[makeQuery(id+"F0.imprint","IMPRINT",EDGE,{"derivedFrom":subQ2}),-1.0]])]});}
            var Q1;
            Q1=makeQuery(id+"F0.imprint","IMPRINT",FACE,{"disambiguationData":[TD([[makeQuery(id+"F0.imprint","IMPRINT",EDGE,{"derivedFrom":sQuery(id+"F0.wireOp",EDGE,"E1046")}),-1.0]])]});
            extrude(context, id + "F3", {"entities" : qUnion([Q0, Q1]), "depth" : 10 * mm, "offsetDistance" : 25 * mm});
        }
        {
            var Q0;
            Q0=makeQuery(id+"F0.imprint","IMPRINT",FACE,{"disambiguationData":[TD([[makeQuery(id+"F0.imprint","IMPRINT",EDGE,{"derivedFrom":sQuery(id+"F0.wireOp",EDGE,"E977")}),-1.0]])]});
            var Q1;
            {var subQ5=sQuery(id+"F0.wireOp",EDGE,"E300");Q1=makeQuery(id+"F0.imprint","IMPRINT",FACE,{"disambiguationData":[TD([[makeQuery(id+"F0.imprint","IMPRINT",EDGE,{"derivedFrom":subQ5}),-1.0]])]});}
            extrude(context, id + "F4", {"entities" : qUnion([Q0, Q1]), "depth" : 9 * mm, "offsetDistance" : 25 * mm});
        }
        {
            var Q0;
            {var subQ0=sQuery(id+"F0.wireOp",EDGE,"E521");Q0=makeQuery(id+"F0.imprint","IMPRINT",FACE,{"disambiguationData":[TD([[makeQuery(id+"F0.imprint","IMPRINT",EDGE,{"derivedFrom":subQ0}),-1.0]])]});}
            var Q1;
            Q1=makeQuery(id+"F0.imprint","IMPRINT",FACE,{"disambiguationData":[TD([[makeQuery(id+"F0.imprint","IMPRINT",EDGE,{"derivedFrom":sQuery(id+"F0.wireOp",EDGE,"E883")}),-1.0]])]});
            extrude(context, id + "F5", {"entities" : qUnion([Q0, Q1]), "depth" : 8 * mm, "offsetDistance" : 25 * mm});
        }
        {
            var Q0;
            Q0=makeQuery(id+"F0.imprint","IMPRINT",FACE,{"disambiguationData":[TD([[makeQuery(id+"F0.imprint","IMPRINT",EDGE,{"derivedFrom":sQuery(id+"F0.wireOp",EDGE,"E807")}),-1.0]])]});
            var Q1;
            {var subQ1=sQuery(id+"F0.wireOp",EDGE,"E303");Q1=makeQuery(id+"F0.imprint","IMPRINT",FACE,{"disambiguationData":[TD([[makeQuery(id+"F0.imprint","IMPRINT",EDGE,{"derivedFrom":subQ1}),-1.0]])]});}
            extrude(context, id + "F6", {"entities" : qUnion([Q0, Q1]), "depth" : 7 * mm, "offsetDistance" : 25 * mm});
        }
        {
            var Q0;
            Q0=makeQuery(id+"F0.imprint","IMPRINT",FACE,{"disambiguationData":[TD([[makeQuery(id+"F0.imprint","IMPRINT",EDGE,{"derivedFrom":sQuery(id+"F0.wireOp",EDGE,"E318")}),-1.0]])]});
            extrude(context, id + "F7", {"entities" : qUnion([Q0]), "depth" : 6 * mm, "offsetDistance" : 25 * mm});
        }
        {
            var Q0;
            Q0=makeQuery(id+"F0.imprint","IMPRINT",FACE,{"disambiguationData":[TD([[makeQuery(id+"F0.imprint","IMPRINT",EDGE,{"derivedFrom":sQuery(id+"F0.wireOp",EDGE,"E1120")}),1.0]])]});
            extrude(context, id + "F8", {"entities" : qUnion([Q0]), "depth" : 16 * mm, "offsetDistance" : 25 * mm});
        }
        {
            var Q0;
            Q0=makeQuery(id+"F0.imprint","IMPRINT",FACE,{"disambiguationData":[TD([[makeQuery(id+"F0.imprint","IMPRINT",EDGE,{"derivedFrom":sQuery(id+"F0.wireOp",EDGE,"E1120")}),-1.0]])]});
            extrude(context, id + "F9", {"entities" : qUnion([Q0]), "operationType" : NewBodyOperationType.ADD, "depth" : 15 * mm, "offsetDistance" : 25 * mm});
        }
        {
            var Q0;
            Q0=makeQuery(id+"F0.imprint","IMPRINT",FACE,{"disambiguationData":[TD([[makeQuery(id+"F0.imprint","IMPRINT",EDGE,{"derivedFrom":sQuery(id+"F0.wireOp",EDGE,"E1171")}),-1.0]])]});
            extrude(context, id + "F10", {"entities" : qUnion([Q0]), "operationType" : NewBodyOperationType.ADD, "depth" : 14 * mm, "offsetDistance" : 25 * mm});
        }
        {
            var Q0;
            Q0=makeQuery(id+"F0.imprint","IMPRINT",FACE,{"disambiguationData":[TD([[makeQuery(id+"F0.imprint","IMPRINT",EDGE,{"derivedFrom":sQuery(id+"F0.wireOp",EDGE,"E1224")}),1.0]])]});
            extrude(context, id + "F11", {"entities" : qUnion([Q0]), "depth" : 13 * mm, "offsetDistance" : 25 * mm});
        }
        {
            var Q0;
            {var subQ3=sQuery(id+"F0.wireOp",EDGE,"E137");Q0=makeQuery(id+"F0.imprint","IMPRINT",FACE,{"disambiguationData":[TD([[makeQuery(id+"F0.imprint","IMPRINT",EDGE,{"derivedFrom":subQ3}),-1.0]])]});}
            extrude(context, id + "F12", {"entities" : qUnion([Q0]), "operationType" : NewBodyOperationType.ADD, "depth" : 6 * mm, "offsetDistance" : 25 * mm});
        }
        {
            var Q0;
            {var subQ0=sQuery(id+"F0.wireOp",EDGE,"E152");Q0=makeQuery(id+"F0.imprint","IMPRINT",FACE,{"disambiguationData":[TD([[makeQuery(id+"F0.imprint","IMPRINT",EDGE,{"derivedFrom":subQ0}),-1.0]])]});}
            extrude(context, id + "F13", {"entities" : qUnion([Q0]), "depth" : 7 * mm, "offsetDistance" : 25 * mm});
        }
        {
            var Q0;
            {var subQ9=sQuery(id+"F0.wireOp",EDGE,"E159");Q0=makeQuery(id+"F0.imprint","IMPRINT",FACE,{"disambiguationData":[TD([[makeQuery(id+"F0.imprint","IMPRINT",EDGE,{"derivedFrom":subQ9}),-1.0]])]});}
            extrude(context, id + "F14", {"entities" : qUnion([Q0]), "depth" : 8 * mm, "offsetDistance" : 25 * mm});
        }
        {
            var Q0;
            {var subQ3=sQuery(id+"F0.wireOp",EDGE,"E163");Q0=makeQuery(id+"F0.imprint","IMPRINT",FACE,{"disambiguationData":[TD([[makeQuery(id+"F0.imprint","IMPRINT",EDGE,{"derivedFrom":subQ3}),-1.0]])]});}
            extrude(context, id + "F15", {"entities" : qUnion([Q0]), "depth" : 9 * mm, "offsetDistance" : 25 * mm});
        }
        {
            var Q0;
            {var subQ1=sQuery(id+"F0.wireOp",EDGE,"E172");Q0=makeQuery(id+"F0.imprint","IMPRINT",FACE,{"disambiguationData":[TD([[makeQuery(id+"F0.imprint","IMPRINT",EDGE,{"derivedFrom":subQ1}),-1.0]])]});}
            extrude(context, id + "F16", {"entities" : qUnion([Q0]), "depth" : 10 * mm, "offsetDistance" : 25 * mm});
        }
        {
            var Q0;
            {var subQ4=sQuery(id+"F0.wireOp",EDGE,"E197");Q0=makeQuery(id+"F0.imprint","IMPRINT",FACE,{"disambiguationData":[TD([[makeQuery(id+"F0.imprint","IMPRINT",EDGE,{"derivedFrom":subQ4}),-1.0]])]});}
            extrude(context, id + "F17", {"entities" : qUnion([Q0]), "depth" : 11 * mm, "offsetDistance" : 25 * mm});
        }
        {
            var Q0;
            Q0=makeQuery(id+"F0.imprint","IMPRINT",FACE,{"disambiguationData":[TD([[makeQuery(id+"F0.imprint","IMPRINT",EDGE,{"derivedFrom":sQuery(id+"F0.wireOp",EDGE,"E327")}),-1.0]])]});
            var Q1;
            {var subQ2=sQuery(id+"F0.wireOp",EDGE,"E343");Q1=makeQuery(id+"F0.imprint","IMPRINT",FACE,{"disambiguationData":[TD([[makeQuery(id+"F0.imprint","IMPRINT",EDGE,{"derivedFrom":subQ2}),1.0]])]});}
            var Q2;
            Q2=makeQuery(id+"F0.imprint","IMPRINT",FACE,{"disambiguationData":[TD([[makeQuery(id+"F0.imprint","IMPRINT",EDGE,{"derivedFrom":sQuery(id+"F0.wireOp",EDGE,"E0")}),-1.0]])]});
            extrude(context, id + "F18", {"entities" : qUnion([Q0, Q1, Q2]), "depth" : 5 * mm, "offsetDistance" : 25 * mm});
        }
    });
